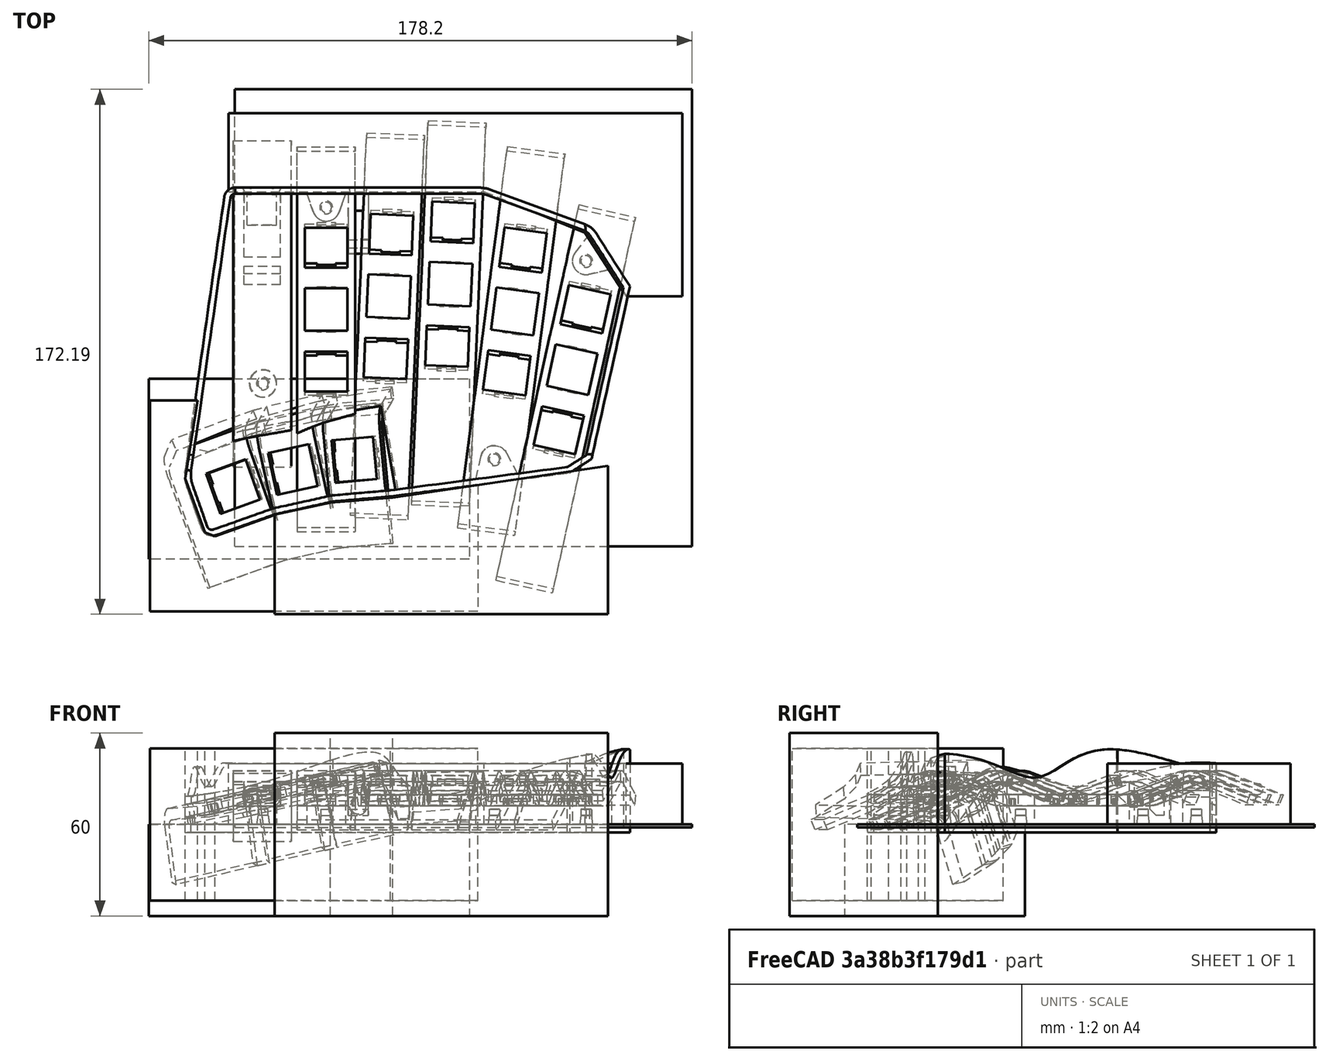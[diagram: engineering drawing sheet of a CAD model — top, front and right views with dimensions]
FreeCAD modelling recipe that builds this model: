
FCSTD DOCUMENT  (FreeCAD 0.21R33668 +26 (Git))
Label: KeyColumnArray2
License: All rights reserved
LicenseURL: http://en.wikipedia.org/wiki/All_rights_reserved
objects: PartDesign::Body×21, PartDesign::SubShapeBinder×20, Sketcher::SketchObject×20, App::Link×19, PartDesign::Pad×17, Part::MultiFuse×10, Part::Cut×9, Part::Compound×8, PartDesign::Plane×5, App::DocumentObjectGroup×4, PartDesign::Pocket×4, PartDesign::CoordinateSystem×3, Part::MultiCommon×2, Mesh::Feature×1, Part::Box×1, PartDesign::AdditivePipe×1, PartDesign::Thickness×1, PartDesign::FeatureBase×1
note: 146 computed .brp shape members not serialized (recipe doc carries the construction recipe); baked Part::Feature solids carry a one-line shape summary decoded from their .brp
EXTERNAL_REF file=KeyColumn2.FCStd obj=Cut001
EXTERNAL_REF file=KeyRowThumb2.FCStd obj=Fusion002
EXTERNAL_REF file=../components/MX_Switches.FCStd obj=Body008
EXTERNAL_REF file=KeyColumn2.FCStd obj=Extrude003
EXTERNAL_REF file=../components/PJ-313B__JACK35F-4P-PCB.FCStd obj=MultiTransform001
EXTERNAL_REF file=../components/RP2040_Zero.FCStd obj=Mesh002
EXTERNAL_REF file=../components/USBC-Breakout.FCStd obj=Body005
EXTERNAL_REF file=../components/PJ-313B__JACK35F-4P-PCB.FCStd obj=Body002
EXTERNAL_REF file=HeatsetInserts.FCStd obj=Cut001
EXTERNAL_REF file=HeatsetInserts.FCStd obj=Cut003
EXTERNAL_REF file=PlateBottom.FCStd obj=Cut001

FEATURE [App::Link] Link  label="KeyColumnCutNC0"
  LinkedObject = -> <external KeyColumn2.FCStd>#Cut001
FEATURE [App::Link] Link001  label="KeyColumnCutNC1"
  LinkPlacement = pos=(20.4361,4.27867,0) rot=(0,0,-1;0.043633rad)
  LinkedObject = -> Link
  Placement = pos=(20.4361,4.27867,0) rot=(0,0,-1;0.043633rad)
FEATURE [App::Link] Link002  label="KeyColumnCutNC2"
  LinkPlacement = pos=(40.6115,8.31848,0) rot=(0,0,-1;0.043633rad)
  LinkedObject = -> Link001
  Placement = pos=(40.6115,8.31848,0) rot=(0,0,-1;0.043633rad)
FEATURE [App::Link] Link003  label="KeyColumnCutNC3"
  LinkPlacement = pos=(61.9106,-0.613054,0) rot=(0,0,-1;0.1309rad)
  LinkedObject = -> Link002
  Placement = pos=(61.9106,-0.613054,0) rot=(0,0,-1;0.1309rad)
FEATURE [App::Link] Link004  label="KeyColumnCutNC4"
  LinkPlacement = pos=(80.6476,-19.7424,0) rot=(0,0,-1;0.218166rad)
  LinkedObject = -> Link003
  Placement = pos=(80.6476,-19.7424,0) rot=(0,0,-1;0.218166rad)
FEATURE [Mesh::Feature] _0240804_Case_RHS_rev0  label="20240804-Case-RHS-rev0"
  Placement = pos=(-0.812616,10.045,0) rot=(0,0,-1;0.043633rad)
FEATURE [App::Link] Link005  label="ThumbCluster"
  LinkPlacement = pos=(-28.6469,-56.4106,8.19493) rot=(0.134414,-0.107879,-0.985035;1.36737rad)
  LinkedObject = -> <external KeyRowThumb2.FCStd>#Fusion002
  Placement = pos=(-28.6469,-56.4106,8.19493) rot=(0.134414,-0.107879,-0.985035;1.36737rad)
FEATURE [PartDesign::SubShapeBinder] Binder  label="BinderThumb"
  BindCopyOnChange = 0
  BindMode = 0
  ClaimChildren = false
  Context = -> Body [Binder.]
  Fuse = false
  MakeFace = true
  OffsetFill = false
  OffsetIntersection = false
  OffsetJoinType = 0
  OffsetOpenResult = false
  PartialLoad = false
  Relative = true
  Support = -> [Link005[Face32]]
  _Version = 2
FEATURE [PartDesign::CoordinateSystem] Local_CS  label="Local_CS_Thumb"
  AttacherType = Attacher::AttachEngine3D
  AttachmentOffset = pos=(7,7,0) rot=(0,0,1;0rad)
  MapMode = 52
  Placement = pos=(-30.571,-58.1118,9.74542) rot=(0.024649,-0.537647,0.84281;0.407362rad)
  Support = -> [Binder]
FEATURE [App::Link] Link006  label="KeycapThumb"
  AttacherType = Attacher::AttachEngine3D
  LinkPlacement = pos=(-30.571,-58.1118,9.74542) rot=(0.024649,-0.537647,0.84281;0.407362rad)
  LinkedObject = -> <external ../components/MX_Switches.FCStd>#Body008
  MapMode = 2
  Placement = pos=(-30.571,-58.1118,9.74542) rot=(0.024649,-0.537647,0.84281;0.407362rad)
  Support = -> [Local_CS]
FEATURE [Part::Box] Box  label="Floor"
  AttacherType = Attacher::AttachEngine3D
  Height = 1
  Length = 150
  Placement = pos=(-30,-77.75,-4e-15) rot=(0.707107,0.707107,0;3.14159rad)
  Width = 150
FEATURE [PartDesign::SubShapeBinder] Binder001  label="BinderFinger"
  BindCopyOnChange = 0
  BindMode = 0
  ClaimChildren = false
  Context = -> Body [Binder001.]
  Fuse = false
  MakeFace = true
  OffsetFill = false
  OffsetIntersection = false
  OffsetJoinType = 0
  OffsetOpenResult = false
  PartialLoad = false
  Relative = true
  Support = -> [Compound[Face79]]
  _Version = 2
FEATURE [PartDesign::CoordinateSystem] Local_CS001  label="Local_CS_Finger"
  AttacherType = Attacher::AttachEngine3D
  AttachmentOffset = pos=(7,7,0) rot=(0,0,1;0rad)
  MapMode = 52
  Placement = pos=(0,-1.8e-15,9.8) rot=(0,0,1;0rad)
  Support = -> [Binder001]
FEATURE [App::Link] Link007  label="KeycapFinger"
  AttacherType = Attacher::AttachEngine3D
  LinkPlacement = pos=(0,-1.8e-15,9.8) rot=(0,0,1;0rad)
  LinkedObject = -> <external ../components/MX_Switches.FCStd>#Body008
  MapMode = 2
  Placement = pos=(0,-1.8e-15,9.8) rot=(0,0,1;0rad)
  Support = -> [Local_CS001]
FEATURE [App::Link] Link008  label="KeyColumnBlankN"
  LinkPlacement = pos=(-21,2.5034e-06,0) rot=(0,0,1;3.14159rad)
  LinkedObject = -> <external KeyColumn2.FCStd>#Extrude003
  Placement = pos=(-21,2.5034e-06,0) rot=(0,0,1;3.14159rad)
FEATURE [Part::Compound] Compound  label="KeyColumnsC"
  Links = -> [Link004,Link,Link001,Link002,Link003,Link008]
  Placement = pos=(0,0,8) rot=(0,0,1;0rad)
FEATURE [App::Link] Link010  label="TRRS-PJ-313B"
  LinkPlacement = pos=(10.5,37.75,3.5) rot=(0,0,1;0rad)
  LinkedObject = -> <external ../components/PJ-313B__JACK35F-4P-PCB.FCStd>#MultiTransform001
  Placement = pos=(10.5,37.75,3.5) rot=(0,0,1;0rad)
FEATURE [App::Link] Link011  label="RP2040-N"
  LinkPlacement = pos=(-30,14.25,8) rot=(0,0,1;0rad)
  LinkedObject = -> <external ../components/RP2040_Zero.FCStd>#Mesh002
  Placement = pos=(-30,14.25,8) rot=(0,0,1;0rad)
FEATURE [Sketcher::SketchObject] Sketch
  FullyConstrained = false
  MapMode = 5
  Support = -> [XY_Plane001]
  sketch-geometry (20):
    g0: LineSegment StartX=-33.4431 StartY=36.9112 StartZ=0 EndX=-46.2795 EndY=-52.5754 EndZ=0
    g1: LineSegment StartX=-45.7128 StartY=-58.285 StartZ=0 EndX=-40.9023 EndY=-71.8694 EndZ=0
    g2: LineSegment StartX=-36.307 StartY=-74.0612 StartZ=0 EndX=-16.9221 EndY=-67.1967 EndZ=0
    g3: LineSegment StartX=-16.9221 StartY=-67.1967 StartZ=0 EndX=2.15083 EndY=-62.9753 EndZ=0
    g4: LineSegment StartX=2.15083 StartY=-62.9753 StartZ=0 EndX=21.2304 EndY=-61.306 EndZ=0
    g5: LineSegment StartX=21.2304 StartY=-61.306 StartZ=0 EndX=79.8355 EndY=-53.6064 EndZ=0
    g6: LineSegment StartX=79.8355 StartY=-53.6064 StartZ=0 EndX=87.0661 EndY=-49 EndZ=0
    g7: LineSegment StartX=87.0661 StartY=-49 StartZ=0 EndX=99.6141 EndY=7.6 EndZ=0
    g8: LineSegment StartX=99.6141 StartY=7.6 StartZ=0 EndX=88.4546 EndY=25.1169 EndZ=0
    g9: LineSegment StartX=84.9582 StartY=27.9288 StartZ=0 EndX=53.9986 EndY=39.268 EndZ=0
    g10: LineSegment StartX=49.8716 StartY=40 StartZ=0 EndX=-29.8796 EndY=40 EndZ=0
    g11: ArcOfCircle CenterX=-37.5088 CenterY=-70.6677 CenterZ=0 NormalX=0 NormalY=0 NormalZ=1 AngleXU=0 Radius=3.6 StartAngle=3.48193 EndAngle=5.05273
    g12: ArcOfCircle CenterX=-29.8796 CenterY=36.4 CenterZ=0 NormalX=0 NormalY=0 NormalZ=1 AngleXU=0 Radius=3.6 StartAngle=1.5708 EndAngle=2.99912
    g13: GeomPoint X=-33 Y=40 Z=0
    g14: ArcOfCircle CenterX=-34.4011 CenterY=-54.2793 CenterZ=0 NormalX=0 NormalY=0 NormalZ=1 AngleXU=0 Radius=12 StartAngle=2.99912 EndAngle=3.48193
    g15: GeomPoint X=-46.699 Y=-55.5 Z=0
    g16: ArcOfCircle CenterX=49.8716 CenterY=28 CenterZ=0 NormalX=0 NormalY=0 NormalZ=1 AngleXU=0 Radius=12 StartAngle=1.21971 EndAngle=1.5708
    g17: GeomPoint X=52 Y=40 Z=0
    g18: ArcOfCircle CenterX=82.5508 CenterY=21.3558 CenterZ=0 NormalX=0 NormalY=0 NormalZ=1 AngleXU=0 Radius=7 StartAngle=0.567232 EndAngle=1.21971
    g19: GeomPoint X=87.1821 Y=27.1143 Z=0
  constraints (43):
    c: Coincident(g2,g3)
    c: Coincident(g3,g4)
    c: Coincident(g4,g5)
    c: Coincident(g5,g6)
    c: Coincident(g6,g7)
    c: Coincident(g7,g8)
    c: Horizontal(g10)
    c: DistanceY(g-1,g17) = 40
    c: DistanceX(g-1,g17) = 52
    c: DistanceX(g13,g-1) = 33
    c: Angle(g-1,g7) = 1.35263
    c: Angle(g7,g6) = 2.35619
    c: Perpendicular(g2,g1)
    c: Angle(g-2,g1) = 0.340339
    c: DistanceY(g15,g-1) = 55.5
    c: Tangent(g1,g11) = -1.5708
    c: Tangent(g2,g11) = -1.5708
    c: Radius(g11) = 3.6
    c: Angle(g-2,g3) = 1.78861
    c: Angle(g4,g-2) = 1.48353
    c: PointOnObject(g13,g0)
    c: PointOnObject(g13,g10)
    c: Tangent(g0,g12) = -1.5708
    c: Tangent(g10,g12) = -1.5708
    c: Radius(g12) = 3.6
    c: PointOnObject(g15,g1)
    c: PointOnObject(g15,g0)
    c: Tangent(g1,g14) = -1.5708
    c: Tangent(g0,g14) = -1.5708
    c: Radius(g14) = 12
    c: PointOnObject(g17,g10)
    c: PointOnObject(g17,g9)
    c: Tangent(g10,g16) = -1.5708
    c: Tangent(g9,g16) = -1.5708
    c: Radius(g16) = 12
    c: PointOnObject(g19,g9)
    c: PointOnObject(g19,g8)
    c: Tangent(g9,g18) = -1.5708
    c: Tangent(g8,g18) = -1.5708
    c: Radius(g18) = 7
    c: Angle(g8,g7) = 2.35619
    c: DistanceY(g-1,g7) = 7.6
    c: DistanceY(g6,g-1) = 49
FEATURE [PartDesign::Pad] Pad
  Direction = (0,0,1)
  Length = 30
  Length2 = 10
  Profile = -> Sketch
  ReferenceAxis = -> Sketch [N_Axis]
  Type = 0
FEATURE [Sketcher::SketchObject] Sketch001
  FullyConstrained = false
  MapMode = 5
  Support = -> [XY_Plane002]
  sketch-geometry (7):
    g0: LineSegment StartX=-31.9823 StartY=64.42 StartZ=0 EndX=-31.9823 EndY=38.6825 EndZ=0
    g1: LineSegment StartX=-31.9823 StartY=38.6825 StartZ=0 EndX=51.7413 EndY=38.6825 EndZ=0
    g2: LineSegment StartX=51.7413 StartY=38.6825 StartZ=0 EndX=84.9247 EndY=25.1531 EndZ=0
    g3: LineSegment StartX=84.9247 StartY=25.1531 StartZ=0 EndX=98.4266 EndY=4.34688 EndZ=0
    g4: LineSegment StartX=98.4266 StartY=4.34688 StartZ=0 EndX=116.798 EndY=4.34688 EndZ=0
    g5: LineSegment StartX=116.798 StartY=4.34688 StartZ=0 EndX=116.798 EndY=64.42 EndZ=0
    g6: LineSegment StartX=116.798 StartY=64.42 StartZ=0 EndX=-31.9823 EndY=64.42 EndZ=0
  constraints (12):
    c: Vertical(g0)
    c: Coincident(g0,g1)
    c: Horizontal(g1)
    c: Coincident(g1,g2)
    c: Coincident(g2,g3)
    c: Coincident(g3,g4)
    c: Horizontal(g4)
    c: Coincident(g4,g5)
    c: Vertical(g5)
    c: Coincident(g5,g6)
    c: Coincident(g6,g0)
    c: Horizontal(g6)
FEATURE [PartDesign::Pad] Pad001
  Direction = (0,0,1)
  Length = 20
  Length2 = 10
  Profile = -> Sketch001
  ReferenceAxis = -> Sketch001 [N_Axis]
  Type = 0
FEATURE [PartDesign::Body] Body002  label="ColumnCutterTop"
  Group = -> [Sketch001,Pad001]
  Origin = -> Origin002
  Tip = -> Pad001
FEATURE [Sketcher::SketchObject] Sketch002
  FullyConstrained = false
  MapMode = 5
  Support = -> [XY_Plane003]
  sketch-geometry (11):
    g0: LineSegment StartX=-57.8461 StartY=-29.8467 StartZ=0 EndX=-42.1659 EndY=-29.8467 EndZ=0
    g1: LineSegment StartX=-42.1659 StartY=-29.8467 StartZ=0 EndX=-46.2211 EndY=-55.5298 EndZ=0
    g2: LineSegment StartX=-46.2211 StartY=-55.5298 StartZ=0 EndX=-39.7328 EndY=-73.1024 EndZ=0
    g3: LineSegment StartX=-39.7328 StartY=-73.1024 StartZ=0 EndX=-36.4886 EndY=-74.4541 EndZ=0
    g4: LineSegment StartX=-36.4886 StartY=-74.4541 StartZ=0 EndX=-17.0235 EndY=-67.4251 EndZ=0
    g5: LineSegment StartX=-17.0235 StartY=-67.4251 StartZ=0 EndX=1.36017 EndY=-63.3699 EndZ=0
    g6: LineSegment StartX=1.36017 StartY=-63.3699 StartZ=0 EndX=21.0956 EndY=-61.4774 EndZ=0
    g7: LineSegment StartX=21.0956 StartY=-61.4774 StartZ=0 EndX=49.7525 EndY=-57.6925 EndZ=0
    g8: LineSegment StartX=49.7525 StartY=-57.6925 StartZ=0 EndX=49.7525 EndY=-99.0559 EndZ=0
    g9: LineSegment StartX=49.7525 StartY=-99.0559 StartZ=0 EndX=-57.8461 EndY=-99.0559 EndZ=0
    g10: LineSegment StartX=-57.8461 StartY=-99.0559 StartZ=0 EndX=-57.8461 EndY=-29.8467 EndZ=0
  constraints (15):
    c: Horizontal(g0)
    c: Coincident(g0,g1)
    c: Coincident(g1,g2)
    c: Coincident(g2,g3)
    c: Coincident(g3,g4)
    c: Coincident(g4,g5)
    c: Coincident(g5,g6)
    c: Coincident(g6,g7)
    c: Coincident(g7,g8)
    c: Vertical(g8)
    c: Coincident(g8,g9)
    c: Horizontal(g9)
    c: Coincident(g9,g10)
    c: Coincident(g10,g0)
    c: Vertical(g10)
FEATURE [PartDesign::Pad] Pad002
  Direction = (0,0,1)
  Length = 50
  Length2 = 10
  Midplane = true
  Profile = -> Sketch002
  ReferenceAxis = -> Sketch002 [N_Axis]
  Type = 0
FEATURE [PartDesign::Body] Body003  label="ThumbCutterBotLeft"
  Group = -> [Sketch002,Pad002]
  Origin = -> Origin003
  Tip = -> Pad002
FEATURE [Sketcher::SketchObject] Sketch003
  FullyConstrained = false
  MapMode = 5
  Support = -> [XY_Plane004]
  sketch-geometry (4):
    g0: LineSegment StartX=-58.202 StartY=-22.7672 StartZ=0 EndX=46.9496 EndY=-22.7672 EndZ=0
    g1: LineSegment StartX=46.9496 StartY=-22.7672 StartZ=0 EndX=46.9496 EndY=-81.8868 EndZ=0
    g2: LineSegment StartX=46.9496 StartY=-81.8868 StartZ=0 EndX=-58.202 EndY=-81.8868 EndZ=0
    g3: LineSegment StartX=-58.202 StartY=-81.8868 StartZ=0 EndX=-58.202 EndY=-22.7672 EndZ=0
  constraints (8):
    c: Coincident(g0,g1)
    c: Coincident(g1,g2)
    c: Coincident(g2,g3)
    c: Coincident(g3,g0)
    c: Horizontal(g0)
    c: Horizontal(g2)
    c: Vertical(g1)
    c: Vertical(g3)
FEATURE [PartDesign::Pad] Pad003
  Direction = (0,0,1)
  Length = 30
  Length2 = 10
  Profile = -> Sketch003
  ReferenceAxis = -> Sketch003 [N_Axis]
  Reversed = true
  Type = 0
FEATURE [PartDesign::Body] Body004  label="ThumbCutterBottom"
  Group = -> [Sketch003,Pad003]
  Origin = -> Origin004
  Tip = -> Pad003
FEATURE [Sketcher::SketchObject] Sketch004
  FullyConstrained = false
  MapMode = 5
  Support = -> [XY_Plane005]
  sketch-geometry (6):
    g0: LineSegment StartX=-16.8908 StartY=-67.2591 StartZ=0 EndX=1.39342 EndY=-63.2974 EndZ=0
    g1: LineSegment StartX=1.39342 StartY=-63.2974 StartZ=0 EndX=21.8742 EndY=-61.6751 EndZ=0
    g2: LineSegment StartX=21.8742 StartY=-61.6751 StartZ=0 EndX=92.4415 EndY=-51.3334 EndZ=0
    g3: LineSegment StartX=92.4415 StartY=-51.3334 StartZ=0 EndX=92.4415 EndY=-99.9441 EndZ=0
    g4: LineSegment StartX=92.4415 StartY=-99.9441 StartZ=0 EndX=-16.8908 EndY=-99.9441 EndZ=0
    g5: LineSegment StartX=-16.8908 StartY=-99.9441 StartZ=0 EndX=-16.8908 EndY=-67.2591 EndZ=0
  constraints (9):
    c: Coincident(g0,g1)
    c: Coincident(g1,g2)
    c: Coincident(g2,g3)
    c: Vertical(g3)
    c: Coincident(g3,g4)
    c: Horizontal(g4)
    c: Coincident(g4,g5)
    c: Coincident(g5,g0)
    c: Vertical(g5)
FEATURE [PartDesign::Pad] Pad004
  Direction = (0,0,1)
  Length = 60
  Length2 = 10
  Midplane = true
  Profile = -> Sketch004
  ReferenceAxis = -> Sketch004 [N_Axis]
  Type = 0
FEATURE [PartDesign::Body] Body005  label="ColumnCutterBottom"
  Group = -> [Sketch004,Pad004]
  Origin = -> Origin005
  Tip = -> Pad004
FEATURE [Part::Compound] Compound001  label="ColumnCutters"
  Links = -> [Body005,Body002]
FEATURE [Part::MultiFuse] Fusion
  Shapes = -> [Compound]
FEATURE [Part::Compound] Compound002  label="ThumbCutters"
  Links = -> [Body003,Body004]
FEATURE [Part::Cut] Cut001
  Base = -> Link005
  Tool = -> Body003
FEATURE [Part::Cut] Cut002  label="ThumbClusterCut"
  Base = -> Cut001
  Tool = -> Body004
FEATURE [Part::Compound] Compound003  label="ThumbClusterC"
  Links = -> [Link005]
FEATURE [PartDesign::SubShapeBinder] Binder003  label="Big"
  BindCopyOnChange = 0
  BindMode = 0
  ClaimChildren = false
  Context = -> Body006 [Binder003.]
  Fuse = false
  MakeFace = true
  OffsetFill = false
  OffsetIntersection = false
  OffsetJoinType = 0
  OffsetOpenResult = false
  PartialLoad = false
  Relative = true
  Support = -> [Cut002[Edge44,Edge45,Edge46,Edge47]]
  _Version = 2
FEATURE [PartDesign::SubShapeBinder] Binder004  label="Small"
  BindCopyOnChange = 0
  BindMode = 0
  ClaimChildren = false
  Context = -> Body006 [Binder004.]
  Fuse = false
  MakeFace = true
  OffsetFill = false
  OffsetIntersection = false
  OffsetJoinType = 0
  OffsetOpenResult = false
  PartialLoad = false
  Relative = true
  Support = -> [Cut002[Edge127,Edge129,Edge130,Edge131]]
  _Version = 2
FEATURE [PartDesign::SubShapeBinder] Binder005  label="Path"
  BindCopyOnChange = 0
  BindMode = 0
  ClaimChildren = false
  Context = -> Body006 [Binder005.]
  Fuse = false
  MakeFace = true
  OffsetFill = false
  OffsetIntersection = false
  OffsetJoinType = 0
  OffsetOpenResult = false
  PartialLoad = false
  Relative = true
  Support = -> [Cut002[Edge127,Edge126,Edge123,Edge122,Edge109]]
  _Version = 2
FEATURE [Sketcher::SketchObject] Sketch005
  FullyConstrained = false
  Placement = pos=(-2.47193,-0.548013,11.4209) rot=(0.216439,-0.976296,0;0.218166rad)
  sketch-geometry (5):
    g0: LineSegment StartX=21.4334 StartY=-34.223 StartZ=0 EndX=2.51313 EndY=-35.9615 EndZ=0
    g1: BSplineCurve PolesCount=2 KnotsCount=2 Degree=1 IsPeriodic=0
    g2: LineSegment StartX=-1.05539 StartY=-36.5965 StartZ=0 EndX=-19.605 EndY=-40.7088 EndZ=0
    g3: BSplineCurve PolesCount=2 KnotsCount=2 Degree=1 IsPeriodic=0
    g4: LineSegment StartX=-23.1076 StartY=-41.6414 StartZ=0 EndX=-40.9899 EndY=-48.0619 EndZ=0
  constraints (4):
    c: Coincident(g0,g1)
    c: Coincident(g1,g2)
    c: Coincident(g2,g3)
    c: Coincident(g3,g4)
FEATURE [Sketcher::SketchObject] Sketch006
  FullyConstrained = false
  Placement = pos=(-50.3364,-18.2454,-11.7703) rot=(0.340774,-0.940145,0;1.78719rad)
  sketch-geometry (4):
    g0: LineSegment StartX=34.9538 StartY=-48.5618 StartZ=0 EndX=33.5799 EndY=-45.0789 EndZ=0
    g1: LineSegment StartX=33.5799 StartY=-45.0789 StartZ=0 EndX=26.6082 EndY=-27.4042 EndZ=0
    g2: ArcOfCircle CenterX=22.8872 CenterY=-28.8719 CenterZ=0 NormalX=0 NormalY=1e-16 NormalZ=1 AngleXU=-2.76588 Radius=4 StartAngle=1.5708 EndAngle=2.88852
    g3: LineSegment StartX=21.8685 StartY=-24.9672 StartZ=0 EndX=22.3979 EndY=-24.902 EndZ=0
  constraints (3):
    c: Coincident(g0,g1)
    c: Coincident(g1,g2)
    c: Coincident(g2,g3)
FEATURE [Sketcher::SketchObject] Sketch007
  FullyConstrained = false
  Placement = pos=(17.7176,1.57374,3.9103) rot=(-0.088475,0.996078,0;1.3544rad)
  sketch-geometry (6):
    g0: LineSegment StartX=-9.09004 StartY=-79.2968 StartZ=0 EndX=-11.138 EndY=-61.1386 EndZ=0
    g1: LineSegment StartX=-11.138 StartY=-61.1386 StartZ=0 EndX=-13.3253 EndY=-42.1061 EndZ=0
    g2: ArcOfCircle CenterX=-5.98227 CenterY=-40.8863 CenterZ=0 NormalX=1e-16 NormalY=0 NormalZ=1 AngleXU=-1.45423 Radius=7.44361 StartAngle=3.36428 EndAngle=4.76043
    g3: LineSegment StartX=9.38655 StartY=-26.7286 StartZ=0 EndX=-8.45934 EndY=-33.867 EndZ=0
    g4: LineSegment StartX=-9.09004 StartY=-79.2968 StartZ=0 EndX=18.9825 EndY=-76.3619 EndZ=0
    g5: LineSegment StartX=18.9825 StartY=-76.3619 StartZ=0 EndX=9.38655 EndY=-26.7286 EndZ=0
  constraints (6):
    c: Coincident(g0,g1)
    c: Coincident(g1,g2)
    c: Coincident(g2,g3)
    c: Coincident(g0,g4)
    c: Coincident(g4,g5)
    c: Coincident(g5,g3)
FEATURE [PartDesign::AdditivePipe] AdditivePipe
  AuxilleryCurvelinear = true
  AuxillerySpineTangent = false
  Binormal = (0,0,0)
  Mode = 0
  Placement = pos=(17.7176,1.57374,3.9103) rot=(-0.088475,0.996078,0;1.3544rad)
  Profile = -> Sketch007
  Spine = -> Binder005
  SpineTangent = false
  Transformation = 0
  Transition = 0
FEATURE [PartDesign::Body] Body006  label="UnderThumbCutter"
  Group = -> [Binder003,Binder004,Binder005,Sketch005,Sketch006,Sketch007,AdditivePipe]
  Origin = -> Origin006
  Tip = -> AdditivePipe
FEATURE [Sketcher::SketchObject] Sketch008
  FullyConstrained = true
  MapMode = 5
  Placement = pos=(0,0,0) rot=(0.57735,0.57735,0.57735;2.0944rad)
  Support = -> [YZ_Plane007]
  sketch-geometry (8):
    g0: LineSegment StartX=-24 StartY=5.5 StartZ=0 EndX=-24 EndY=0 EndZ=0
    g1: LineSegment StartX=-24 StartY=0 StartZ=0 EndX=1.25 EndY=0 EndZ=0
    g2: LineSegment StartX=1.25 StartY=0 StartZ=0 EndX=1.25 EndY=-3.6 EndZ=0
    g3: LineSegment StartX=1.25 StartY=-3.6 StartZ=0 EndX=-4.9788 EndY=-4.78813 EndZ=0
    g4: LineSegment StartX=-4.9788 StartY=-4.78813 StartZ=0 EndX=-30.1 EndY=0 EndZ=0
    g5: LineSegment StartX=-30.1 StartY=0 StartZ=0 EndX=-30.1 EndY=2 EndZ=0
    g6: LineSegment StartX=-30.1 StartY=2 StartZ=0 EndX=-26.6 EndY=5.5 EndZ=0
    g7: LineSegment StartX=-26.6 StartY=5.5 StartZ=0 EndX=-24 EndY=5.5 EndZ=0
  constraints (24):
    c: PointOnObject(g0,g-1)
    c: Vertical(g0)
    c: Coincident(g0,g1)
    c: Horizontal(g1)
    c: Coincident(g1,g2)
    c: Vertical(g2)
    c: Coincident(g2,g3)
    c: Coincident(g3,g4)
    c: PointOnObject(g4,g-1)
    c: Coincident(g4,g5)
    c: Vertical(g5)
    c: Coincident(g5,g6)
    c: Coincident(g6,g7)
    c: Coincident(g7,g0)
    c: Horizontal(g7)
    c: DistanceX(g7,g7) = 2.6
    c: DistanceY(g0,g0) = 5.5
    c: DistanceX(g5,g6) = 3.5
    c: Angle(g6,g7) = 2.35619
    c: DistanceX(g0,g-1) = 24
    c: DistanceX(g-1,g1) = 1.25
    c: DistanceY(g2,g2) = 3.6
    c: DistanceX(g3) = -4.9788
    c: DistanceY(g3) = -4.78813
FEATURE [PartDesign::Pad] Pad005
  Direction = (1,-2e-16,3e-16)
  Length = 12
  Length2 = 10
  Midplane = true
  Placement = pos=(0,0,0) rot=(0.57735,0.57735,0.57735;2.0944rad)
  Profile = -> Sketch008
  ReferenceAxis = -> Sketch008 [N_Axis]
  Type = 0
FEATURE [PartDesign::Body] Body007  label="MCU-Holder"
  Group = -> [Sketch008,Pad005]
  Origin = -> Origin007
  Placement = pos=(-21,38.25,11.25) rot=(0,1,0;3.14159rad)
  Tip = -> Pad005
FEATURE [Sketcher::SketchObject] Sketch009
  FullyConstrained = false
  MapMode = 5
  Placement = pos=(0,0,0) rot=(0.57735,0.57735,0.57735;2.0944rad)
  Support = -> [YZ_Plane008]
  sketch-geometry (9):
    g0: LineSegment StartX=39.5 StartY=9 StartZ=0 EndX=22.8616 EndY=9 EndZ=0
    g1: LineSegment StartX=22.8616 StartY=9 StartZ=0 EndX=22.8616 EndY=3 EndZ=0
    g2: LineSegment StartX=22.8616 StartY=3 StartZ=0 EndX=20.2616 EndY=3 EndZ=0
    g3: LineSegment StartX=20.2616 StartY=3 StartZ=0 EndX=18.2616 EndY=5 EndZ=0
    g4: LineSegment StartX=18.2616 StartY=5 StartZ=0 EndX=18.2616 EndY=10.5 EndZ=0
    g5: LineSegment StartX=39.5 StartY=11.5 StartZ=0 EndX=39.5 EndY=9 EndZ=0
    g6: LineSegment StartX=18.2616 StartY=10.5 StartZ=0 EndX=32.4662 EndY=16.0518 EndZ=0
    g7: LineSegment StartX=32.4662 StartY=16.0518 StartZ=0 EndX=39.5 EndY=13.7315 EndZ=0
    g8: LineSegment StartX=39.5 StartY=11.5 StartZ=0 EndX=39.5 EndY=13.7315 EndZ=0
  constraints (22):
    c: Horizontal(g0)
    c: Coincident(g0,g1)
    c: Vertical(g1)
    c: Coincident(g1,g2)
    c: Coincident(g2,g3)
    c: Coincident(g3,g4)
    c: Vertical(g4)
    c: Coincident(g5,g0)
    c: Vertical(g5)
    c: DistanceX(g0) = 39.5
    c: DistanceY(g0) = 9
    c: DistanceY(g5,g5) = 2.5
    c: Horizontal(g2)
    c: DistanceX(g2,g2) = 2.6
    c: Angle(g2,g3) = 2.35619
    c: DistanceY(g1,g1) = 6
    c: DistanceY(g2,g3) = 2
    c: Coincident(g6,g7)
    c: Coincident(g8,g5)
    c: Coincident(g8,g7)
    c: Vertical(g8)
    c: Coincident(g6,g4)
FEATURE [PartDesign::Pad] Pad006
  Direction = (1,-2e-16,3e-16)
  Length = 6.5
  Length2 = 10
  Midplane = true
  Placement = pos=(0,0,0) rot=(1,1,1;2.0944rad)
  Profile = -> Sketch009
  ReferenceAxis = -> Sketch009 [N_Axis]
  Type = 0
FEATURE [PartDesign::Body] Body008  label="TRRS-Holder"
  Group = -> [Sketch009,Pad006]
  Origin = -> Origin008
  Placement = pos=(10.5,0,0) rot=(0,0,1;0rad)
  Tip = -> Pad006
FEATURE [App::Link] Link012  label="MCU-Cutter"
  LinkPlacement = pos=(-21.17,19.2029,7) rot=(0,0,1;3.14159rad)
  LinkedObject = -> <external ../components/USBC-Breakout.FCStd>#Body005
  Placement = pos=(-21.17,19.2029,7) rot=(0,0,1;3.14159rad)
FEATURE [App::Link] Link013  label="TRRS-Cutter"
  LinkPlacement = pos=(10.5,31.25,3.5) rot=(0,0,1;0rad)
  LinkedObject = -> <external ../components/PJ-313B__JACK35F-4P-PCB.FCStd>#Body002
  Placement = pos=(10.5,31.25,3.5) rot=(0,0,1;0rad)
FEATURE [App::DocumentObjectGroup] Group001  label="Parts"
  Group = -> [Link010,Link011,Link012,Link013]
FEATURE [App::Link] Link014  label="HeatsetTopRightA"
  LinkPlacement = pos=(85.2349,15.9434,3) rot=(0,0,1;2.13803rad)
  LinkedObject = -> <external HeatsetInserts.FCStd>#Cut001
  Placement = pos=(85.2349,15.9434,3) rot=(0,0,1;2.13803rad)
FEATURE [App::Link] Link015  label="HeatsetTopLeftA"
  LinkPlacement = pos=(5.38627e-06,33.5,3) rot=(0,0,1;3.14159rad)
  LinkedObject = -> Link014
  Placement = pos=(5.38627e-06,33.5,3) rot=(0,0,1;3.14159rad)
FEATURE [App::Link] Link017  label="HeatsetBotRightA"
  LinkPlacement = pos=(55.1436,-49.1268,3) rot=(0,0,1;0.1309rad)
  LinkedObject = -> Link014
  Placement = pos=(55.1436,-49.1268,3) rot=(0,0,1;0.1309rad)
FEATURE [PartDesign::Thickness] Thickness
  Base = -> Pad [Face18,Face17]
  BaseFeature = -> Pad
  Intersection = false
  Join = 0
  Mode = 0
  Reversed = true
  SupportTransform = false
  Value = 2
FEATURE [PartDesign::Body] Body001  label="ShellRough"
  Group = -> [Sketch,Pad,Thickness]
  Origin = -> Origin001
  Tip = -> Thickness
FEATURE [PartDesign::SubShapeBinder] Binder006  label="BinderFingerR2C4"
  BindCopyOnChange = 0
  BindMode = 0
  ClaimChildren = false
  Context = -> Body [Binder006.]
  Fuse = false
  MakeFace = true
  OffsetFill = false
  OffsetIntersection = false
  OffsetJoinType = 0
  OffsetOpenResult = false
  PartialLoad = false
  Relative = true
  Support = -> [Compound[Face19]]
  _Version = 2
FEATURE [PartDesign::CoordinateSystem] Local_CS002  label="Local_CS_FR2C4"
  AttacherType = Attacher::AttachEngine3D
  AttachmentOffset = pos=(7,7,0) rot=(0,0,1;0rad)
  MapMode = 52
  Placement = pos=(76.2491,-39.5828,13.5665) rot=(-0.857127,0.093871,-0.50648;0.425909rad)
  Support = -> [Binder006]
FEATURE [PartDesign::Body] Body  label="BodyForLCS"
  Group = -> [Binder,Local_CS,Binder001,Local_CS001,Binder006,Local_CS002]
  Origin = -> Origin
FEATURE [App::Link] Link018  label="KeycapFinger001"
  AttacherType = Attacher::AttachEngine3D
  LinkPlacement = pos=(76.2491,-39.5828,13.5665) rot=(-0.857127,0.093871,-0.50648;0.425909rad)
  LinkedObject = -> Link007
  MapMode = 2
  Placement = pos=(76.2491,-39.5828,13.5665) rot=(-0.857127,0.093871,-0.50648;0.425909rad)
  Support = -> [Local_CS002]
FEATURE [App::DocumentObjectGroup] Group  label="Keycaps"
  Group = -> [Link006,Link007,Link018,Body]
FEATURE [PartDesign::FeatureBase] BaseFeature
  BaseFeature = -> Pad
FEATURE [PartDesign::Body] Body009  label="ShellCutterPart"
  BaseFeature = -> Pad
  Group = -> [BaseFeature]
  Origin = -> Origin009
  Tip = -> BaseFeature
FEATURE [Part::Compound] Compound004  label="ThumbClusterC001"
  Links = -> [Link005]
FEATURE [Part::MultiCommon] Common  label="ThumbClusterCom"
  Refine = true
  Shapes = -> [Body009,Compound004]
FEATURE [Part::MultiFuse] Fusion001  label="KeyColumnsF"
  Shapes = -> [Compound]
FEATURE [Part::MultiCommon] Common001  label="KeyColumnsCom"
  Refine = true
  Shapes = -> [Body009,Fusion001]
FEATURE [Part::Cut] Cut  label="KeyColumnsCut"
  Base = -> Common001
  Tool = -> Body006
FEATURE [PartDesign::SubShapeBinder] Binder008
  BindCopyOnChange = 0
  BindMode = 0
  ClaimChildren = false
  Context = -> Body010 [Binder008.]
  Fuse = false
  MakeFace = true
  OffsetFill = false
  OffsetIntersection = false
  OffsetJoinType = 0
  OffsetOpenResult = false
  PartialLoad = false
  Relative = true
  Support = -> [Common[Face16,Face15,Face14,Face13,Face12]]
  _Version = 2
FEATURE [PartDesign::SubShapeBinder] Binder009
  BindCopyOnChange = 0
  BindMode = 0
  ClaimChildren = false
  Context = -> Body010 [Binder009.]
  Fuse = false
  MakeFace = true
  OffsetFill = false
  OffsetIntersection = false
  OffsetJoinType = 0
  OffsetOpenResult = false
  PartialLoad = false
  Relative = true
  Support = -> [Common[Face6,Face7,Face8,Face9,Face10]]
  _Version = 2
FEATURE [PartDesign::Plane] DatumPlane
  Length = 90.3213
  MapMode = 45
  Placement = pos=(10.8462,-31.5971,6.48979) rot=(-0.487707,-0.562269,-0.667829;1.80626rad)
  ResizeMode = 0
  Support = -> [Binder008,Binder009]
  Width = 97.1376
FEATURE [Sketcher::SketchObject] Sketch010
  FullyConstrained = false
  MapMode = 5
  Placement = pos=(10.8462,-31.5971,6.48979) rot=(-0.487707,-0.562269,-0.667829;1.80626rad)
  Support = -> [DatumPlane]
  sketch-geometry (7):
    g0: LineSegment StartX=-5.99127 StartY=-62.4069 StartZ=0 EndX=-2.7146 EndY=-38.9241 EndZ=0
    g1: LineSegment StartX=-2.7146 StartY=-38.9241 StartZ=0 EndX=-1.48585 EndY=-31.6881 EndZ=0
    g2: LineSegment StartX=-1.48585 StartY=-31.6881 StartZ=0 EndX=1.51776 EndY=-16.1239 EndZ=0
    g3: LineSegment StartX=1.51776 StartY=-16.1239 StartZ=0 EndX=2.88304 EndY=-9.5706 EndZ=0
    g4: LineSegment StartX=2.88304 StartY=-9.5706 StartZ=0 EndX=7.38846 EndY=8.9972 EndZ=0
    g5: LineSegment StartX=7.38846 StartY=8.9972 StartZ=0 EndX=-10.3602 EndY=14.0487 EndZ=0
    g6: LineSegment StartX=-10.3602 StartY=14.0487 StartZ=0 EndX=-5.99127 EndY=-62.4069 EndZ=0
  constraints (7):
    c: Coincident(g0,g1)
    c: Coincident(g1,g2)
    c: Coincident(g2,g3)
    c: Coincident(g3,g4)
    c: Coincident(g4,g5)
    c: Coincident(g5,g6)
    c: Coincident(g6,g0)
FEATURE [PartDesign::Pad] Pad007
  Direction = (-0.145065,0.93735,0.31675)
  Length = 20
  Length2 = 10
  Midplane = true
  Placement = pos=(10.8462,-31.5971,6.48979) rot=(-0.487707,-0.562269,-0.667829;1.80626rad)
  Profile = -> Sketch010
  ReferenceAxis = -> Sketch010 [N_Axis]
  Type = 0
FEATURE [PartDesign::Body] Body010  label="ThumbTriangleCutter"
  Group = -> [Binder008,Binder009,DatumPlane,Sketch010,Pad007]
  Origin = -> Origin010
  Tip = -> Pad007
FEATURE [Part::Cut] Cut003  label="ThumbClusterCut2"
  Base = -> Common
  Tool = -> Body010
FEATURE [Part::Compound] Compound005
  Links = -> [Body001]
FEATURE [App::DocumentObjectGroup] Group003  label="Shell"
FEATURE [Sketcher::SketchObject] Sketch011
  FullyConstrained = false
  MapMode = 5
  Placement = pos=(0,0,0) rot=(1,0,0;1.5708rad)
  Support = -> [XZ_Plane011]
  sketch-geometry (23):
    g0: LineSegment StartX=-51.25 StartY=39.47 StartZ=0 EndX=-51.25 EndY=8.74275 EndZ=0
    g1: LineSegment StartX=-51.25 StartY=8.74275 StartZ=0 EndX=18.1024 EndY=24.754 EndZ=0
    g2: LineSegment StartX=22.4199 StartY=22.0561 StartZ=0 EndX=24.2026 EndY=14.3346 EndZ=0
    g3: LineSegment StartX=28.2541 StartY=11.5857 StartZ=0 EndX=107.47 EndY=23.6899 EndZ=0
    g4: LineSegment StartX=107.47 StartY=23.6899 StartZ=0 EndX=107.47 EndY=39.47 EndZ=0
    g5: LineSegment StartX=107.47 StartY=39.47 StartZ=0 EndX=-51.25 EndY=39.47 EndZ=0
    g6: ArcOfCircle CenterX=18.9122 CenterY=21.2463 CenterZ=0 NormalX=0 NormalY=0 NormalZ=1 AngleXU=0 Radius=3.6 StartAngle=0.226893 EndAngle=1.79769
    g7: ArcOfCircle CenterX=27.7103 CenterY=15.1444 CenterZ=0 NormalX=0 NormalY=0 NormalZ=1 AngleXU=0 Radius=3.6 StartAngle=3.36849 EndAngle=4.86402
    g8-g15: Circle x8 (B-spline internal-alignment scaffolding for g16; pole/knot coordinates omitted)
    g16: BSplineCurve PolesCount=8 KnotsCount=6 Degree=3 IsPeriodic=0
    g17-g22: GeomPoint x6 (B-spline internal-alignment scaffolding for g16; pole/knot coordinates omitted)
  constraints (24):
    c: Vertical(g0)
    c: Coincident(g0,g1)
    c: Coincident(g3,g4)
    c: Vertical(g4)
    c: Coincident(g4,g5)
    c: Coincident(g5,g0)
    c: Horizontal(g5)
    c: Tangent(g1,g6) = 1.5708
    c: Tangent(g2,g6) = 1.5708
    c: Tangent(g2,g7) = -1.5708
    c: Tangent(g3,g7) = -1.5708
    c: Radius(g6) = 3.6
    c: Radius(g7) = 3.6
    c: DistanceX(g0,g-1) = 51.25
    c: DistanceX(g-1,g3) = 107.47
    c: DistanceY(g-1,g0) = 39.47
    c: Angle(g-1,g1) = 0.226893
    c: Perpendicular(g2,g1)
    c: Weight(g8) = 1
    c: Coincident(g16,g0)
    c: Equal(g8, g9-g15) x7
    c: Coincident(g16,g4)
    c: InternalAlignment(g8-g15 -> g16) x8
    c: InternalAlignment(g17-g22 -> g16) x6
FEATURE [PartDesign::Pad] Pad008
  Direction = (0,-1,2e-16)
  Length = 40
  Length2 = 10
  Placement = pos=(0,0,0) rot=(1,0,0;1.5708rad)
  Profile = -> Sketch011
  ReferenceAxis = -> Sketch011 [N_Axis]
  Type = 0
FEATURE [PartDesign::Body] Body011  label="WaveFront"
  Group = -> [Sketch011,Pad008]
  Origin = -> Origin011
  Placement = pos=(0,-47.5,0) rot=(0,0,1;0rad)
  Tip = -> Pad008
FEATURE [Part::Cut] Cut004
  Base = -> Compound005
  Tool = -> Body011
FEATURE [PartDesign::SubShapeBinder] Binder010
  BindCopyOnChange = 0
  BindMode = 0
  ClaimChildren = false
  Context = -> Body012 [Binder010.]
  Fuse = false
  MakeFace = true
  OffsetFill = false
  OffsetIntersection = false
  OffsetJoinType = 0
  OffsetOpenResult = false
  PartialLoad = false
  Relative = true
  Support = -> [Cut004[Face1]]
  _Version = 2
FEATURE [Sketcher::SketchObject] Sketch012
  ExternalGeometry = -> [Binder010]
  FullyConstrained = false
  MapMode = 5
  Placement = pos=(0,0,0) rot=(0.57735,0.57735,0.57735;2.0944rad)
  Support = -> [YZ_Plane012]
  sketch-geometry (23):
    g0: LineSegment StartX=-52.5227 StartY=18.3739 StartZ=0 EndX=-52.5227 EndY=37.6741 EndZ=0
    g1: LineSegment StartX=-52.5227 StartY=37.6741 StartZ=0 EndX=56.4163 EndY=37.6741 EndZ=0
    g2: LineSegment StartX=56.4163 StartY=9.13411 StartZ=0 EndX=51.2893 EndY=9.20452 EndZ=0
    g3-g12: Circle x10 (B-spline internal-alignment scaffolding for g13; pole/knot coordinates omitted)
    g13: BSplineCurve PolesCount=10 KnotsCount=8 Degree=3 IsPeriodic=0
    g14-g21: GeomPoint x8 (B-spline internal-alignment scaffolding for g13; pole/knot coordinates omitted)
    g22: LineSegment StartX=56.4163 StartY=9.13411 StartZ=0 EndX=56.4163 EndY=37.6741 EndZ=0
  constraints (16):
    c: Vertical(g0)
    c: Coincident(g0,g1)
    c: Horizontal(g1)
    c: DistanceX(g0) = -52.5227
    c: DistanceY(g0) = 18.3739
    c: Coincident(g-3,g2)
    c: Weight(g3) = 1
    c: Coincident(g13,g0)
    c: Equal(g3, g4-g12) x9
    c: Coincident(g13,g2)
    c: InternalAlignment(g3-g12 -> g13) x10
    c: InternalAlignment(g14-g21 -> g13) x8
    c: Coincident(g22,g2)
    c: Vertical(g22)
    c: Coincident(g22,g1)
    c: DistanceY(g22,g22) = 28.54
FEATURE [PartDesign::Pad] Pad009
  Direction = (1,-2e-16,3e-16)
  Length = 10
  Length2 = 10
  Placement = pos=(0,0,0) rot=(1,1,1;2.0944rad)
  Profile = -> Sketch012
  ReferenceAxis = -> Sketch012 [N_Axis]
  Type = 0
FEATURE [PartDesign::Body] Body012  label="WaveLeft"
  Group = -> [Sketch012,Pad009,Binder010]
  Origin = -> Origin012
  Placement = pos=(-33.6897,2.67023,0) rot=(0,0,1;3.01069rad)
  Tip = -> Pad009
FEATURE [Part::Cut] Cut005
  Base = -> Cut004
  Tool = -> Body012
FEATURE [PartDesign::SubShapeBinder] Binder011
  BindCopyOnChange = 0
  BindMode = 0
  ClaimChildren = false
  Context = -> Body013 [Binder011.]
  Fuse = false
  MakeFace = true
  OffsetFill = false
  OffsetIntersection = false
  OffsetJoinType = 0
  OffsetOpenResult = false
  PartialLoad = false
  Relative = true
  Support = -> [Cut005[Face14],Cut006[Face14,Face17]]
  _Version = 2
FEATURE [Sketcher::SketchObject] Sketch013
  ExternalGeometry = -> [Binder011]
  FullyConstrained = false
  MapMode = 5
  Placement = pos=(0,0,0) rot=(0.57735,0.57735,0.57735;2.0944rad)
  Support = -> [YZ_Plane013]
  sketch-geometry (21):
    g0: LineSegment StartX=27.9295 StartY=20.0186 StartZ=0 EndX=32.9295 EndY=20.0186 EndZ=0
    g1: LineSegment StartX=32.9295 StartY=20.0186 StartZ=0 EndX=32.9295 EndY=40.0186 EndZ=0
    g2: LineSegment StartX=32.9295 StartY=40.0186 StartZ=0 EndX=-53.0705 EndY=40.0186 EndZ=0
    g3: LineSegment StartX=-53.0705 StartY=40.0186 StartZ=0 EndX=-53.0705 EndY=23.1665 EndZ=0
    g4: LineSegment StartX=-53.0705 StartY=23.1665 StartZ=0 EndX=-49 EndY=23.1665 EndZ=0
    g5: LineSegment StartX=-49 StartY=23.1665 StartZ=0 EndX=-47.5 EndY=23.2158 EndZ=0
    g6-g13: Circle x8 (B-spline internal-alignment scaffolding for g14; pole/knot coordinates omitted)
    g14: BSplineCurve PolesCount=8 KnotsCount=6 Degree=3 IsPeriodic=0
    g15-g20: GeomPoint x6 (B-spline internal-alignment scaffolding for g14; pole/knot coordinates omitted)
  constraints (22):
    c: Coincident(g0,g-5)
    c: Horizontal(g0)
    c: Coincident(g0,g1)
    c: Vertical(g1)
    c: Coincident(g1,g2)
    c: Horizontal(g2)
    c: Coincident(g2,g3)
    c: Vertical(g3)
    c: Coincident(g3,g4)
    c: Coincident(g4,g-3)
    c: Horizontal(g4)
    c: DistanceX(g0,g0) = 5
    c: DistanceY(g1,g1) = 20
    c: DistanceX(g2,g2) = 86
    c: Coincident(g5,g4)
    c: Coincident(g5,g-4)
    c: Weight(g6) = 1
    c: Coincident(g14,g5)
    c: Equal(g6, g7-g13) x7
    c: InternalAlignment(g6-g13 -> g14) x8
    c: InternalAlignment(g15-g20 -> g14) x6
    c: Coincident(g14,g0)
FEATURE [PartDesign::Pad] Pad010
  Direction = (1,-2e-16,3e-16)
  Length = 20
  Length2 = 10
  Placement = pos=(0,0,0) rot=(1,1,1;2.0944rad)
  Profile = -> Sketch013
  ReferenceAxis = -> Sketch013 [N_Axis]
  Type = 0
FEATURE [PartDesign::Body] Body013  label="WaveRight"
  Group = -> [Sketch013,Binder011,Pad010]
  Origin = -> Origin013
  Placement = pos=(84.75,0,0) rot=(0,0,1;0rad)
  Tip = -> Pad010
FEATURE [PartDesign::SubShapeBinder] Binder012
  BindCopyOnChange = 0
  BindMode = 0
  ClaimChildren = false
  Context = -> Body014 [Binder012.]
  Fuse = false
  MakeFace = true
  OffsetFill = false
  OffsetIntersection = false
  OffsetJoinType = 0
  OffsetOpenResult = false
  PartialLoad = false
  Relative = true
  Support = -> [Cut005[Face19]]
  _Version = 2
FEATURE [Sketcher::SketchObject] Sketch014
  ExternalGeometry = -> [Binder012]
  FullyConstrained = true
  MapMode = 5
  Placement = pos=(0,0,0) rot=(1,0,0;1.5708rad)
  Support = -> [XZ_Plane014]
  sketch-geometry (5):
    g0: LineSegment StartX=28.1063 StartY=20.0186 StartZ=0 EndX=28.1063 EndY=32.3895 EndZ=0
    g1: LineSegment StartX=28.1063 StartY=32.3895 StartZ=0 EndX=-86.0937 EndY=32.3895 EndZ=0
    g2: LineSegment StartX=-86.0937 StartY=20.0186 StartZ=0 EndX=-86.0937 EndY=32.3895 EndZ=0
    g3: LineSegment StartX=27.003 StartY=20.0186 StartZ=0 EndX=28.1063 EndY=20.0186 EndZ=0
    g4: LineSegment StartX=27.003 StartY=20.0186 StartZ=0 EndX=-86.0937 EndY=20.0186 EndZ=0
  constraints (14):
    c: Vertical(g0)
    c: Horizontal(g1)
    c: Coincident(g2,g1)
    c: Vertical(g2)
    c: DistanceX(g0) = 28.1063
    c: DistanceY(g0) = 32.3895
    c: DistanceX(g1) = -86.0937
    c: Coincident(g3,g-3)
    c: Coincident(g3,g0)
    c: Horizontal(g3)
    c: Coincident(g4,g3)
    c: Coincident(g4,g2)
    c: Horizontal(g4)
    c: Coincident(g0,g1)
FEATURE [PartDesign::Pad] Pad011
  Direction = (0,-1,2e-16)
  Length = 25
  Length2 = 10
  Placement = pos=(0,0,0) rot=(1,0,0;1.5708rad)
  Profile = -> Sketch014
  ReferenceAxis = -> Sketch014 [N_Axis]
  Type = 0
FEATURE [PartDesign::Body] Body014  label="WaveBack"
  Group = -> [Sketch014,Binder012,Pad011]
  Origin = -> Origin014
  Placement = pos=(-0.959627,21.9791,0) rot=(0,0,1;3.18523rad)
  Tip = -> Pad011
FEATURE [Part::Cut] Cut006
  Base = -> Cut005
  Tool = -> Body014
FEATURE [Part::Cut] Cut007  label="ShellWavy"
  Base = -> Cut006
  Tool = -> Body013
FEATURE [PartDesign::SubShapeBinder] Binder013
  BindCopyOnChange = 0
  BindMode = 0
  ClaimChildren = false
  Context = -> Body015 [Binder013.]
  Fuse = false
  MakeFace = true
  OffsetFill = false
  OffsetIntersection = false
  OffsetJoinType = 0
  OffsetOpenResult = false
  PartialLoad = false
  Relative = true
  Support = -> [Link014[Face5]]
  _Version = 2
FEATURE [PartDesign::SubShapeBinder] Binder014
  BindCopyOnChange = 0
  BindMode = 0
  ClaimChildren = false
  Context = -> Body015 [Binder014.]
  Fuse = false
  MakeFace = true
  OffsetFill = false
  OffsetIntersection = false
  OffsetJoinType = 0
  OffsetOpenResult = false
  PartialLoad = false
  Relative = true
  Support = -> [Cut[Face121,Face122]]
  _Version = 2
FEATURE [PartDesign::Plane] DatumPlane001
  AttachmentOffset = pos=(0,0,-1) rot=(0,0,1;0rad)
  Length = 142.003
  MapMode = 5
  Placement = pos=(2.15678,9.72862,24.0572) rot=(0.999108,-0.008064,-0.041448;2.75764rad)
  ResizeMode = 0
  Support = -> [Binder014]
  Width = 83.1198
FEATURE [PartDesign::Pad] Pad012
  Direction = (-7.1e-15,1e-16,1)
  Length = 10
  Length2 = 10
  Profile = -> Binder013
  Type = 0
FEATURE [Sketcher::SketchObject] Sketch015
  FullyConstrained = false
  MapMode = 5
  Placement = pos=(2.15678,9.72862,24.0572) rot=(0.999108,-0.008064,-0.041448;2.75764rad)
  Support = -> [DatumPlane001]
  sketch-geometry (4):
    g0: LineSegment StartX=71.9341 StartY=3.84978 StartZ=0 EndX=100.189 EndY=3.84978 EndZ=0
    g1: LineSegment StartX=100.189 StartY=3.84978 StartZ=0 EndX=100.189 EndY=-25.5581 EndZ=0
    g2: LineSegment StartX=100.189 StartY=-25.5581 StartZ=0 EndX=71.9341 EndY=-25.5581 EndZ=0
    g3: LineSegment StartX=71.9341 StartY=-25.5581 StartZ=0 EndX=71.9341 EndY=3.84978 EndZ=0
  constraints (8):
    c: Coincident(g0,g1)
    c: Coincident(g1,g2)
    c: Coincident(g2,g3)
    c: Coincident(g3,g0)
    c: Horizontal(g0)
    c: Horizontal(g2)
    c: Vertical(g1)
    c: Vertical(g3)
FEATURE [PartDesign::Pocket] Pocket
  BaseFeature = -> Pad012
  Direction = (0.0828278,0.373612,0.92388)
  Length = 5
  Length2 = 5
  Profile = -> Sketch015
  ReferenceAxis = -> Sketch015 [N_Axis]
  Type = 1
FEATURE [PartDesign::Body] Body015  label="HeatsetTopRightB"
  Group = -> [Binder013,Binder014,DatumPlane001,Pad012,Sketch015,Pocket]
  Origin = -> Origin015
  Tip = -> Pocket
FEATURE [PartDesign::SubShapeBinder] Binder015
  BindCopyOnChange = 0
  BindMode = 0
  ClaimChildren = false
  Context = -> Body016 [Binder015.]
  Fuse = false
  MakeFace = true
  OffsetFill = false
  OffsetIntersection = false
  OffsetJoinType = 0
  OffsetOpenResult = false
  PartialLoad = false
  Relative = true
  Support = -> [Link017[Face5]]
  _Version = 2
FEATURE [PartDesign::SubShapeBinder] Binder016
  BindCopyOnChange = 0
  BindMode = 0
  ClaimChildren = false
  Context = -> Body016 [Binder016.]
  Fuse = false
  MakeFace = true
  OffsetFill = false
  OffsetIntersection = false
  OffsetJoinType = 0
  OffsetOpenResult = false
  PartialLoad = false
  Relative = true
  Support = -> [Cut[Face43]]
  _Version = 2
FEATURE [PartDesign::Plane] DatumPlane002
  AttachmentOffset = pos=(0,0,-1) rot=(0,0,1;0rad)
  Length = 109.912
  MapMode = 5
  Placement = pos=(-1.19259,-9.05864,22.0582) rot=(0.999676,-0.00493,0.024983;3.53114rad)
  ResizeMode = 0
  Support = -> [Binder016]
  Width = 110.591
FEATURE [PartDesign::Pad] Pad013
  Direction = (0,-7.1e-15,1)
  Length = 10
  Length2 = 10
  Profile = -> Binder015
  Type = 0
FEATURE [Sketcher::SketchObject] Sketch016
  FullyConstrained = false
  MapMode = 5
  Placement = pos=(-1.19259,-9.05864,22.0582) rot=(0.999676,-0.00493,0.024983;3.53114rad)
  Support = -> [DatumPlane002]
  sketch-geometry (4):
    g0: LineSegment StartX=46.0275 StartY=55.406 StartZ=0 EndX=70.6938 EndY=55.406 EndZ=0
    g1: LineSegment StartX=70.6938 StartY=55.406 StartZ=0 EndX=70.6938 EndY=33.1378 EndZ=0
    g2: LineSegment StartX=70.6938 StartY=33.1378 StartZ=0 EndX=46.0275 EndY=33.1378 EndZ=0
    g3: LineSegment StartX=46.0275 StartY=33.1378 StartZ=0 EndX=46.0275 EndY=55.406 EndZ=0
  constraints (8):
    c: Coincident(g0,g1)
    c: Coincident(g1,g2)
    c: Coincident(g2,g3)
    c: Coincident(g3,g0)
    c: Horizontal(g0)
    c: Horizontal(g2)
    c: Vertical(g1)
    c: Vertical(g3)
FEATURE [PartDesign::Pocket] Pocket001
  BaseFeature = -> Pad013
  Direction = (-0.0499502,-0.37941,0.92388)
  Length = 5
  Length2 = 5
  Profile = -> Sketch016
  ReferenceAxis = -> Sketch016 [N_Axis]
  Type = 1
FEATURE [PartDesign::Body] Body016  label="HeatsetBotRightB"
  Group = -> [Binder015,Binder016,DatumPlane002,Pad013,Sketch016,Pocket001]
  Origin = -> Origin016
  Tip = -> Pocket001
FEATURE [PartDesign::SubShapeBinder] Binder017
  BindCopyOnChange = 0
  BindMode = 0
  ClaimChildren = false
  Context = -> Body017 [Binder017.]
  Fuse = false
  MakeFace = true
  OffsetFill = false
  OffsetIntersection = false
  OffsetJoinType = 0
  OffsetOpenResult = false
  PartialLoad = false
  Relative = true
  Support = -> [Link015[Face5]]
  _Version = 2
FEATURE [PartDesign::SubShapeBinder] Binder018
  BindCopyOnChange = 0
  BindMode = 0
  ClaimChildren = false
  Context = -> Body017 [Binder018.]
  Fuse = false
  MakeFace = true
  OffsetFill = false
  OffsetIntersection = false
  OffsetJoinType = 0
  OffsetOpenResult = false
  PartialLoad = false
  Relative = true
  Support = -> [Cut[Face256]]
  _Version = 2
FEATURE [PartDesign::Plane] DatumPlane003
  AttachmentOffset = pos=(0,0,-0.5) rot=(0,0,1;0rad)
  Length = 62.5507
  MapMode = 5
  Placement = pos=(0,10.3934,25.092) rot=(1,0,0;2.74889rad)
  ResizeMode = 0
  Support = -> [Binder018]
  Width = 91.3103
FEATURE [PartDesign::Pad] Pad014
  Direction = (0,3.6e-15,1)
  Length = 10
  Length2 = 10
  Profile = -> Binder017
  Type = 0
FEATURE [Sketcher::SketchObject] Sketch017
  FullyConstrained = false
  MapMode = 5
  Placement = pos=(0,10.3934,25.092) rot=(1,0,0;2.74889rad)
  Support = -> [DatumPlane003]
  sketch-geometry (4):
    g0: LineSegment StartX=-10.4446 StartY=-17.1438 StartZ=0 EndX=9.93344 EndY=-17.1438 EndZ=0
    g1: LineSegment StartX=9.93344 StartY=-17.1438 StartZ=0 EndX=9.93344 EndY=-38.4316 EndZ=0
    g2: LineSegment StartX=9.93344 StartY=-38.4316 StartZ=0 EndX=-10.4446 EndY=-38.4316 EndZ=0
    g3: LineSegment StartX=-10.4446 StartY=-38.4316 StartZ=0 EndX=-10.4446 EndY=-17.1438 EndZ=0
  constraints (8):
    c: Coincident(g0,g1)
    c: Coincident(g1,g2)
    c: Coincident(g2,g3)
    c: Coincident(g3,g0)
    c: Horizontal(g0)
    c: Horizontal(g2)
    c: Vertical(g1)
    c: Vertical(g3)
FEATURE [PartDesign::Pocket] Pocket002
  BaseFeature = -> Pad014
  Direction = (0,0.382683,0.92388)
  Length = 5
  Length2 = 5
  Profile = -> Sketch017
  ReferenceAxis = -> Sketch017 [N_Axis]
  Type = 1
FEATURE [PartDesign::Body] Body017  label="HeatsetTopLeftB"
  Group = -> [Binder017,Binder018,DatumPlane003,Pad014,Sketch017,Pocket002]
  Origin = -> Origin017
  Placement = pos=(0,0,-1) rot=(0,0,1;0rad)
  Tip = -> Pocket002
FEATURE [App::Link] Link019  label="HeatsetBotLeftA"
  LinkPlacement = pos=(-20.75,-24.25,3) rot=(0,0,1;0rad)
  LinkedObject = -> <external HeatsetInserts.FCStd>#Cut003
  Placement = pos=(-20.75,-24.25,3) rot=(0,0,1;0rad)
FEATURE [PartDesign::SubShapeBinder] Binder019
  BindCopyOnChange = 0
  BindMode = 0
  ClaimChildren = false
  Context = -> Body018 [Binder019.]
  Fuse = false
  MakeFace = true
  OffsetFill = false
  OffsetIntersection = false
  OffsetJoinType = 0
  OffsetOpenResult = false
  PartialLoad = false
  Relative = true
  Support = -> [Link019[Face3]]
  _Version = 2
FEATURE [PartDesign::SubShapeBinder] Binder020
  BindCopyOnChange = 0
  BindMode = 0
  ClaimChildren = false
  Context = -> Body018 [Binder020.]
  Fuse = false
  MakeFace = true
  OffsetFill = false
  OffsetIntersection = false
  OffsetJoinType = 0
  OffsetOpenResult = false
  PartialLoad = false
  Relative = true
  Support = -> [Cut[Face10]]
  _Version = 2
FEATURE [PartDesign::Pad] Pad015
  Direction = (0,-3.6e-15,1)
  Length = 10
  Length2 = 10
  Profile = -> Binder019
  Type = 0
FEATURE [PartDesign::Plane] DatumPlane004
  Length = 67.9405
  MapMode = 5
  Placement = pos=(9.64605e-08,0.638829,1.66421) rot=(1,0,0;2.77507rad)
  ResizeMode = 0
  Support = -> [Binder020]
  Width = 82.1551
FEATURE [Sketcher::SketchObject] Sketch018
  FullyConstrained = false
  MapMode = 5
  Placement = pos=(9.64605e-08,0.638829,1.66421) rot=(1,0,0;2.77507rad)
  Support = -> [DatumPlane004]
  sketch-geometry (4):
    g0: LineSegment StartX=-31.4694 StartY=34.0482 StartZ=0 EndX=-9.71055 EndY=34.0482 EndZ=0
    g1: LineSegment StartX=-9.71055 StartY=34.0482 StartZ=0 EndX=-9.71055 EndY=12.4986 EndZ=0
    g2: LineSegment StartX=-9.71055 StartY=12.4986 StartZ=0 EndX=-31.4694 EndY=12.4986 EndZ=0
    g3: LineSegment StartX=-31.4694 StartY=12.4986 StartZ=0 EndX=-31.4694 EndY=34.0482 EndZ=0
  constraints (8):
    c: Coincident(g0,g1)
    c: Coincident(g1,g2)
    c: Coincident(g2,g3)
    c: Coincident(g3,g0)
    c: Horizontal(g0)
    c: Horizontal(g2)
    c: Vertical(g1)
    c: Vertical(g3)
FEATURE [PartDesign::Pocket] Pocket003
  BaseFeature = -> Pad015
  Direction = (5.41121e-08,0.358368,0.93358)
  Length = 5
  Length2 = 5
  Profile = -> Sketch018
  ReferenceAxis = -> Sketch018 [N_Axis]
  Type = 1
FEATURE [PartDesign::Body] Body018  label="HeatsetBotLeftB"
  Group = -> [Binder019,Binder020,Pad015,DatumPlane004,Sketch018,Pocket003]
  Origin = -> Origin018
  Tip = -> Pocket003
FEATURE [Part::MultiFuse] Fusion002  label="HeatsetBotLeftF"
  Refine = true
  Shapes = -> [Link019,Body018]
FEATURE [Part::MultiFuse] Fusion003  label="HeatsetTopLeftF"
  Refine = true
  Shapes = -> [Body017,Link015]
FEATURE [Part::MultiFuse] Fusion004  label="HeatsetBotRightF"
  Refine = true
  Shapes = -> [Body016,Link017]
FEATURE [Part::MultiFuse] Fusion005  label="HeatsetTopRightF"
  Refine = true
  Shapes = -> [Body015,Link014]
FEATURE [App::DocumentObjectGroup] Group002  label="Heatsets"
  Group = -> [Fusion002,Fusion003,Fusion004,Fusion005]
FEATURE [Sketcher::SketchObject] Sketch019
  FullyConstrained = false
  MapMode = 5
  Support = -> [XY_Plane019]
  sketch-geometry (4):
    g0: GeomPoint X=-20.7484 Y=-24.2516 Z=0
    g1: GeomPoint X=55.1532 Y=-49.1265 Z=0
    g2: GeomPoint X=85.2491 Y=15.947 Z=0
    g3: GeomPoint X=-0.005864 Y=33.4906 Z=0
FEATURE [PartDesign::Body] Body019  label="BodyForScrews"
  Group = -> [Sketch019]
  Origin = -> Origin019
FEATURE [App::Link] Link020  label="PlateWithHolesN"
  LinkPlacement = pos=(0,0,-2.6) rot=(0,0,1;0rad)
  LinkedObject = -> <external PlateBottom.FCStd>#Cut001
  Placement = pos=(0,0,-2.6) rot=(0,0,1;0rad)
FEATURE [PartDesign::SubShapeBinder] Binder021
  BindCopyOnChange = 0
  BindMode = 0
  ClaimChildren = false
  Context = -> Body020 [Binder021.]
  Fuse = false
  MakeFace = true
  OffsetFill = false
  OffsetIntersection = false
  OffsetJoinType = 0
  OffsetOpenResult = false
  PartialLoad = false
  Relative = true
  Support = -> [Cut007[Face2]]
  _Version = 2
FEATURE [PartDesign::Pad] Pad016
  Direction = (0,0,-1)
  Length = 2.6
  Length2 = 10
  Profile = -> Binder021
  Type = 0
FEATURE [PartDesign::Body] Body020  label="ShellSkirt"
  Group = -> [Binder021,Pad016]
  Origin = -> Origin020
  Tip = -> Pad016
FEATURE [Part::MultiFuse] Fusion006  label="ShellWithSkirt"
  Shapes = -> [Cut007,Body020]
FEATURE [Part::MultiFuse] Fusion007  label="ShellWithHolders"
  Shapes = -> [Fusion006,Body007,Body008]
FEATURE [Part::Compound] Compound006  label="PartCutterC"
  Links = -> [Link012,Link013]
FEATURE [Part::Cut] Cut008  label="ShellWithParts"
  Base = -> Fusion007
  Tool = -> Compound006
FEATURE [Part::MultiFuse] Fusion008  label="CaseWithColumns"
  Refine = true
  Shapes = -> [Cut008,Cut,Cut003]
FEATURE [Part::Compound] Compound007  label="HeatsetC"
  Links = -> [Fusion002,Fusion003,Fusion004,Fusion005]
FEATURE [Part::MultiFuse] Fusion009  label="CaseWithHeatsets"
  Refine = true
  Shapes = -> [Fusion008,Compound007]

RESOLVED EXTERNAL PARTS (link-assembly join: the EXTERNAL_REF files above that resolve inside this repo's crawl, each included once):
---- part ../components/MX_Switches.FCStd = doc fcstd_fbf47cda5fe2 ----
FCSTD DOCUMENT  (FreeCAD 0.21R33668 +26 (Git))
Label: MX_Switches
License: All rights reserved
LicenseURL: http://en.wikipedia.org/wiki/All_rights_reserved
objects: Sketcher::SketchObject×45, PartDesign::Pad×15, PartDesign::AdditiveLoft×15, PartDesign::Plane×10, PartDesign::Body×5, Part::Refine×2
note: 122 computed .brp shape members not serialized (recipe doc carries the construction recipe); baked Part::Feature solids carry a one-line shape summary decoded from their .brp

FEATURE [Sketcher::SketchObject] Sketch014
  FullyConstrained = true
  MapMode = 5
  Support = -> [XY_Plane003]
  sketch-geometry (4):
    g0: LineSegment StartX=-7.8 StartY=7.8 StartZ=0 EndX=7.8 EndY=7.8 EndZ=0
    g1: LineSegment StartX=7.8 StartY=7.8 StartZ=0 EndX=7.8 EndY=-7.8 EndZ=0
    g2: LineSegment StartX=7.8 StartY=-7.8 StartZ=0 EndX=-7.8 EndY=-7.8 EndZ=0
    g3: LineSegment StartX=-7.8 StartY=-7.8 StartZ=0 EndX=-7.8 EndY=7.8 EndZ=0
  constraints (11):
    c: Coincident(g0,g1)
    c: Coincident(g1,g2)
    c: Coincident(g2,g3)
    c: Coincident(g3,g0)
    c: Horizontal(g0)
    c: Horizontal(g2)
    c: Vertical(g1)
    c: Vertical(g3)
    c: DistanceX(g0,g0) = 15.6
    c: Equal(g0,g3)
    c: Symmetric(g0,g1,g-1)
FEATURE [PartDesign::Pad] Pad003
  Direction = (0,0,1)
  Length = 1
  Length2 = 100
  Profile = -> Sketch014
  Refine = true
  Type = 0
FEATURE [Sketcher::SketchObject] Sketch015
  FullyConstrained = true
  MapMode = 5
  Support = -> [XY_Plane003]
  sketch-geometry (4):
    g0: LineSegment StartX=-7 StartY=7 StartZ=0 EndX=7 EndY=7 EndZ=0
    g1: LineSegment StartX=7 StartY=7 StartZ=0 EndX=7 EndY=-7 EndZ=0
    g2: LineSegment StartX=7 StartY=-7 StartZ=0 EndX=-7 EndY=-7 EndZ=0
    g3: LineSegment StartX=-7 StartY=-7 StartZ=0 EndX=-7 EndY=7 EndZ=0
  constraints (11):
    c: Coincident(g0,g1)
    c: Coincident(g1,g2)
    c: Coincident(g2,g3)
    c: Coincident(g3,g0)
    c: Horizontal(g0)
    c: Horizontal(g2)
    c: Vertical(g1)
    c: Vertical(g3)
    c: Symmetric(g0,g1,g-1)
    c: Equal(g0,g3)
    c: DistanceX(g0,g0) = 14
FEATURE [PartDesign::Pad] Pad004
  BaseFeature = -> Pad003
  Direction = (0,0,1)
  Length = 2.5
  Length2 = 100
  Profile = -> Sketch015
  Refine = true
  Reversed = true
  Type = 0
FEATURE [PartDesign::Plane] DatumPlane001
  Length = 60
  MapMode = 5
  Placement = pos=(0,0,-2.5) rot=(1,0,0;3.14159rad)
  ResizeMode = 0
  Support = -> [Pad004]
  Width = 60
FEATURE [Sketcher::SketchObject] Sketch016
  AttachmentOffset = pos=(0,0,2.5) rot=(0,0,1;0rad)
  FullyConstrained = true
  MapMode = 5
  Placement = pos=(0,0,-5) rot=(1,0,0;3.14159rad)
  Support = -> [DatumPlane001]
  sketch-geometry (4):
    g0: LineSegment StartX=-5 StartY=5 StartZ=0 EndX=5 EndY=5 EndZ=0
    g1: LineSegment StartX=5 StartY=5 StartZ=0 EndX=5 EndY=-5 EndZ=0
    g2: LineSegment StartX=5 StartY=-5 StartZ=0 EndX=-5 EndY=-5 EndZ=0
    g3: LineSegment StartX=-5 StartY=-5 StartZ=0 EndX=-5 EndY=5 EndZ=0
  constraints (11):
    c: Coincident(g0,g1)
    c: Coincident(g1,g2)
    c: Coincident(g2,g3)
    c: Coincident(g3,g0)
    c: Horizontal(g0)
    c: Horizontal(g2)
    c: Vertical(g1)
    c: Vertical(g3)
    c: DistanceX(g0,g0) = 10
    c: Equal(g0,g3)
    c: Symmetric(g0,g1,g-1)
FEATURE [Sketcher::SketchObject] Sketch006
  FullyConstrained = true
  MapMode = 5
  Placement = pos=(0,0,-2.5) rot=(1,0,0;3.14159rad)
  Support = -> [DatumPlane001]
  sketch-geometry (4):
    g0: LineSegment StartX=-7 StartY=7 StartZ=0 EndX=7 EndY=7 EndZ=0
    g1: LineSegment StartX=7 StartY=7 StartZ=0 EndX=7 EndY=-7 EndZ=0
    g2: LineSegment StartX=7 StartY=-7 StartZ=0 EndX=-7 EndY=-7 EndZ=0
    g3: LineSegment StartX=-7 StartY=-7 StartZ=0 EndX=-7 EndY=7 EndZ=0
  constraints (11):
    c: Coincident(g0,g1)
    c: Coincident(g1,g2)
    c: Coincident(g2,g3)
    c: Coincident(g3,g0)
    c: Horizontal(g0)
    c: Horizontal(g2)
    c: Vertical(g1)
    c: Vertical(g3)
    c: Equal(g0,g3)
    c: DistanceX(g0,g0) = 14
    c: Symmetric(g0,g1,g-1)
FEATURE [PartDesign::AdditiveLoft] AdditiveLoft
  BaseFeature = -> Pad004
  Closed = false
  Profile = -> Sketch016
  Refine = true
  Ruled = false
  Sections = -> [Sketch006]
FEATURE [PartDesign::Plane] DatumPlane002
  Length = 60
  MapMode = 5
  Placement = pos=(0,0,-5) rot=(1,0,0;3.14159rad)
  ResizeMode = 0
  Support = -> [AdditiveLoft]
  Width = 60
FEATURE [Sketcher::SketchObject] Sketch007
  FullyConstrained = true
  MapMode = 5
  Placement = pos=(0,0,-5) rot=(1,0,0;3.14159rad)
  Support = -> [DatumPlane002]
  sketch-geometry (1):
    g0: Circle CenterX=0 CenterY=0 CenterZ=0 NormalX=0 NormalY=0 NormalZ=1 AngleXU=0 Radius=4
  constraints (2):
    c: Coincident(g0,g-1)
    c: Radius(g0) = 4
FEATURE [PartDesign::Pad] Pad005
  BaseFeature = -> AdditiveLoft
  Direction = (0,0,-1)
  Length = 3.3
  Length2 = 100
  Profile = -> Sketch007
  Refine = true
  Type = 0
FEATURE [Sketcher::SketchObject] Sketch017
  FullyConstrained = true
  MapMode = 5
  Placement = pos=(0,0,1) rot=(0,0,1;0rad)
  sketch-geometry (4):
    g0: LineSegment StartX=-7 StartY=7 StartZ=0 EndX=7 EndY=7 EndZ=0
    g1: LineSegment StartX=7 StartY=7 StartZ=0 EndX=7 EndY=-7 EndZ=0
    g2: LineSegment StartX=7 StartY=-7 StartZ=0 EndX=-7 EndY=-7 EndZ=0
    g3: LineSegment StartX=-7 StartY=-7 StartZ=0 EndX=-7 EndY=7 EndZ=0
  constraints (11):
    c: Coincident(g0,g1)
    c: Coincident(g1,g2)
    c: Coincident(g2,g3)
    c: Coincident(g3,g0)
    c: Horizontal(g0)
    c: Horizontal(g2)
    c: Vertical(g1)
    c: Vertical(g3)
    c: Symmetric(g0,g1,g-1)
    c: Equal(g0,g3)
    c: DistanceX(g0,g0) = 14
FEATURE [Sketcher::SketchObject] Sketch018
  AttachmentOffset = pos=(0,0,5.6) rot=(0,0,1;0rad)
  FullyConstrained = true
  MapMode = 5
  Placement = pos=(0,0,6.6) rot=(0,0,1;0rad)
  expr: .AttachmentOffset.Base.z = 11.6 - 5 - 1
  sketch-geometry (4):
    g0: LineSegment StartX=-4 StartY=4 StartZ=0 EndX=4 EndY=4 EndZ=0
    g1: LineSegment StartX=4 StartY=4 StartZ=0 EndX=4 EndY=-4 EndZ=0
    g2: LineSegment StartX=4 StartY=-4 StartZ=0 EndX=-4 EndY=-4 EndZ=0
    g3: LineSegment StartX=-4 StartY=-4 StartZ=0 EndX=-4 EndY=4 EndZ=0
  constraints (11):
    c: Coincident(g0,g1)
    c: Coincident(g1,g2)
    c: Coincident(g2,g3)
    c: Coincident(g3,g0)
    c: Horizontal(g0)
    c: Horizontal(g2)
    c: Vertical(g1)
    c: Vertical(g3)
    c: Equal(g0,g3)
    c: Symmetric(g0,g1,g-1)
    c: DistanceX(g0,g0) = 8
FEATURE [PartDesign::AdditiveLoft] AdditiveLoft001
  BaseFeature = -> Pad005
  Closed = false
  Profile = -> Sketch017
  Refine = true
  Ruled = false
  Sections = -> [Sketch018]
FEATURE [Sketcher::SketchObject] Sketch019
  AttachmentOffset = pos=(0,0,16) rot=(0,0,1;0rad)
  FullyConstrained = true
  MapMode = 5
  Placement = pos=(0,0,17) rot=(0,0,1;0rad)
  sketch-geometry (4):
    g0: LineSegment StartX=-6.185 StartY=6.185 StartZ=0 EndX=6.185 EndY=6.185 EndZ=0
    g1: LineSegment StartX=6.185 StartY=6.185 StartZ=0 EndX=6.185 EndY=-6.185 EndZ=0
    g2: LineSegment StartX=6.185 StartY=-6.185 StartZ=0 EndX=-6.185 EndY=-6.185 EndZ=0
    g3: LineSegment StartX=-6.185 StartY=-6.185 StartZ=0 EndX=-6.185 EndY=6.185 EndZ=0
  constraints (11):
    c: Coincident(g0,g1)
    c: Coincident(g1,g2)
    c: Coincident(g2,g3)
    c: Coincident(g3,g0)
    c: Horizontal(g0)
    c: Horizontal(g2)
    c: Vertical(g1)
    c: Vertical(g3)
    c: DistanceX(g0,g0) = 12.37
    c: Equal(g0,g3)
    c: Symmetric(g0,g1,g-1)
FEATURE [Sketcher::SketchObject] Sketch020
  AttachmentOffset = pos=(0,0,4.61) rot=(0,0,1;0rad)
  FullyConstrained = true
  MapMode = 5
  Placement = pos=(0,0,5.61) rot=(0,0,1;0rad)
  expr: .AttachmentOffset.Base.z = 16 - 9.39 - 2
  sketch-geometry (4):
    g0: LineSegment StartX=-9.05 StartY=9.05 StartZ=0 EndX=9.05 EndY=9.05 EndZ=0
    g1: LineSegment StartX=9.05 StartY=9.05 StartZ=0 EndX=9.05 EndY=-9.05 EndZ=0
    g2: LineSegment StartX=9.05 StartY=-9.05 StartZ=0 EndX=-9.05 EndY=-9.05 EndZ=0
    g3: LineSegment StartX=-9.05 StartY=-9.05 StartZ=0 EndX=-9.05 EndY=9.05 EndZ=0
  constraints (11):
    c: Coincident(g0,g1)
    c: Coincident(g1,g2)
    c: Coincident(g2,g3)
    c: Coincident(g3,g0)
    c: Horizontal(g0)
    c: Horizontal(g2)
    c: Vertical(g1)
    c: Vertical(g3)
    c: DistanceX(g0,g0) = 18.1
    c: Equal(g0,g3)
    c: Symmetric(g0,g1,g-1)
FEATURE [PartDesign::AdditiveLoft] AdditiveLoft002
  BaseFeature = -> AdditiveLoft001
  Closed = false
  Profile = -> Sketch019
  Refine = true
  Ruled = false
  Sections = -> [Sketch020]
FEATURE [PartDesign::Body] Body003  label="MXSwitch100"
  Group = -> [Sketch014,Pad003,Sketch015,Pad004,DatumPlane001,Sketch016,Sketch006,AdditiveLoft,DatumPlane002,Sketch007,Pad005,Sketch017,Sketch018,AdditiveLoft001,Sketch019,Sketch020,AdditiveLoft002]
  Origin = -> Origin003
  Tip = -> AdditiveLoft002
FEATURE [Sketcher::SketchObject] Sketch023
  FullyConstrained = true
  MapMode = 5
  Support = -> [XY_Plane004]
  sketch-geometry (4):
    g0: LineSegment StartX=-7.8 StartY=7.8 StartZ=0 EndX=7.8 EndY=7.8 EndZ=0
    g1: LineSegment StartX=7.8 StartY=7.8 StartZ=0 EndX=7.8 EndY=-7.8 EndZ=0
    g2: LineSegment StartX=7.8 StartY=-7.8 StartZ=0 EndX=-7.8 EndY=-7.8 EndZ=0
    g3: LineSegment StartX=-7.8 StartY=-7.8 StartZ=0 EndX=-7.8 EndY=7.8 EndZ=0
  constraints (11):
    c: Coincident(g0,g1)
    c: Coincident(g1,g2)
    c: Coincident(g2,g3)
    c: Coincident(g3,g0)
    c: Horizontal(g0)
    c: Horizontal(g2)
    c: Vertical(g1)
    c: Vertical(g3)
    c: DistanceX(g0,g0) = 15.6
    c: Equal(g0,g3)
    c: Symmetric(g0,g1,g-1)
FEATURE [PartDesign::Pad] Pad006
  Direction = (0,0,1)
  Length = 1
  Length2 = 100
  Profile = -> Sketch023
  Refine = true
  Type = 0
FEATURE [Sketcher::SketchObject] Sketch024
  FullyConstrained = true
  MapMode = 5
  Support = -> [XY_Plane004]
  sketch-geometry (4):
    g0: LineSegment StartX=-7 StartY=7 StartZ=0 EndX=7 EndY=7 EndZ=0
    g1: LineSegment StartX=7 StartY=7 StartZ=0 EndX=7 EndY=-7 EndZ=0
    g2: LineSegment StartX=7 StartY=-7 StartZ=0 EndX=-7 EndY=-7 EndZ=0
    g3: LineSegment StartX=-7 StartY=-7 StartZ=0 EndX=-7 EndY=7 EndZ=0
  constraints (11):
    c: Coincident(g0,g1)
    c: Coincident(g1,g2)
    c: Coincident(g2,g3)
    c: Coincident(g3,g0)
    c: Horizontal(g0)
    c: Horizontal(g2)
    c: Vertical(g1)
    c: Vertical(g3)
    c: Symmetric(g0,g1,g-1)
    c: Equal(g0,g3)
    c: DistanceX(g0,g0) = 14
FEATURE [PartDesign::Pad] Pad007
  BaseFeature = -> Pad006
  Direction = (0,0,1)
  Length = 2.5
  Length2 = 100
  Profile = -> Sketch024
  Refine = true
  Reversed = true
  Type = 0
FEATURE [PartDesign::Plane] DatumPlane004
  Length = 60
  MapMode = 5
  Placement = pos=(0,0,-2.5) rot=(1,0,0;3.14159rad)
  ResizeMode = 0
  Support = -> [Pad007]
  Width = 60
FEATURE [Sketcher::SketchObject] Sketch021
  FullyConstrained = true
  MapMode = 5
  Placement = pos=(0,0,-2.5) rot=(1,0,0;3.14159rad)
  Support = -> [DatumPlane004]
  sketch-geometry (4):
    g0: LineSegment StartX=-7 StartY=7 StartZ=0 EndX=7 EndY=7 EndZ=0
    g1: LineSegment StartX=7 StartY=7 StartZ=0 EndX=7 EndY=-7 EndZ=0
    g2: LineSegment StartX=7 StartY=-7 StartZ=0 EndX=-7 EndY=-7 EndZ=0
    g3: LineSegment StartX=-7 StartY=-7 StartZ=0 EndX=-7 EndY=7 EndZ=0
  constraints (11):
    c: Coincident(g0,g1)
    c: Coincident(g1,g2)
    c: Coincident(g2,g3)
    c: Coincident(g3,g0)
    c: Horizontal(g0)
    c: Horizontal(g2)
    c: Vertical(g1)
    c: Vertical(g3)
    c: Equal(g0,g3)
    c: DistanceX(g0,g0) = 14
    c: Symmetric(g0,g1,g-1)
FEATURE [Sketcher::SketchObject] Sketch025
  AttachmentOffset = pos=(0,0,2.5) rot=(0,0,1;0rad)
  FullyConstrained = true
  MapMode = 5
  Placement = pos=(0,0,-5) rot=(1,0,0;3.14159rad)
  Support = -> [DatumPlane004]
  sketch-geometry (4):
    g0: LineSegment StartX=-5 StartY=5 StartZ=0 EndX=5 EndY=5 EndZ=0
    g1: LineSegment StartX=5 StartY=5 StartZ=0 EndX=5 EndY=-5 EndZ=0
    g2: LineSegment StartX=5 StartY=-5 StartZ=0 EndX=-5 EndY=-5 EndZ=0
    g3: LineSegment StartX=-5 StartY=-5 StartZ=0 EndX=-5 EndY=5 EndZ=0
  constraints (11):
    c: Coincident(g0,g1)
    c: Coincident(g1,g2)
    c: Coincident(g2,g3)
    c: Coincident(g3,g0)
    c: Horizontal(g0)
    c: Horizontal(g2)
    c: Vertical(g1)
    c: Vertical(g3)
    c: DistanceX(g0,g0) = 10
    c: Equal(g0,g3)
    c: Symmetric(g0,g1,g-1)
FEATURE [PartDesign::AdditiveLoft] AdditiveLoft003
  BaseFeature = -> Pad007
  Closed = false
  Profile = -> Sketch025
  Refine = true
  Ruled = false
  Sections = -> [Sketch021]
FEATURE [PartDesign::Plane] DatumPlane005
  Length = 60
  MapMode = 5
  Placement = pos=(0,0,-5) rot=(1,0,0;3.14159rad)
  ResizeMode = 0
  Support = -> [AdditiveLoft003]
  Width = 60
FEATURE [Sketcher::SketchObject] Sketch022
  FullyConstrained = true
  MapMode = 5
  Placement = pos=(0,0,-5) rot=(1,0,0;3.14159rad)
  Support = -> [DatumPlane005]
  sketch-geometry (1):
    g0: Circle CenterX=0 CenterY=0 CenterZ=0 NormalX=0 NormalY=0 NormalZ=1 AngleXU=0 Radius=4
  constraints (2):
    c: Coincident(g0,g-1)
    c: Radius(g0) = 4
FEATURE [PartDesign::Pad] Pad008
  BaseFeature = -> AdditiveLoft003
  Direction = (0,0,-1)
  Length = 3.3
  Length2 = 100
  Profile = -> Sketch022
  Refine = true
  Type = 0
FEATURE [Sketcher::SketchObject] Sketch026
  FullyConstrained = true
  MapMode = 5
  Placement = pos=(0,0,1) rot=(0,0,1;0rad)
  sketch-geometry (4):
    g0: LineSegment StartX=-7 StartY=7 StartZ=0 EndX=7 EndY=7 EndZ=0
    g1: LineSegment StartX=7 StartY=7 StartZ=0 EndX=7 EndY=-7 EndZ=0
    g2: LineSegment StartX=7 StartY=-7 StartZ=0 EndX=-7 EndY=-7 EndZ=0
    g3: LineSegment StartX=-7 StartY=-7 StartZ=0 EndX=-7 EndY=7 EndZ=0
  constraints (11):
    c: Coincident(g0,g1)
    c: Coincident(g1,g2)
    c: Coincident(g2,g3)
    c: Coincident(g3,g0)
    c: Horizontal(g0)
    c: Horizontal(g2)
    c: Vertical(g1)
    c: Vertical(g3)
    c: Symmetric(g0,g1,g-1)
    c: Equal(g0,g3)
    c: DistanceX(g0,g0) = 14
FEATURE [Sketcher::SketchObject] Sketch027
  AttachmentOffset = pos=(0,0,5.6) rot=(0,0,1;0rad)
  FullyConstrained = true
  MapMode = 5
  Placement = pos=(0,0,6.6) rot=(0,0,1;0rad)
  expr: .AttachmentOffset.Base.z = 11.6 - 5 - 1
  sketch-geometry (4):
    g0: LineSegment StartX=-4 StartY=4 StartZ=0 EndX=4 EndY=4 EndZ=0
    g1: LineSegment StartX=4 StartY=4 StartZ=0 EndX=4 EndY=-4 EndZ=0
    g2: LineSegment StartX=4 StartY=-4 StartZ=0 EndX=-4 EndY=-4 EndZ=0
    g3: LineSegment StartX=-4 StartY=-4 StartZ=0 EndX=-4 EndY=4 EndZ=0
  constraints (11):
    c: Coincident(g0,g1)
    c: Coincident(g1,g2)
    c: Coincident(g2,g3)
    c: Coincident(g3,g0)
    c: Horizontal(g0)
    c: Horizontal(g2)
    c: Vertical(g1)
    c: Vertical(g3)
    c: Equal(g0,g3)
    c: Symmetric(g0,g1,g-1)
    c: DistanceX(g0,g0) = 8
FEATURE [PartDesign::AdditiveLoft] AdditiveLoft004
  BaseFeature = -> Pad008
  Closed = false
  Profile = -> Sketch026
  Refine = true
  Ruled = false
  Sections = -> [Sketch027]
FEATURE [Sketcher::SketchObject] Sketch028
  AttachmentOffset = pos=(0,0,16) rot=(0,0,1;0rad)
  FullyConstrained = true
  MapMode = 5
  Placement = pos=(0,0,17) rot=(0,0,1;0rad)
  expr: Constraints[8] = 12.37 mm * 1.25
  sketch-geometry (4):
    g0: LineSegment StartX=-7.73125 StartY=6.185 StartZ=0 EndX=7.73125 EndY=6.185 EndZ=0
    g1: LineSegment StartX=7.73125 StartY=6.185 StartZ=0 EndX=7.73125 EndY=-6.185 EndZ=0
    g2: LineSegment StartX=7.73125 StartY=-6.185 StartZ=0 EndX=-7.73125 EndY=-6.185 EndZ=0
    g3: LineSegment StartX=-7.73125 StartY=-6.185 StartZ=0 EndX=-7.73125 EndY=6.185 EndZ=0
  constraints (11):
    c: Coincident(g0,g1)
    c: Coincident(g1,g2)
    c: Coincident(g2,g3)
    c: Coincident(g3,g0)
    c: Horizontal(g0)
    c: Horizontal(g2)
    c: Vertical(g1)
    c: Vertical(g3)
    c: DistanceX(g0,g0) = 15.4625
    c: Symmetric(g0,g1,g-1)
    c: DistanceY(g1,g1) = 12.37
FEATURE [Sketcher::SketchObject] Sketch029
  AttachmentOffset = pos=(0,0,4.61) rot=(0,0,1;0rad)
  FullyConstrained = true
  MapMode = 5
  Placement = pos=(0,0,5.61) rot=(0,0,1;0rad)
  expr: .AttachmentOffset.Base.z = 16 - 9.39 - 2
  expr: Constraints[8] = 18.1 mm * 1.25
  sketch-geometry (4):
    g0: LineSegment StartX=-11.3125 StartY=9.05 StartZ=0 EndX=11.3125 EndY=9.05 EndZ=0
    g1: LineSegment StartX=11.3125 StartY=9.05 StartZ=0 EndX=11.3125 EndY=-9.05 EndZ=0
    g2: LineSegment StartX=11.3125 StartY=-9.05 StartZ=0 EndX=-11.3125 EndY=-9.05 EndZ=0
    g3: LineSegment StartX=-11.3125 StartY=-9.05 StartZ=0 EndX=-11.3125 EndY=9.05 EndZ=0
  constraints (11):
    c: Coincident(g0,g1)
    c: Coincident(g1,g2)
    c: Coincident(g2,g3)
    c: Coincident(g3,g0)
    c: Horizontal(g0)
    c: Horizontal(g2)
    c: Vertical(g1)
    c: Vertical(g3)
    c: DistanceX(g0,g0) = 22.625
    c: Symmetric(g0,g1,g-1)
    c: DistanceY(g1,g1) = 18.1
FEATURE [PartDesign::AdditiveLoft] AdditiveLoft005
  BaseFeature = -> AdditiveLoft004
  Closed = false
  Profile = -> Sketch028
  Refine = true
  Ruled = false
  Sections = -> [Sketch029]
FEATURE [PartDesign::Body] Body004  label="MXSwitch125"
  Group = -> [Sketch023,Pad006,Sketch024,Pad007,DatumPlane004,Sketch025,Sketch021,AdditiveLoft003,DatumPlane005,Sketch022,Pad008,Sketch026,Sketch027,AdditiveLoft004,Sketch028,Sketch029,AdditiveLoft005]
  Origin = -> Origin004
  Tip = -> AdditiveLoft005
FEATURE [Sketcher::SketchObject] Sketch032
  FullyConstrained = true
  MapMode = 5
  Support = -> [XY_Plane005]
  sketch-geometry (4):
    g0: LineSegment StartX=-7.8 StartY=7.8 StartZ=0 EndX=7.8 EndY=7.8 EndZ=0
    g1: LineSegment StartX=7.8 StartY=7.8 StartZ=0 EndX=7.8 EndY=-7.8 EndZ=0
    g2: LineSegment StartX=7.8 StartY=-7.8 StartZ=0 EndX=-7.8 EndY=-7.8 EndZ=0
    g3: LineSegment StartX=-7.8 StartY=-7.8 StartZ=0 EndX=-7.8 EndY=7.8 EndZ=0
  constraints (11):
    c: Coincident(g0,g1)
    c: Coincident(g1,g2)
    c: Coincident(g2,g3)
    c: Coincident(g3,g0)
    c: Horizontal(g0)
    c: Horizontal(g2)
    c: Vertical(g1)
    c: Vertical(g3)
    c: DistanceX(g0,g0) = 15.6
    c: Equal(g0,g3)
    c: Symmetric(g0,g1,g-1)
FEATURE [PartDesign::Pad] Pad009
  Direction = (0,0,1)
  Length = 1
  Length2 = 100
  Profile = -> Sketch032
  Refine = true
  Type = 0
FEATURE [Sketcher::SketchObject] Sketch033
  FullyConstrained = true
  MapMode = 5
  Support = -> [XY_Plane005]
  sketch-geometry (4):
    g0: LineSegment StartX=-7 StartY=7 StartZ=0 EndX=7 EndY=7 EndZ=0
    g1: LineSegment StartX=7 StartY=7 StartZ=0 EndX=7 EndY=-7 EndZ=0
    g2: LineSegment StartX=7 StartY=-7 StartZ=0 EndX=-7 EndY=-7 EndZ=0
    g3: LineSegment StartX=-7 StartY=-7 StartZ=0 EndX=-7 EndY=7 EndZ=0
  constraints (11):
    c: Coincident(g0,g1)
    c: Coincident(g1,g2)
    c: Coincident(g2,g3)
    c: Coincident(g3,g0)
    c: Horizontal(g0)
    c: Horizontal(g2)
    c: Vertical(g1)
    c: Vertical(g3)
    c: Symmetric(g0,g1,g-1)
    c: Equal(g0,g3)
    c: DistanceX(g0,g0) = 14
FEATURE [PartDesign::Pad] Pad010
  BaseFeature = -> Pad009
  Direction = (0,0,1)
  Length = 2.5
  Length2 = 100
  Profile = -> Sketch033
  Refine = true
  Reversed = true
  Type = 0
FEATURE [PartDesign::Plane] DatumPlane007
  Length = 60
  MapMode = 5
  Placement = pos=(0,0,-2.5) rot=(1,0,0;3.14159rad)
  ResizeMode = 0
  Support = -> [Pad010]
  Width = 60
FEATURE [Sketcher::SketchObject] Sketch030
  FullyConstrained = true
  MapMode = 5
  Placement = pos=(0,0,-2.5) rot=(1,0,0;3.14159rad)
  Support = -> [DatumPlane007]
  sketch-geometry (4):
    g0: LineSegment StartX=-7 StartY=7 StartZ=0 EndX=7 EndY=7 EndZ=0
    g1: LineSegment StartX=7 StartY=7 StartZ=0 EndX=7 EndY=-7 EndZ=0
    g2: LineSegment StartX=7 StartY=-7 StartZ=0 EndX=-7 EndY=-7 EndZ=0
    g3: LineSegment StartX=-7 StartY=-7 StartZ=0 EndX=-7 EndY=7 EndZ=0
  constraints (11):
    c: Coincident(g0,g1)
    c: Coincident(g1,g2)
    c: Coincident(g2,g3)
    c: Coincident(g3,g0)
    c: Horizontal(g0)
    c: Horizontal(g2)
    c: Vertical(g1)
    c: Vertical(g3)
    c: Equal(g0,g3)
    c: DistanceX(g0,g0) = 14
    c: Symmetric(g0,g1,g-1)
FEATURE [Sketcher::SketchObject] Sketch034
  AttachmentOffset = pos=(0,0,2.5) rot=(0,0,1;0rad)
  FullyConstrained = true
  MapMode = 5
  Placement = pos=(0,0,-5) rot=(1,0,0;3.14159rad)
  Support = -> [DatumPlane007]
  sketch-geometry (4):
    g0: LineSegment StartX=-5 StartY=5 StartZ=0 EndX=5 EndY=5 EndZ=0
    g1: LineSegment StartX=5 StartY=5 StartZ=0 EndX=5 EndY=-5 EndZ=0
    g2: LineSegment StartX=5 StartY=-5 StartZ=0 EndX=-5 EndY=-5 EndZ=0
    g3: LineSegment StartX=-5 StartY=-5 StartZ=0 EndX=-5 EndY=5 EndZ=0
  constraints (11):
    c: Coincident(g0,g1)
    c: Coincident(g1,g2)
    c: Coincident(g2,g3)
    c: Coincident(g3,g0)
    c: Horizontal(g0)
    c: Horizontal(g2)
    c: Vertical(g1)
    c: Vertical(g3)
    c: DistanceX(g0,g0) = 10
    c: Equal(g0,g3)
    c: Symmetric(g0,g1,g-1)
FEATURE [PartDesign::AdditiveLoft] AdditiveLoft006
  BaseFeature = -> Pad010
  Closed = false
  Profile = -> Sketch034
  Refine = true
  Ruled = false
  Sections = -> [Sketch030]
FEATURE [PartDesign::Plane] DatumPlane008
  Length = 60
  MapMode = 5
  Placement = pos=(0,0,-5) rot=(1,0,0;3.14159rad)
  ResizeMode = 0
  Support = -> [AdditiveLoft006]
  Width = 60
FEATURE [Sketcher::SketchObject] Sketch031
  FullyConstrained = true
  MapMode = 5
  Placement = pos=(0,0,-5) rot=(1,0,0;3.14159rad)
  Support = -> [DatumPlane008]
  sketch-geometry (1):
    g0: Circle CenterX=0 CenterY=0 CenterZ=0 NormalX=0 NormalY=0 NormalZ=1 AngleXU=0 Radius=4
  constraints (2):
    c: Coincident(g0,g-1)
    c: Radius(g0) = 4
FEATURE [PartDesign::Pad] Pad011
  BaseFeature = -> AdditiveLoft006
  Direction = (0,0,-1)
  Length = 3.3
  Length2 = 100
  Profile = -> Sketch031
  Refine = true
  Type = 0
FEATURE [Sketcher::SketchObject] Sketch035
  FullyConstrained = true
  MapMode = 5
  Placement = pos=(0,0,1) rot=(0,0,1;0rad)
  sketch-geometry (4):
    g0: LineSegment StartX=-7 StartY=7 StartZ=0 EndX=7 EndY=7 EndZ=0
    g1: LineSegment StartX=7 StartY=7 StartZ=0 EndX=7 EndY=-7 EndZ=0
    g2: LineSegment StartX=7 StartY=-7 StartZ=0 EndX=-7 EndY=-7 EndZ=0
    g3: LineSegment StartX=-7 StartY=-7 StartZ=0 EndX=-7 EndY=7 EndZ=0
  constraints (11):
    c: Coincident(g0,g1)
    c: Coincident(g1,g2)
    c: Coincident(g2,g3)
    c: Coincident(g3,g0)
    c: Horizontal(g0)
    c: Horizontal(g2)
    c: Vertical(g1)
    c: Vertical(g3)
    c: Symmetric(g0,g1,g-1)
    c: Equal(g0,g3)
    c: DistanceX(g0,g0) = 14
FEATURE [Sketcher::SketchObject] Sketch036
  AttachmentOffset = pos=(0,0,5.6) rot=(0,0,1;0rad)
  FullyConstrained = true
  MapMode = 5
  Placement = pos=(0,0,6.6) rot=(0,0,1;0rad)
  expr: .AttachmentOffset.Base.z = 11.6 - 5 - 1
  sketch-geometry (4):
    g0: LineSegment StartX=-4 StartY=4 StartZ=0 EndX=4 EndY=4 EndZ=0
    g1: LineSegment StartX=4 StartY=4 StartZ=0 EndX=4 EndY=-4 EndZ=0
    g2: LineSegment StartX=4 StartY=-4 StartZ=0 EndX=-4 EndY=-4 EndZ=0
    g3: LineSegment StartX=-4 StartY=-4 StartZ=0 EndX=-4 EndY=4 EndZ=0
  constraints (11):
    c: Coincident(g0,g1)
    c: Coincident(g1,g2)
    c: Coincident(g2,g3)
    c: Coincident(g3,g0)
    c: Horizontal(g0)
    c: Horizontal(g2)
    c: Vertical(g1)
    c: Vertical(g3)
    c: Equal(g0,g3)
    c: Symmetric(g0,g1,g-1)
    c: DistanceX(g0,g0) = 8
FEATURE [PartDesign::AdditiveLoft] AdditiveLoft007
  BaseFeature = -> Pad011
  Closed = false
  Profile = -> Sketch035
  Refine = true
  Ruled = false
  Sections = -> [Sketch036]
FEATURE [Sketcher::SketchObject] Sketch037
  AttachmentOffset = pos=(0,0,16) rot=(0,0,1;0rad)
  FullyConstrained = true
  MapMode = 5
  Placement = pos=(0,0,17) rot=(0,0,1;0rad)
  expr: Constraints[8] = 36.2 mm - 5.73 mm
  sketch-geometry (4):
    g0: LineSegment StartX=-15.235 StartY=6.185 StartZ=0 EndX=15.235 EndY=6.185 EndZ=0
    g1: LineSegment StartX=15.235 StartY=6.185 StartZ=0 EndX=15.235 EndY=-6.185 EndZ=0
    g2: LineSegment StartX=15.235 StartY=-6.185 StartZ=0 EndX=-15.235 EndY=-6.185 EndZ=0
    g3: LineSegment StartX=-15.235 StartY=-6.185 StartZ=0 EndX=-15.235 EndY=6.185 EndZ=0
  constraints (11):
    c: Coincident(g0,g1)
    c: Coincident(g1,g2)
    c: Coincident(g2,g3)
    c: Coincident(g3,g0)
    c: Horizontal(g0)
    c: Horizontal(g2)
    c: Vertical(g1)
    c: Vertical(g3)
    c: DistanceX(g0,g0) = 30.47
    c: Symmetric(g0,g1,g-1)
    c: DistanceY(g1,g1) = 12.37
FEATURE [Sketcher::SketchObject] Sketch038
  AttachmentOffset = pos=(0,0,4.61) rot=(0,0,1;0rad)
  FullyConstrained = true
  MapMode = 5
  Placement = pos=(0,0,5.61) rot=(0,0,1;0rad)
  expr: .AttachmentOffset.Base.z = 16 - 9.39 - 2
  expr: Constraints[8] = 18.2 mm * 2
  sketch-geometry (4):
    g0: LineSegment StartX=-18.2 StartY=9.05 StartZ=0 EndX=18.2 EndY=9.05 EndZ=0
    g1: LineSegment StartX=18.2 StartY=9.05 StartZ=0 EndX=18.2 EndY=-9.05 EndZ=0
    g2: LineSegment StartX=18.2 StartY=-9.05 StartZ=0 EndX=-18.2 EndY=-9.05 EndZ=0
    g3: LineSegment StartX=-18.2 StartY=-9.05 StartZ=0 EndX=-18.2 EndY=9.05 EndZ=0
  constraints (11):
    c: Coincident(g0,g1)
    c: Coincident(g1,g2)
    c: Coincident(g2,g3)
    c: Coincident(g3,g0)
    c: Horizontal(g0)
    c: Horizontal(g2)
    c: Vertical(g1)
    c: Vertical(g3)
    c: DistanceX(g0,g0) = 36.4
    c: Symmetric(g0,g1,g-1)
    c: DistanceY(g1,g1) = 18.1
FEATURE [PartDesign::AdditiveLoft] AdditiveLoft008
  BaseFeature = -> AdditiveLoft007
  Closed = false
  Profile = -> Sketch037
  Refine = true
  Ruled = false
  Sections = -> [Sketch038]
FEATURE [PartDesign::Body] Body005  label="MXSwitch200"
  Group = -> [Sketch032,Pad009,Sketch033,Pad010,DatumPlane007,Sketch034,Sketch030,AdditiveLoft006,DatumPlane008,Sketch031,Pad011,Sketch035,Sketch036,AdditiveLoft007,Sketch037,Sketch038,AdditiveLoft008]
  Origin = -> Origin005
  Tip = -> AdditiveLoft008
FEATURE [Sketcher::SketchObject] Sketch041
  FullyConstrained = true
  MapMode = 5
  Support = -> [XY_Plane006]
  sketch-geometry (4):
    g0: LineSegment StartX=-7.8 StartY=7.8 StartZ=0 EndX=7.8 EndY=7.8 EndZ=0
    g1: LineSegment StartX=7.8 StartY=7.8 StartZ=0 EndX=7.8 EndY=-7.8 EndZ=0
    g2: LineSegment StartX=7.8 StartY=-7.8 StartZ=0 EndX=-7.8 EndY=-7.8 EndZ=0
    g3: LineSegment StartX=-7.8 StartY=-7.8 StartZ=0 EndX=-7.8 EndY=7.8 EndZ=0
  constraints (11):
    c: Coincident(g0,g1)
    c: Coincident(g1,g2)
    c: Coincident(g2,g3)
    c: Coincident(g3,g0)
    c: Horizontal(g0)
    c: Horizontal(g2)
    c: Vertical(g1)
    c: Vertical(g3)
    c: DistanceX(g0,g0) = 15.6
    c: Equal(g0,g3)
    c: Symmetric(g0,g1,g-1)
FEATURE [PartDesign::Pad] Pad012
  Direction = (0,0,1)
  Length = 1
  Length2 = 100
  Profile = -> Sketch041
  Refine = true
  Type = 0
FEATURE [Sketcher::SketchObject] Sketch042
  FullyConstrained = true
  MapMode = 5
  Support = -> [XY_Plane006]
  sketch-geometry (4):
    g0: LineSegment StartX=-7 StartY=7 StartZ=0 EndX=7 EndY=7 EndZ=0
    g1: LineSegment StartX=7 StartY=7 StartZ=0 EndX=7 EndY=-7 EndZ=0
    g2: LineSegment StartX=7 StartY=-7 StartZ=0 EndX=-7 EndY=-7 EndZ=0
    g3: LineSegment StartX=-7 StartY=-7 StartZ=0 EndX=-7 EndY=7 EndZ=0
  constraints (11):
    c: Coincident(g0,g1)
    c: Coincident(g1,g2)
    c: Coincident(g2,g3)
    c: Coincident(g3,g0)
    c: Horizontal(g0)
    c: Horizontal(g2)
    c: Vertical(g1)
    c: Vertical(g3)
    c: Symmetric(g0,g1,g-1)
    c: Equal(g0,g3)
    c: DistanceX(g0,g0) = 14
FEATURE [PartDesign::Pad] Pad013
  BaseFeature = -> Pad012
  Direction = (0,0,1)
  Length = 2.5
  Length2 = 100
  Profile = -> Sketch042
  Refine = true
  Reversed = true
  Type = 0
FEATURE [PartDesign::Plane] DatumPlane010
  Length = 60.1661
  MapMode = 5
  Placement = pos=(0,0,-2.5) rot=(1,0,0;3.14159rad)
  ResizeMode = 0
  Support = -> [Pad013]
  Width = 61.8411
FEATURE [Sketcher::SketchObject] Sketch039
  FullyConstrained = true
  MapMode = 5
  Placement = pos=(0,0,-2.5) rot=(1,0,0;3.14159rad)
  Support = -> [DatumPlane010]
  sketch-geometry (4):
    g0: LineSegment StartX=-7 StartY=7 StartZ=0 EndX=7 EndY=7 EndZ=0
    g1: LineSegment StartX=7 StartY=7 StartZ=0 EndX=7 EndY=-7 EndZ=0
    g2: LineSegment StartX=7 StartY=-7 StartZ=0 EndX=-7 EndY=-7 EndZ=0
    g3: LineSegment StartX=-7 StartY=-7 StartZ=0 EndX=-7 EndY=7 EndZ=0
  constraints (11):
    c: Coincident(g0,g1)
    c: Coincident(g1,g2)
    c: Coincident(g2,g3)
    c: Coincident(g3,g0)
    c: Horizontal(g0)
    c: Horizontal(g2)
    c: Vertical(g1)
    c: Vertical(g3)
    c: Equal(g0,g3)
    c: DistanceX(g0,g0) = 14
    c: Symmetric(g0,g1,g-1)
FEATURE [Sketcher::SketchObject] Sketch043
  AttachmentOffset = pos=(0,0,2.5) rot=(0,0,1;0rad)
  FullyConstrained = true
  MapMode = 5
  Placement = pos=(0,0,-5) rot=(1,0,0;3.14159rad)
  Support = -> [DatumPlane010]
  sketch-geometry (4):
    g0: LineSegment StartX=-5 StartY=5 StartZ=0 EndX=5 EndY=5 EndZ=0
    g1: LineSegment StartX=5 StartY=5 StartZ=0 EndX=5 EndY=-5 EndZ=0
    g2: LineSegment StartX=5 StartY=-5 StartZ=0 EndX=-5 EndY=-5 EndZ=0
    g3: LineSegment StartX=-5 StartY=-5 StartZ=0 EndX=-5 EndY=5 EndZ=0
  constraints (11):
    c: Coincident(g0,g1)
    c: Coincident(g1,g2)
    c: Coincident(g2,g3)
    c: Coincident(g3,g0)
    c: Horizontal(g0)
    c: Horizontal(g2)
    c: Vertical(g1)
    c: Vertical(g3)
    c: DistanceX(g0,g0) = 10
    c: Equal(g0,g3)
    c: Symmetric(g0,g1,g-1)
FEATURE [PartDesign::AdditiveLoft] AdditiveLoft009
  BaseFeature = -> Pad013
  Closed = false
  Profile = -> Sketch043
  Refine = true
  Ruled = false
  Sections = -> [Sketch039]
FEATURE [PartDesign::Plane] DatumPlane011
  Length = 60.1661
  MapMode = 5
  Placement = pos=(0,0,-5) rot=(1,0,0;3.14159rad)
  ResizeMode = 0
  Support = -> [AdditiveLoft009]
  Width = 61.8411
FEATURE [Sketcher::SketchObject] Sketch040
  FullyConstrained = true
  MapMode = 5
  Placement = pos=(0,0,-5) rot=(1,0,0;3.14159rad)
  Support = -> [DatumPlane011]
  sketch-geometry (1):
    g0: Circle CenterX=0 CenterY=0 CenterZ=0 NormalX=0 NormalY=0 NormalZ=1 AngleXU=0 Radius=4
  constraints (2):
    c: Coincident(g0,g-1)
    c: Radius(g0) = 4
FEATURE [PartDesign::Pad] Pad014
  BaseFeature = -> AdditiveLoft009
  Direction = (0,0,-1)
  Length = 3.3
  Length2 = 100
  Profile = -> Sketch040
  Refine = true
  Type = 0
FEATURE [Sketcher::SketchObject] Sketch044
  FullyConstrained = true
  MapMode = 5
  Placement = pos=(0,0,1) rot=(0,0,1;0rad)
  sketch-geometry (4):
    g0: LineSegment StartX=-7 StartY=7 StartZ=0 EndX=7 EndY=7 EndZ=0
    g1: LineSegment StartX=7 StartY=7 StartZ=0 EndX=7 EndY=-7 EndZ=0
    g2: LineSegment StartX=7 StartY=-7 StartZ=0 EndX=-7 EndY=-7 EndZ=0
    g3: LineSegment StartX=-7 StartY=-7 StartZ=0 EndX=-7 EndY=7 EndZ=0
  constraints (11):
    c: Coincident(g0,g1)
    c: Coincident(g1,g2)
    c: Coincident(g2,g3)
    c: Coincident(g3,g0)
    c: Horizontal(g0)
    c: Horizontal(g2)
    c: Vertical(g1)
    c: Vertical(g3)
    c: Symmetric(g0,g1,g-1)
    c: Equal(g0,g3)
    c: DistanceX(g0,g0) = 14
FEATURE [Sketcher::SketchObject] Sketch045
  AttachmentOffset = pos=(0,0,5.6) rot=(0,0,1;0rad)
  FullyConstrained = true
  MapMode = 5
  Placement = pos=(0,0,6.6) rot=(0,0,1;0rad)
  expr: .AttachmentOffset.Base.z = 11.6 - 5 - 1
  sketch-geometry (4):
    g0: LineSegment StartX=-4 StartY=4 StartZ=0 EndX=4 EndY=4 EndZ=0
    g1: LineSegment StartX=4 StartY=4 StartZ=0 EndX=4 EndY=-4 EndZ=0
    g2: LineSegment StartX=4 StartY=-4 StartZ=0 EndX=-4 EndY=-4 EndZ=0
    g3: LineSegment StartX=-4 StartY=-4 StartZ=0 EndX=-4 EndY=4 EndZ=0
  constraints (11):
    c: Coincident(g0,g1)
    c: Coincident(g1,g2)
    c: Coincident(g2,g3)
    c: Coincident(g3,g0)
    c: Horizontal(g0)
    c: Horizontal(g2)
    c: Vertical(g1)
    c: Vertical(g3)
    c: Equal(g0,g3)
    c: Symmetric(g0,g1,g-1)
    c: DistanceX(g0,g0) = 8
FEATURE [PartDesign::AdditiveLoft] AdditiveLoft010
  BaseFeature = -> Pad014
  Closed = false
  Profile = -> Sketch044
  Refine = true
  Ruled = false
  Sections = -> [Sketch045]
FEATURE [Sketcher::SketchObject] Sketch046
  AttachmentOffset = pos=(0,0,16) rot=(0,0,1;0rad)
  FullyConstrained = true
  MapMode = 5
  Placement = pos=(0,0,17) rot=(0,0,1;0rad)
  expr: Constraints[14] = 13.05 mm
  expr: Constraints[15] = 18.05 mm
  expr: Constraints[16] = 5.68 mm * 1.25
  expr: Constraints[17] = 5.68 mm * 1.25
  sketch-geometry (7):
    g0: LineSegment StartX=-14.95 StartY=7.1 StartZ=0 EndX=7.1 EndY=7.1 EndZ=0
    g1: LineSegment StartX=7.1 StartY=7.1 StartZ=0 EndX=7.1 EndY=-24 EndZ=0
    g2: LineSegment StartX=7.1 StartY=-24 StartZ=0 EndX=-9.95 EndY=-24 EndZ=0
    g3: LineSegment StartX=-14.95 StartY=7.1 StartZ=0 EndX=-14.95 EndY=-5.95 EndZ=0
    g4: LineSegment StartX=-14.95 StartY=-5.95 StartZ=0 EndX=-9.95 EndY=-5.95 EndZ=0
    g5: LineSegment StartX=-9.95 StartY=-24 StartZ=0 EndX=-9.95 EndY=-5.95 EndZ=0
    g6: GeomPoint X=0 Y=-1e-16 Z=0
  constraints (19):
    c: Coincident(g0,g1)
    c: Coincident(g1,g2)
    c: Horizontal(g0)
    c: Horizontal(g2)
    c: Vertical(g1)
    c: Coincident(g3,g0)
    c: Coincident(g4,g3)
    c: Coincident(g5,g2)
    c: Coincident(g5,g4)
    c: Horizontal(g4)
    c: Vertical(g3)
    c: Vertical(g5)
    c: DistanceX(g0,g0) = 22.05
    c: DistanceX(g2,g2) = 17.05
    c: DistanceY(g3,g3) = 13.05
    c: DistanceY(g5,g5) = 18.05
    c: DistanceY(g6,g0) = 7.1
    c: DistanceX(g6,g0) = 7.1
    c: Coincident(g-1,g6)
FEATURE [Sketcher::SketchObject] Sketch047
  AttachmentOffset = pos=(0,0,4.61) rot=(0,0,1;0rad)
  FullyConstrained = true
  MapMode = 5
  Placement = pos=(0,0,5.61) rot=(0,0,1;0rad)
  expr: .AttachmentOffset.Base.z = 16 - 9.39 - 2
  expr: Constraints[12] = 18.1 mm * 1.25
  expr: Constraints[13] = 18.1 mm * 1.5
  expr: Constraints[14] = 18.1 mm
  expr: Constraints[15] = 18.1
  expr: Constraints[16] = 19.05 mm * 0.5
  expr: Constraints[17] = 19.05 mm * 0.5
  sketch-geometry (7):
    g0: LineSegment StartX=9.525 StartY=9.525 StartZ=0 EndX=-17.625 EndY=9.525 EndZ=0
    g1: LineSegment StartX=-13.1 StartY=-26.675 StartZ=0 EndX=9.525 EndY=-26.675 EndZ=0
    g2: LineSegment StartX=9.525 StartY=-26.675 StartZ=0 EndX=9.525 EndY=9.525 EndZ=0
    g3: LineSegment StartX=-17.625 StartY=9.525 StartZ=0 EndX=-17.625 EndY=-8.575 EndZ=0
    g4: LineSegment StartX=-17.625 StartY=-8.575 StartZ=0 EndX=-13.1 EndY=-8.575 EndZ=0
    g5: LineSegment StartX=-13.1 StartY=-26.675 StartZ=0 EndX=-13.1 EndY=-8.575 EndZ=0
    g6: GeomPoint X=0 Y=0 Z=0
  constraints (19):
    c: Coincident(g1,g2)
    c: Coincident(g2,g0)
    c: Horizontal(g0)
    c: Horizontal(g1)
    c: Vertical(g2)
    c: Coincident(g3,g0)
    c: Coincident(g4,g3)
    c: Coincident(g5,g1)
    c: Coincident(g5,g4)
    c: Horizontal(g4)
    c: Vertical(g3)
    c: Vertical(g5)
    c: DistanceX(g1,g1) = 22.625
    c: DistanceX(g0,g0) = 27.15
    c: DistanceY(g3,g3) = 18.1
    c: DistanceY(g5,g5) = 18.1
    c: DistanceX(g6,g0) = 9.525
    c: DistanceY(g6,g0) = 9.525
    c: Coincident(g-1,g6)
FEATURE [PartDesign::AdditiveLoft] AdditiveLoft011
  BaseFeature = -> AdditiveLoft010
  Closed = false
  Profile = -> Sketch046
  Refine = true
  Ruled = false
  Sections = -> [Sketch047]
FEATURE [PartDesign::Body] Body006  label="MXSwitchIsoEnter"
  Group = -> [Sketch041,Pad012,Sketch042,Pad013,DatumPlane010,Sketch043,Sketch039,AdditiveLoft009,DatumPlane011,Sketch040,Pad014,Sketch044,Sketch045,AdditiveLoft010,Sketch046,Sketch047,AdditiveLoft011]
  Origin = -> Origin006
  Tip = -> AdditiveLoft011
FEATURE [Sketcher::SketchObject] Sketch050
  FullyConstrained = true
  MapMode = 5
  Support = -> [XY_Plane007]
  sketch-geometry (4):
    g0: LineSegment StartX=-7.8 StartY=7.8 StartZ=0 EndX=7.8 EndY=7.8 EndZ=0
    g1: LineSegment StartX=7.8 StartY=7.8 StartZ=0 EndX=7.8 EndY=-7.8 EndZ=0
    g2: LineSegment StartX=7.8 StartY=-7.8 StartZ=0 EndX=-7.8 EndY=-7.8 EndZ=0
    g3: LineSegment StartX=-7.8 StartY=-7.8 StartZ=0 EndX=-7.8 EndY=7.8 EndZ=0
  constraints (11):
    c: Coincident(g0,g1)
    c: Coincident(g1,g2)
    c: Coincident(g2,g3)
    c: Coincident(g3,g0)
    c: Horizontal(g0)
    c: Horizontal(g2)
    c: Vertical(g1)
    c: Vertical(g3)
    c: DistanceX(g0,g0) = 15.6
    c: Equal(g0,g3)
    c: Symmetric(g0,g1,g-1)
FEATURE [PartDesign::Pad] Pad015
  Direction = (0,0,1)
  Length = 1
  Length2 = 100
  Profile = -> Sketch050
  Refine = true
  Type = 0
FEATURE [Sketcher::SketchObject] Sketch051
  FullyConstrained = true
  MapMode = 5
  Support = -> [XY_Plane007]
  sketch-geometry (4):
    g0: LineSegment StartX=-7 StartY=7 StartZ=0 EndX=7 EndY=7 EndZ=0
    g1: LineSegment StartX=7 StartY=7 StartZ=0 EndX=7 EndY=-7 EndZ=0
    g2: LineSegment StartX=7 StartY=-7 StartZ=0 EndX=-7 EndY=-7 EndZ=0
    g3: LineSegment StartX=-7 StartY=-7 StartZ=0 EndX=-7 EndY=7 EndZ=0
  constraints (11):
    c: Coincident(g0,g1)
    c: Coincident(g1,g2)
    c: Coincident(g2,g3)
    c: Coincident(g3,g0)
    c: Horizontal(g0)
    c: Horizontal(g2)
    c: Vertical(g1)
    c: Vertical(g3)
    c: Symmetric(g0,g1,g-1)
    c: Equal(g0,g3)
    c: DistanceX(g0,g0) = 14
FEATURE [PartDesign::Pad] Pad016
  BaseFeature = -> Pad015
  Direction = (0,0,1)
  Length = 2.5
  Length2 = 100
  Profile = -> Sketch051
  Refine = true
  Reversed = true
  Type = 0
FEATURE [PartDesign::Plane] DatumPlane012
  Length = 60
  MapMode = 5
  Placement = pos=(0,0,-2.5) rot=(1,0,0;3.14159rad)
  ResizeMode = 0
  Support = -> [Pad016]
  Width = 60
FEATURE [Sketcher::SketchObject] Sketch048
  FullyConstrained = true
  MapMode = 5
  Placement = pos=(0,0,-2.5) rot=(1,0,0;3.14159rad)
  Support = -> [DatumPlane012]
  sketch-geometry (4):
    g0: LineSegment StartX=-7 StartY=7 StartZ=0 EndX=7 EndY=7 EndZ=0
    g1: LineSegment StartX=7 StartY=7 StartZ=0 EndX=7 EndY=-7 EndZ=0
    g2: LineSegment StartX=7 StartY=-7 StartZ=0 EndX=-7 EndY=-7 EndZ=0
    g3: LineSegment StartX=-7 StartY=-7 StartZ=0 EndX=-7 EndY=7 EndZ=0
  constraints (11):
    c: Coincident(g0,g1)
    c: Coincident(g1,g2)
    c: Coincident(g2,g3)
    c: Coincident(g3,g0)
    c: Horizontal(g0)
    c: Horizontal(g2)
    c: Vertical(g1)
    c: Vertical(g3)
    c: Equal(g0,g3)
    c: DistanceX(g0,g0) = 14
    c: Symmetric(g0,g1,g-1)
FEATURE [Sketcher::SketchObject] Sketch052
  AttachmentOffset = pos=(0,0,2.5) rot=(0,0,1;0rad)
  FullyConstrained = true
  MapMode = 5
  Placement = pos=(0,0,-5) rot=(1,0,0;3.14159rad)
  Support = -> [DatumPlane012]
  sketch-geometry (4):
    g0: LineSegment StartX=-5 StartY=5 StartZ=0 EndX=5 EndY=5 EndZ=0
    g1: LineSegment StartX=5 StartY=5 StartZ=0 EndX=5 EndY=-5 EndZ=0
    g2: LineSegment StartX=5 StartY=-5 StartZ=0 EndX=-5 EndY=-5 EndZ=0
    g3: LineSegment StartX=-5 StartY=-5 StartZ=0 EndX=-5 EndY=5 EndZ=0
  constraints (11):
    c: Coincident(g0,g1)
    c: Coincident(g1,g2)
    c: Coincident(g2,g3)
    c: Coincident(g3,g0)
    c: Horizontal(g0)
    c: Horizontal(g2)
    c: Vertical(g1)
    c: Vertical(g3)
    c: DistanceX(g0,g0) = 10
    c: Equal(g0,g3)
    c: Symmetric(g0,g1,g-1)
FEATURE [PartDesign::AdditiveLoft] AdditiveLoft012
  BaseFeature = -> Pad016
  Closed = false
  Profile = -> Sketch052
  Refine = true
  Ruled = false
  Sections = -> [Sketch048]
FEATURE [PartDesign::Plane] DatumPlane013
  Length = 60
  MapMode = 5
  Placement = pos=(0,0,-5) rot=(1,0,0;3.14159rad)
  ResizeMode = 0
  Support = -> [AdditiveLoft012]
  Width = 60
FEATURE [Sketcher::SketchObject] Sketch049
  FullyConstrained = true
  MapMode = 5
  Placement = pos=(0,0,-5) rot=(1,0,0;3.14159rad)
  Support = -> [DatumPlane013]
  sketch-geometry (1):
    g0: Circle CenterX=0 CenterY=0 CenterZ=0 NormalX=0 NormalY=0 NormalZ=1 AngleXU=0 Radius=4
  constraints (2):
    c: Coincident(g0,g-1)
    c: Radius(g0) = 4
FEATURE [PartDesign::Pad] Pad017
  BaseFeature = -> AdditiveLoft012
  Direction = (0,0,-1)
  Length = 3.3
  Length2 = 100
  Profile = -> Sketch049
  Refine = true
  Type = 0
FEATURE [Sketcher::SketchObject] Sketch053
  FullyConstrained = true
  MapMode = 5
  Placement = pos=(0,0,1) rot=(0,0,1;0rad)
  sketch-geometry (4):
    g0: LineSegment StartX=-7 StartY=7 StartZ=0 EndX=7 EndY=7 EndZ=0
    g1: LineSegment StartX=7 StartY=7 StartZ=0 EndX=7 EndY=-7 EndZ=0
    g2: LineSegment StartX=7 StartY=-7 StartZ=0 EndX=-7 EndY=-7 EndZ=0
    g3: LineSegment StartX=-7 StartY=-7 StartZ=0 EndX=-7 EndY=7 EndZ=0
  constraints (11):
    c: Coincident(g0,g1)
    c: Coincident(g1,g2)
    c: Coincident(g2,g3)
    c: Coincident(g3,g0)
    c: Horizontal(g0)
    c: Horizontal(g2)
    c: Vertical(g1)
    c: Vertical(g3)
    c: Symmetric(g0,g1,g-1)
    c: Equal(g0,g3)
    c: DistanceX(g0,g0) = 14
FEATURE [Sketcher::SketchObject] Sketch054
  AttachmentOffset = pos=(0,0,5.6) rot=(0,0,1;0rad)
  FullyConstrained = true
  MapMode = 5
  Placement = pos=(0,0,6.6) rot=(0,0,1;0rad)
  expr: .AttachmentOffset.Base.z = 11.6 - 5 - 1
  sketch-geometry (4):
    g0: LineSegment StartX=-4 StartY=4 StartZ=0 EndX=4 EndY=4 EndZ=0
    g1: LineSegment StartX=4 StartY=4 StartZ=0 EndX=4 EndY=-4 EndZ=0
    g2: LineSegment StartX=4 StartY=-4 StartZ=0 EndX=-4 EndY=-4 EndZ=0
    g3: LineSegment StartX=-4 StartY=-4 StartZ=0 EndX=-4 EndY=4 EndZ=0
  constraints (11):
    c: Coincident(g0,g1)
    c: Coincident(g1,g2)
    c: Coincident(g2,g3)
    c: Coincident(g3,g0)
    c: Horizontal(g0)
    c: Horizontal(g2)
    c: Vertical(g1)
    c: Vertical(g3)
    c: Equal(g0,g3)
    c: Symmetric(g0,g1,g-1)
    c: DistanceX(g0,g0) = 8
FEATURE [PartDesign::AdditiveLoft] AdditiveLoft013
  BaseFeature = -> Pad017
  Closed = false
  Profile = -> Sketch053
  Refine = true
  Ruled = false
  Sections = -> [Sketch054]
FEATURE [Sketcher::SketchObject] Sketch055
  AttachmentOffset = pos=(0,0,16) rot=(0,0,1;0rad)
  FullyConstrained = true
  MapMode = 5
  Placement = pos=(0,0,17) rot=(0,0,1;0rad)
  expr: Constraints[8] = 12.37 mm * 1.5
  sketch-geometry (4):
    g0: LineSegment StartX=-9.2775 StartY=6.185 StartZ=0 EndX=9.2775 EndY=6.185 EndZ=0
    g1: LineSegment StartX=9.2775 StartY=6.185 StartZ=0 EndX=9.2775 EndY=-6.185 EndZ=0
    g2: LineSegment StartX=9.2775 StartY=-6.185 StartZ=0 EndX=-9.2775 EndY=-6.185 EndZ=0
    g3: LineSegment StartX=-9.2775 StartY=-6.185 StartZ=0 EndX=-9.2775 EndY=6.185 EndZ=0
  constraints (11):
    c: Coincident(g0,g1)
    c: Coincident(g1,g2)
    c: Coincident(g2,g3)
    c: Coincident(g3,g0)
    c: Horizontal(g0)
    c: Horizontal(g2)
    c: Vertical(g1)
    c: Vertical(g3)
    c: DistanceX(g0,g0) = 18.555
    c: Symmetric(g0,g1,g-1)
    c: DistanceY(g1,g1) = 12.37
FEATURE [Sketcher::SketchObject] Sketch056
  AttachmentOffset = pos=(0,0,4.61) rot=(0,0,1;0rad)
  FullyConstrained = true
  MapMode = 5
  Placement = pos=(0,0,5.61) rot=(0,0,1;0rad)
  expr: .AttachmentOffset.Base.z = 16 - 9.39 - 2
  expr: Constraints[8] = 18.1 mm * 1.5
  sketch-geometry (4):
    g0: LineSegment StartX=-13.575 StartY=9.05 StartZ=0 EndX=13.575 EndY=9.05 EndZ=0
    g1: LineSegment StartX=13.575 StartY=9.05 StartZ=0 EndX=13.575 EndY=-9.05 EndZ=0
    g2: LineSegment StartX=13.575 StartY=-9.05 StartZ=0 EndX=-13.575 EndY=-9.05 EndZ=0
    g3: LineSegment StartX=-13.575 StartY=-9.05 StartZ=0 EndX=-13.575 EndY=9.05 EndZ=0
  constraints (11):
    c: Coincident(g0,g1)
    c: Coincident(g1,g2)
    c: Coincident(g2,g3)
    c: Coincident(g3,g0)
    c: Horizontal(g0)
    c: Horizontal(g2)
    c: Vertical(g1)
    c: Vertical(g3)
    c: DistanceX(g0,g0) = 27.15
    c: Symmetric(g0,g1,g-1)
    c: DistanceY(g1,g1) = 18.1
FEATURE [PartDesign::AdditiveLoft] AdditiveLoft014
  BaseFeature = -> AdditiveLoft013
  Closed = false
  Profile = -> Sketch055
  Refine = true
  Ruled = false
  Sections = -> [Sketch056]
FEATURE [PartDesign::Body] Body007  label="MXSwitch150"
  Group = -> [Sketch050,Pad015,Sketch051,Pad016,DatumPlane012,Sketch052,Sketch048,AdditiveLoft012,DatumPlane013,Sketch049,Pad017,Sketch053,Sketch054,AdditiveLoft013,Sketch055,Sketch056,AdditiveLoft014]
  Origin = -> Origin007
  Tip = -> AdditiveLoft014
FEATURE [Part::Refine] Body008  label="MXSwitch100Nice"
  Source = -> Body003
FEATURE [Part::Refine] Body009  label="MXSwitch200Nice"
  Source = -> Body005
---- part ../components/PJ-313B__JACK35F-4P-PCB.FCStd = doc fcstd_f70287cfb8dc ----
FCSTD DOCUMENT  (FreeCAD 0.21R33668 +26 (Git))
Label: PJ-313B__JACK35F-4P-PCB
License: All rights reserved
LicenseURL: http://en.wikipedia.org/wiki/All_rights_reserved
objects: Sketcher::SketchObject×5, PartDesign::Pad×3, PartDesign::Body×2, Part::Refine×2, App::DocumentObjectGroup×2, PartDesign::Mirrored×1, PartDesign::LinearPattern×1, PartDesign::MultiTransform×1, PartDesign::AdditiveLoft×1
note: 20 computed .brp shape members not serialized (recipe doc carries the construction recipe); baked Part::Feature solids carry a one-line shape summary decoded from their .brp

FEATURE [Sketcher::SketchObject] Sketch
  FullyConstrained = true
  MapMode = 5
  Placement = pos=(0,0,0) rot=(0.57735,0.57735,0.57735;2.0944rad)
  Support = -> [YZ_Plane]
  sketch-geometry (4):
    g0: LineSegment StartX=-14.6 StartY=5 StartZ=0 EndX=0 EndY=5 EndZ=0
    g1: LineSegment StartX=0 StartY=5 StartZ=0 EndX=0 EndY=0 EndZ=0
    g2: LineSegment StartX=0 StartY=0 StartZ=0 EndX=-14.6 EndY=0 EndZ=0
    g3: LineSegment StartX=-14.6 StartY=0 StartZ=0 EndX=-14.6 EndY=5 EndZ=0
  constraints (11):
    c: Coincident(g0,g1)
    c: Coincident(g1,g2)
    c: Coincident(g2,g3)
    c: Coincident(g3,g0)
    c: Horizontal(g0)
    c: Horizontal(g2)
    c: Vertical(g1)
    c: Vertical(g3)
    c: Coincident(g1,g-1)
    c: DistanceX(g0,g0) = 14.6
    c: DistanceY(g3,g3) = 5
FEATURE [PartDesign::Pad] Pad
  Direction = (1,-2e-16,3e-16)
  Length = 5
  Length2 = 10
  Midplane = true
  Placement = pos=(0,0,0) rot=(0.57735,0.57735,0.57735;2.0944rad)
  Profile = -> Sketch
  ReferenceAxis = -> Sketch [N_Axis]
  Type = 0
FEATURE [Sketcher::SketchObject] Sketch001
  ExternalGeometry = -> [Pad]
  FullyConstrained = true
  MapMode = 5
  Placement = pos=(0,0,0) rot=(0.57735,0.57735,0.57735;4.18879rad)
  Support = -> [Pad]
  sketch-geometry (2):
    g0: Circle CenterX=2.5 CenterY=-1e-15 CenterZ=0 NormalX=0 NormalY=0 NormalZ=1 AngleXU=0 Radius=1.8
    g1: Circle CenterX=2.5 CenterY=-1e-15 CenterZ=0 NormalX=0 NormalY=0 NormalZ=1 AngleXU=0 Radius=2.5
  constraints (4):
    c: Radius(g0) = 1.8
    c: Symmetric(g-4,g-3,g0)
    c: Coincident(g1,g0)
    c: Radius(g1) = 2.5
FEATURE [PartDesign::Pad] Pad001
  BaseFeature = -> Pad
  Direction = (4e-16,1,-2e-16)
  Length = 2.5
  Length2 = 10
  Placement = pos=(0,0,0) rot=(0.57735,0.57735,0.57735;2.0944rad)
  Profile = -> Sketch001
  ReferenceAxis = -> Sketch001 [N_Axis]
  Type = 0
FEATURE [Sketcher::SketchObject] Sketch002
  AttachmentOffset = pos=(0,0,2.5) rot=(0,0,1;0rad)
  FullyConstrained = true
  MapMode = 5
  Placement = pos=(0,0,2.5) rot=(0,0,1;0rad)
  Support = -> [XY_Plane]
  expr: Constraints[12] = 1.8 mm + 3.2 mm * 3
  sketch-geometry (5):
    g0: LineSegment StartX=-3.25 StartY=-10.75 StartZ=0 EndX=-2.45 EndY=-10.75 EndZ=0
    g1: LineSegment StartX=-2.45 StartY=-10.75 StartZ=0 EndX=-2.45 EndY=-12.05 EndZ=0
    g2: LineSegment StartX=-2.45 StartY=-12.05 StartZ=0 EndX=-3.25 EndY=-12.05 EndZ=0
    g3: LineSegment StartX=-3.25 StartY=-12.05 StartZ=0 EndX=-3.25 EndY=-10.75 EndZ=0
    g4: GeomPoint X=-2.85 Y=-11.4 Z=0
  constraints (13):
    c: Coincident(g0,g1)
    c: Coincident(g1,g2)
    c: Coincident(g2,g3)
    c: Coincident(g3,g0)
    c: Horizontal(g0)
    c: Horizontal(g2)
    c: Vertical(g1)
    c: Vertical(g3)
    c: DistanceY(g3,g3) = 1.3
    c: DistanceX(g0,g0) = 0.8
    c: Symmetric(g0,g1,g4)
    c: DistanceX(g4,g-1) = 2.85
    c: DistanceY(g4,g-1) = 11.4
FEATURE [PartDesign::Pad] Pad002
  BaseFeature = -> Pad001
  Direction = (0,0,1)
  Length = 5.5
  Length2 = 10
  Placement = pos=(0,0,0) rot=(0.57735,0.57735,0.57735;2.0944rad)
  Profile = -> Sketch002
  ReferenceAxis = -> Sketch002 [N_Axis]
  Reversed = true
  Type = 0
FEATURE [PartDesign::Mirrored] Mirrored
  MirrorPlane = -> Sketch002 [V_Axis]
  Placement = pos=(0,0,0) rot=(1,1,1;2.0944rad)
FEATURE [PartDesign::LinearPattern] LinearPattern
  Direction = -> Y_Axis
  Length = 9.6
  Occurrences = 4
  Placement = pos=(0,0,0) rot=(1,1,1;2.0944rad)
FEATURE [PartDesign::MultiTransform] MultiTransform
  BaseFeature = -> Pad002
  Originals = -> [Pad002]
  Placement = pos=(0,0,0) rot=(0.57735,0.57735,0.57735;2.0944rad)
  Transformations = -> [Mirrored,LinearPattern]
FEATURE [PartDesign::Body] Body  label="TRRS-PJ-313B"
  Group = -> [Sketch,Pad,Sketch001,Pad001,Sketch002,Pad002,MultiTransform,Mirrored,LinearPattern]
  Origin = -> Origin
  Tip = -> MultiTransform
FEATURE [Part::Refine] MultiTransform001  label="TRRS-PJ-313BN"
  Source = -> MultiTransform
FEATURE [Sketcher::SketchObject] Sketch003
  FullyConstrained = true
  MapMode = 5
  Placement = pos=(0,0,0) rot=(1,0,0;1.5708rad)
  Support = -> [XZ_Plane001]
  sketch-geometry (1):
    g0: Circle CenterX=0 CenterY=2.5 CenterZ=0 NormalX=0 NormalY=0 NormalZ=1 AngleXU=0 Radius=2.5
  constraints (3):
    c: Diameter(g0) = 5
    c: DistanceY(g-1,g0) = 2.5
    c: Vertical(g0,g-1)
FEATURE [Sketcher::SketchObject] Sketch004
  AttachmentOffset = pos=(0,0,-3) rot=(0,0,1;0rad)
  FullyConstrained = true
  MapMode = 5
  Placement = pos=(0,3,7e-16) rot=(1,0,0;1.5708rad)
  Support = -> [XZ_Plane001]
  sketch-geometry (1):
    g0: Circle CenterX=0 CenterY=2.5 CenterZ=0 NormalX=0 NormalY=0 NormalZ=1 AngleXU=0 Radius=3
  constraints (3):
    c: Diameter(g0) = 6
    c: DistanceY(g-1,g0) = 2.5
    c: Vertical(g0,g-1)
FEATURE [PartDesign::AdditiveLoft] AdditiveLoft
  Closed = false
  Placement = pos=(0,0,0) rot=(1,0,0;1.5708rad)
  Profile = -> Sketch003
  Ruled = false
  Sections = -> [Sketch004]
FEATURE [PartDesign::Body] Body001  label="TRRS-Cutter"
  Group = -> [Sketch003,Sketch004,AdditiveLoft]
  Origin = -> Origin001
  Placement = pos=(0,6.5,0) rot=(0,0,1;0rad)
  Tip = -> AdditiveLoft
FEATURE [Part::Refine] Body002  label="TRRS-CutterN"
  Source = -> Body001
FEATURE [App::DocumentObjectGroup] Group  label="Parts"
  Group = -> [Body,Body001]
FEATURE [App::DocumentObjectGroup] Group001  label="Refined Copies"
  Group = -> [Body002,MultiTransform001]
---- part ../components/RP2040_Zero.FCStd = doc fcstd_b2b133973415 ----
FCSTD DOCUMENT  (FreeCAD 0.21R33668 +26 (Git))
Label: RP2040_Zero
License: All rights reserved
LicenseURL: http://en.wikipedia.org/wiki/All_rights_reserved
objects: App::DocumentObjectGroup×2, Mesh::Feature×1, Part::Feature×1, Part::Refine×1
note: 2 computed .brp shape members not serialized (recipe doc carries the construction recipe); baked Part::Feature solids carry a one-line shape summary decoded from their .brp

FEATURE [Mesh::Feature] Mesh  label="RP2040_ZERO_ASM (Meshed)"
FEATURE [Part::Feature] Mesh001  label="RP2040_ZERO_ASM (Solid)"
  shape: bbox 18.03 x 24.72 x 5.341 mm, 18906 faces, 0 solids (baked)
FEATURE [Part::Refine] Mesh002  label="RP2040-ZERO-N"
  Source = -> Mesh001
FEATURE [App::DocumentObjectGroup] Group  label="Original"
  Group = -> [Mesh001,Mesh]
FEATURE [App::DocumentObjectGroup] Group001  label="Refined Copy"
  Group = -> [Mesh002]
---- part ../components/USBC-Breakout.FCStd = doc fcstd_dd3c5fc311b9 ----
FCSTD DOCUMENT  (FreeCAD 0.21R33668 +26 (Git))
Label: USBC-Breakout
License: All rights reserved
LicenseURL: http://en.wikipedia.org/wiki/All_rights_reserved
objects: Sketcher::SketchObject×8, PartDesign::Pad×5, PartDesign::Body×3, Part::Refine×3, PartDesign::AdditiveLoft×2, PartDesign::Pocket×1, PartDesign::LinearPattern×1, Spreadsheet::Sheet×1
note: 31 computed .brp shape members not serialized (recipe doc carries the construction recipe); baked Part::Feature solids carry a one-line shape summary decoded from their .brp

FEATURE [Sketcher::SketchObject] Sketch
  FullyConstrained = true
  MapMode = 5
  Support = -> [XY_Plane]
  sketch-geometry (4):
    g0: LineSegment StartX=-6 StartY=6.83 StartZ=0 EndX=6 EndY=6.83 EndZ=0
    g1: LineSegment StartX=6 StartY=6.83 StartZ=0 EndX=6 EndY=-6.83 EndZ=0
    g2: LineSegment StartX=6 StartY=-6.83 StartZ=0 EndX=-6 EndY=-6.83 EndZ=0
    g3: LineSegment StartX=-6 StartY=-6.83 StartZ=0 EndX=-6 EndY=6.83 EndZ=0
  constraints (11):
    c: Coincident(g0,g1)
    c: Coincident(g1,g2)
    c: Coincident(g2,g3)
    c: Coincident(g3,g0)
    c: Horizontal(g0)
    c: Horizontal(g2)
    c: Vertical(g1)
    c: Vertical(g3)
    c: Symmetric(g0,g1,g-1)
    c: DistanceX(g0,g0) = 12
    c: DistanceY(g3,g3) = 13.66
FEATURE [PartDesign::Pad] Pad  label="Board"
  Direction = (0,0,1)
  Length = 1
  Length2 = 10
  Profile = -> Sketch
  ReferenceAxis = -> Sketch [N_Axis]
  Type = 0
FEATURE [Sketcher::SketchObject] Sketch001
  AttachmentOffset = pos=(0,0,0.7) rot=(0,0,1;0rad)
  FullyConstrained = true
  MapMode = 5
  Placement = pos=(0,-7.53,2e-16) rot=(1,0,0;1.5708rad)
  Support = -> [Pad]
  sketch-geometry (11):
    g0: LineSegment StartX=-3.25 StartY=4 StartZ=0 EndX=3.25 EndY=4 EndZ=0
    g1: LineSegment StartX=4.5 StartY=2.75 StartZ=0 EndX=4.5 EndY=2.25 EndZ=0
    g2: LineSegment StartX=3.25 StartY=1 StartZ=0 EndX=-3.25 EndY=1 EndZ=0
    g3: LineSegment StartX=-4.5 StartY=2.25 StartZ=0 EndX=-4.5 EndY=2.75 EndZ=0
    g4: ArcOfCircle CenterX=-3.25 CenterY=2.75 CenterZ=0 NormalX=0 NormalY=0 NormalZ=1 AngleXU=0 Radius=1.25 StartAngle=1.5708 EndAngle=3.14159
    g5: GeomPoint X=-4.5 Y=4 Z=0
    g6: ArcOfCircle CenterX=3.25 CenterY=2.25 CenterZ=0 NormalX=0 NormalY=0 NormalZ=1 AngleXU=0 Radius=1.25 StartAngle=4.71239 EndAngle=6.28319
    g7: GeomPoint X=4.5 Y=1 Z=0
    g8: ArcOfCircle CenterX=3.25 CenterY=2.75 CenterZ=0 NormalX=0 NormalY=0 NormalZ=1 AngleXU=0 Radius=1.25 StartAngle=0 EndAngle=1.5708
    g9: ArcOfCircle CenterX=-3.25 CenterY=2.25 CenterZ=0 NormalX=0 NormalY=0 NormalZ=1 AngleXU=0 Radius=1.25 StartAngle=3.14159 EndAngle=4.71239
    g10: GeomPoint X=0 Y=2.5 Z=0
  constraints (25):
    c: Horizontal(g0)
    c: Horizontal(g2)
    c: Vertical(g1)
    c: Vertical(g3)
    c: PointOnObject(g5,g3)
    c: PointOnObject(g5,g0)
    c: Tangent(g3,g4) = 1.5708
    c: Tangent(g0,g4) = 1.5708
    c: PointOnObject(g7,g2)
    c: PointOnObject(g7,g1)
    c: Tangent(g2,g6) = 1.5708
    c: Tangent(g1,g6) = 1.5708
    c: Tangent(g0,g8) = 1.5708
    c: Tangent(g1,g8) = 1.5708
    c: Tangent(g3,g9) = 1.5708
    c: Tangent(g2,g9) = 1.5708
    c: Equal(g8,g4)
    c: Equal(g8,g6)
    c: Equal(g6,g9)
    c: Radius(g8) = 1.25
    c: DistanceX(g5,g7) = 9
    c: DistanceY(g7,g5) = 3
    c: Symmetric(g5,g7,g10)
    c: Vertical(g10,g-1)
    c: DistanceY(g-1,g10) = 2.5
FEATURE [PartDesign::Pad] Pad001  label="USBC"
  BaseFeature = -> Pad
  Direction = (0,-1,2e-16)
  Length = 7
  Length2 = 10
  Profile = -> Sketch001
  ReferenceAxis = -> Sketch001 [N_Axis]
  Reversed = true
  Type = 0
FEATURE [Sketcher::SketchObject] Sketch002
  ExternalGeometry = -> [Pad001]
  FullyConstrained = true
  MapMode = 5
  Placement = pos=(0,0,1) rot=(0,0,1;0rad)
  Support = -> [Pad001]
  sketch-geometry (1):
    g0: Circle CenterX=-4 CenterY=4.83 CenterZ=0 NormalX=0 NormalY=0 NormalZ=1 AngleXU=0 Radius=0.5
  constraints (3):
    c: Radius(g0) = 0.5
    c: DistanceX(g-3,g0) = 2
    c: DistanceY(g0,g-3) = 2
FEATURE [PartDesign::Pocket] Pocket  label="Hole"
  BaseFeature = -> Pad001
  Direction = (0,0,-1)
  Length = 5
  Length2 = 5
  Profile = -> Sketch002
  ReferenceAxis = -> Sketch002 [N_Axis]
  Type = 1
FEATURE [PartDesign::LinearPattern] LinearPattern  label="Holes"
  BaseFeature = -> Pocket
  Direction = -> Sketch002 [H_Axis]
  Length = 8
  Occurrences = 4
  Originals = -> [Pocket]
FEATURE [PartDesign::Body] Body  label="USBCBreakout"
  Group = -> [Sketch,Pad,Sketch001,Pad001,Sketch002,Pocket,LinearPattern]
  Origin = -> Origin
  Tip = -> LinearPattern
FEATURE [Part::Refine] Body001  label="USBCBreakoutNice"
  Source = -> Body
FEATURE [Spreadsheet::Sheet] Spreadsheet  label="S"
  cells = A1='Label; B1='Value; C1='Type; D1='Description; A2='StopperThk; B2(StopperThk)==3 mm; C2='Input; D2='Thickness of the stopper wall; A3='StopperHei; B3(StopperHei)==4 mm; C3='Input; D3='Height of the stopper off the floor; A4='StopperLen; B4(StopperLen)==3 mm; C4='Input; D4='Length that the stopper extends from the end; A5='LifterLen; B5(LifterLen)==12 mm; C5='Input; D5='Lifting pad to prop up the breakout board; A6='LifterHei; B6(LifterHei)==2 mm; C6='Input; D6='Lifting pad to prop up the breakout board; A8='USBWid; B8(USBWid)==10.7 mm; C8='Input; D8='USB-C Connector cutout; A9='USBHei; B9(USBHei)==4.8 mm; C9='Input; D9='USB-C Connector cutout; A10='USBRad; B10(USBRad)==2 mm; C10='Input; D10='USB-C Connector cutout; A11='USBChamDim1; B11(USBChamDim1)==1 mm; C11='Input; D11='USBC Connector Chamfer; A12='USBChamDim2; B12(USBChamDim2)==3 mm; C12='Input; A13='USBLen; B13(USBLen)==10 mm; C13='Input; D13='Length of the USB Connector cutout to penetrate wall
FEATURE [Sketcher::SketchObject] Sketch003
  AttachmentOffset = pos=(0,0,4) rot=(0,0,1;0rad)
  FullyConstrained = true
  MapMode = 5
  Placement = pos=(0,0,4) rot=(0,0,1;0rad)
  Support = -> [XY_Plane001]
  expr: .AttachmentOffset.Base.z = <<S>>.StopperHei
  expr: Constraints[17] = <<S>>.StopperThk
  expr: Constraints[18] = <<S>>.StopperLen
  expr: Constraints[23] = <<S>>.StopperThk
  sketch-geometry (9):
    g0: LineSegment StartX=-9.325 StartY=10.25 StartZ=0 EndX=9.325 EndY=10.25 EndZ=0
    g1: LineSegment StartX=9.325 StartY=10.25 StartZ=0 EndX=9.325 EndY=4.25 EndZ=0
    g2: LineSegment StartX=9.325 StartY=4.25 StartZ=0 EndX=6.325 EndY=4.25 EndZ=0
    g3: LineSegment StartX=6.325 StartY=4.25 StartZ=0 EndX=6.325 EndY=7.25 EndZ=0
    g4: LineSegment StartX=6.325 StartY=7.25 StartZ=0 EndX=-6.325 EndY=7.25 EndZ=0
    g5: LineSegment StartX=-6.325 StartY=7.25 StartZ=0 EndX=-6.325 EndY=4.25 EndZ=0
    g6: LineSegment StartX=-6.325 StartY=4.25 StartZ=0 EndX=-9.325 EndY=4.25 EndZ=0
    g7: LineSegment StartX=-9.325 StartY=4.25 StartZ=0 EndX=-9.325 EndY=10.25 EndZ=0
    g8: GeomPoint X=0 Y=7.25 Z=0
  constraints (25):
    c: Horizontal(g0)
    c: Coincident(g0,g1)
    c: Vertical(g1)
    c: Coincident(g1,g2)
    c: Horizontal(g2)
    c: Coincident(g2,g3)
    c: Vertical(g3)
    c: Coincident(g3,g4)
    c: Horizontal(g4)
    c: Coincident(g4,g5)
    c: Coincident(g5,g6)
    c: Horizontal(g6)
    c: Coincident(g6,g7)
    c: Coincident(g7,g0)
    c: Vertical(g7)
    c: Vertical(g5)
    c: Equal(g6,g2)
    c: DistanceX(g2,g2) = 3
    c: DistanceY(g3,g3) = 3
    c: Equal(g3,g5)
    c: PointOnObject(g8,g-2)
    c: DistanceY(g-1,g8) = 7.25
    c: Symmetric(g4,g3,g8)
    c: DistanceY(g3,g0) = 3
    c: DistanceX(g4,g4) = 12.65
FEATURE [Sketcher::SketchObject] Sketch004
  FullyConstrained = true
  MapMode = 5
  Support = -> [XY_Plane001]
  expr: Constraints[17] = <<S>>.StopperThk * 2
  expr: Constraints[18] = <<S>>.StopperLen
  expr: Constraints[23] = <<S>>.StopperThk * 2
  sketch-geometry (9):
    g0: LineSegment StartX=-12.325 StartY=13.25 StartZ=0 EndX=12.325 EndY=13.25 EndZ=0
    g1: LineSegment StartX=12.325 StartY=13.25 StartZ=0 EndX=12.325 EndY=4.25 EndZ=0
    g2: LineSegment StartX=12.325 StartY=4.25 StartZ=0 EndX=6.325 EndY=4.25 EndZ=0
    g3: LineSegment StartX=6.325 StartY=4.25 StartZ=0 EndX=6.325 EndY=7.25 EndZ=0
    g4: LineSegment StartX=6.325 StartY=7.25 StartZ=0 EndX=-6.325 EndY=7.25 EndZ=0
    g5: LineSegment StartX=-6.325 StartY=7.25 StartZ=0 EndX=-6.325 EndY=4.25 EndZ=0
    g6: LineSegment StartX=-6.325 StartY=4.25 StartZ=0 EndX=-12.325 EndY=4.25 EndZ=0
    g7: LineSegment StartX=-12.325 StartY=4.25 StartZ=0 EndX=-12.325 EndY=13.25 EndZ=0
    g8: GeomPoint X=0 Y=7.25 Z=0
  constraints (25):
    c: Horizontal(g0)
    c: Coincident(g0,g1)
    c: Vertical(g1)
    c: Coincident(g1,g2)
    c: Horizontal(g2)
    c: Coincident(g2,g3)
    c: Vertical(g3)
    c: Coincident(g3,g4)
    c: Horizontal(g4)
    c: Coincident(g4,g5)
    c: Coincident(g5,g6)
    c: Horizontal(g6)
    c: Coincident(g6,g7)
    c: Coincident(g7,g0)
    c: Vertical(g7)
    c: Vertical(g5)
    c: Equal(g6,g2)
    c: DistanceX(g2,g2) = 6
    c: DistanceY(g3,g3) = 3
    c: Equal(g3,g5)
    c: PointOnObject(g8,g-2)
    c: DistanceY(g-1,g8) = 7.25
    c: Symmetric(g4,g3,g8)
    c: DistanceY(g3,g0) = 6
    c: DistanceX(g4,g4) = 12.65
FEATURE [PartDesign::AdditiveLoft] AdditiveLoft
  Closed = false
  Profile = -> Sketch003
  Ruled = false
  Sections = -> [Sketch004]
FEATURE [Sketcher::SketchObject] Sketch005  label="SketchOD"
  AttachmentOffset = pos=(0,0,3) rot=(0,0,1;0rad)
  FullyConstrained = true
  MapMode = 5
  Placement = pos=(0,-3,-7e-16) rot=(1,0,0;1.5708rad)
  Support = -> [XZ_Plane002]
  expr: .AttachmentOffset.Base.z = <<S>>.USBChamDim2
  expr: .Constraints.USBHei = <<S>>.USBHei + <<S>>.USBChamDim1 * 2
  expr: .Constraints.USBRad = <<S>>.USBRad + <<S>>.USBChamDim1
  expr: .Constraints.USBWid = <<S>>.USBWid + <<S>>.USBChamDim1 * 2
  sketch-geometry (11):
    g0: ArcOfCircle CenterX=-3.35 CenterY=2.9 CenterZ=0 NormalX=0 NormalY=0 NormalZ=1 AngleXU=0 Radius=3 StartAngle=1.5708 EndAngle=3.14159
    g1: LineSegment StartX=-3.35 StartY=5.9 StartZ=0 EndX=3.35 EndY=5.9 EndZ=0
    g2: ArcOfCircle CenterX=3.35 CenterY=2.9 CenterZ=0 NormalX=0 NormalY=0 NormalZ=1 AngleXU=0 Radius=3 StartAngle=1.124e-13 EndAngle=1.5708
    g3: LineSegment StartX=6.35 StartY=2.9 StartZ=0 EndX=6.35 EndY=2.1 EndZ=0
    g4: ArcOfCircle CenterX=3.35 CenterY=2.1 CenterZ=0 NormalX=0 NormalY=0 NormalZ=1 AngleXU=0 Radius=3 StartAngle=4.71239 EndAngle=6.28319
    g5: LineSegment StartX=3.35 StartY=-0.9 StartZ=0 EndX=-3.35 EndY=-0.9 EndZ=0
    g6: ArcOfCircle CenterX=-3.35 CenterY=2.1 CenterZ=0 NormalX=0 NormalY=0 NormalZ=1 AngleXU=0 Radius=3 StartAngle=3.14159 EndAngle=4.71239
    g7: LineSegment StartX=-6.35 StartY=2.1 StartZ=0 EndX=-6.35 EndY=2.9 EndZ=0
    g8: GeomPoint X=-6.35 Y=5.9 Z=0
    g9: GeomPoint X=6.35 Y=-0.9 Z=0
    g10: GeomPoint X=0 Y=2.5 Z=0
  constraints (25):
    c: Tangent(g0,g1) = 1.5708
    c: Tangent(g1,g2) = 1.5708
    c: Tangent(g2,g3) = 1.5708
    c: Tangent(g3,g4) = 1.5708
    c: Tangent(g4,g5) = 1.5708
    c: Tangent(g5,g6) = 1.5708
    c: Tangent(g6,g7) = 1.5708
    c: Tangent(g7,g0) = 1.5708
    c: Horizontal(g1)
    c: Horizontal(g5)
    c: Vertical(g3)
    c: Vertical(g7)
    c: Equal(g0,g2)
    c: Equal(g2,g4)
    c: Equal(g4,g6)
    c: PointOnObject(g8,g1)
    c: PointOnObject(g8,g7)
    c: PointOnObject(g9,g3)
    c: PointOnObject(g9,g5)
    c: Radius(g2) = 3  'USBRad'
    c: DistanceX(g8,g9) = 12.7  'USBWid'
    c: DistanceY(g9,g8) = 6.8  'USBHei'
    c: PointOnObject(g10,g-2)
    c: DistanceY(g-1,g10) = 2.5
    c: Symmetric(g8,g9,g10)
FEATURE [Sketcher::SketchObject] Sketch006  label="SketchID"
  AttachmentOffset = pos=(0,0,0.5) rot=(0,0,1;0rad)
  FullyConstrained = true
  MapMode = 5
  Placement = pos=(0,-0.5,-1e-16) rot=(1,0,0;1.5708rad)
  Support = -> [XZ_Plane002]
  expr: .Constraints.USBHei = <<S>>.USBHei
  expr: .Constraints.USBRad = <<S>>.USBRad
  expr: .Constraints.USBWid = <<S>>.USBWid
  sketch-geometry (11):
    g0: ArcOfCircle CenterX=-3.35 CenterY=2.9 CenterZ=0 NormalX=0 NormalY=0 NormalZ=1 AngleXU=0 Radius=2 StartAngle=1.5708 EndAngle=3.14159
    g1: LineSegment StartX=-3.35 StartY=4.9 StartZ=0 EndX=3.35 EndY=4.9 EndZ=0
    g2: ArcOfCircle CenterX=3.35 CenterY=2.9 CenterZ=0 NormalX=0 NormalY=0 NormalZ=1 AngleXU=0 Radius=2 StartAngle=0 EndAngle=1.5708
    g3: LineSegment StartX=5.35 StartY=2.9 StartZ=0 EndX=5.35 EndY=2.1 EndZ=0
    g4: ArcOfCircle CenterX=3.35 CenterY=2.1 CenterZ=0 NormalX=0 NormalY=0 NormalZ=1 AngleXU=0 Radius=2 StartAngle=4.71239 EndAngle=6.28319
    g5: LineSegment StartX=3.35 StartY=0.1 StartZ=0 EndX=-3.35 EndY=0.1 EndZ=0
    g6: ArcOfCircle CenterX=-3.35 CenterY=2.1 CenterZ=0 NormalX=0 NormalY=0 NormalZ=1 AngleXU=0 Radius=2 StartAngle=3.14159 EndAngle=4.71239
    g7: LineSegment StartX=-5.35 StartY=2.1 StartZ=0 EndX=-5.35 EndY=2.9 EndZ=0
    g8: GeomPoint X=-5.35 Y=4.9 Z=0
    g9: GeomPoint X=5.35 Y=0.1 Z=0
    g10: GeomPoint X=0 Y=2.5 Z=0
  constraints (25):
    c: Tangent(g0,g1) = 1.5708
    c: Tangent(g1,g2) = 1.5708
    c: Tangent(g2,g3) = 1.5708
    c: Tangent(g3,g4) = 1.5708
    c: Tangent(g4,g5) = 1.5708
    c: Tangent(g5,g6) = 1.5708
    c: Tangent(g6,g7) = 1.5708
    c: Tangent(g7,g0) = 1.5708
    c: Horizontal(g1)
    c: Horizontal(g5)
    c: Vertical(g3)
    c: Vertical(g7)
    c: Equal(g0,g2)
    c: Equal(g2,g4)
    c: Equal(g4,g6)
    c: PointOnObject(g8,g1)
    c: PointOnObject(g8,g7)
    c: PointOnObject(g9,g3)
    c: PointOnObject(g9,g5)
    c: Radius(g2) = 2  'USBRad'
    c: DistanceX(g8,g9) = 10.7  'USBWid'
    c: DistanceY(g9,g8) = 4.8  'USBHei'
    c: PointOnObject(g10,g-2)
    c: DistanceY(g-1,g10) = 2.5
    c: Symmetric(g8,g9,g10)
FEATURE [PartDesign::AdditiveLoft] AdditiveLoft001
  Closed = false
  Placement = pos=(0,0,0) rot=(1,0,0;1.5708rad)
  Profile = -> Sketch005
  Ruled = false
  Sections = -> [Sketch006]
FEATURE [PartDesign::Pad] Pad002  label="PadInside"
  BaseFeature = -> AdditiveLoft001
  Direction = (0,1,2e-16)
  Length = 10
  Length2 = 10
  Placement = pos=(0,0,0) rot=(1,0,0;1.5708rad)
  Profile = -> AdditiveLoft001 [Face3]
  Type = 0
  expr: Length = <<S>>.USBLen
FEATURE [PartDesign::Pad] Pad003  label="PadOutside"
  BaseFeature = -> Pad002
  Direction = (0,-1,-2e-16)
  Length = 10
  Length2 = 10
  Placement = pos=(0,0,0) rot=(1,0,0;1.5708rad)
  Profile = -> Pad002 [Face1]
  Type = 0
  expr: Length = <<S>>.USBLen
FEATURE [PartDesign::Body] Body003  label="StopperCut"
  Group = -> [Sketch005,Sketch006,AdditiveLoft001,Pad002,Pad003]
  Origin = -> Origin002
  Placement = pos=(0,-18,0) rot=(0,0,1;0rad)
  Tip = -> Pad003
FEATURE [Part::Refine] Body005  label="StopperCutNice"
  Source = -> Body003
FEATURE [Sketcher::SketchObject] Sketch007
  ExternalGeometry = -> [AdditiveLoft]
  FullyConstrained = true
  MapMode = 5
  Placement = pos=(0,7.25,0) rot=(1,0,0;1.5708rad)
  Support = -> [AdditiveLoft]
  expr: .Constraints.LifterHei = <<S>>.LifterHei
  sketch-geometry (4):
    g0: LineSegment StartX=-6.325 StartY=0 StartZ=0 EndX=6.325 EndY=0 EndZ=0
    g1: LineSegment StartX=6.325 StartY=0 StartZ=0 EndX=6.325 EndY=2 EndZ=0
    g2: LineSegment StartX=6.325 StartY=2 StartZ=0 EndX=-6.325 EndY=2 EndZ=0
    g3: LineSegment StartX=-6.325 StartY=2 StartZ=0 EndX=-6.325 EndY=0 EndZ=0
  constraints (10):
    c: Coincident(g0,g1)
    c: Coincident(g1,g2)
    c: Coincident(g2,g3)
    c: Coincident(g3,g0)
    c: Horizontal(g2)
    c: Vertical(g1)
    c: Vertical(g3)
    c: Coincident(g0,g-3)
    c: Coincident(g0,g-3)
    c: DistanceY(g1,g1) = 2  'LifterHei'
FEATURE [PartDesign::Pad] Pad004
  BaseFeature = -> AdditiveLoft
  Direction = (0,-1,2e-16)
  Length = 12
  Length2 = 10
  Profile = -> Sketch007
  ReferenceAxis = -> Sketch007 [N_Axis]
  Type = 0
  expr: Length = <<S>>.LifterLen
FEATURE [PartDesign::Body] Body002  label="StopperAdd"
  Group = -> [Sketch003,Sketch004,AdditiveLoft,Sketch007,Pad004]
  Origin = -> Origin001
  Tip = -> Pad004
FEATURE [Part::Refine] Body004  label="StopperAddNice"
  Source = -> Body002
---- part HeatsetInserts.FCStd = doc fcstd_f25918f00fb6 ----
FCSTD DOCUMENT  (FreeCAD 0.21R33668 +26 (Git))
Label: HeatsetInserts
License: All rights reserved
LicenseURL: http://en.wikipedia.org/wiki/All_rights_reserved
objects: Sketcher::SketchObject×6, PartDesign::Pad×4, PartDesign::Body×4, Part::Cut×2, Part::Refine×2, App::DocumentObjectGroup×2, PartDesign::Chamfer×1, PartDesign::AdditiveLoft×1
note: 26 computed .brp shape members not serialized (recipe doc carries the construction recipe); baked Part::Feature solids carry a one-line shape summary decoded from their .brp

FEATURE [Sketcher::SketchObject] Sketch003
  FullyConstrained = true
  MapMode = 5
  Support = -> [XY_Plane001]
  expr: Constraints[1] = 6 mm
  expr: Constraints[3] = 3.4 mm
  sketch-geometry (2):
    g0: Circle CenterX=0 CenterY=0 CenterZ=0 NormalX=0 NormalY=0 NormalZ=1 AngleXU=0 Radius=3
    g1: Circle CenterX=0 CenterY=0 CenterZ=0 NormalX=0 NormalY=0 NormalZ=1 AngleXU=0 Radius=1.7
  constraints (4):
    c: Coincident(g0,g-1)
    c: Diameter(g0) = 6
    c: Coincident(g1,g0)
    c: Diameter(g1) = 3.4
FEATURE [PartDesign::Pad] Pad001
  Direction = (0,0,1)
  Length = 5
  Length2 = 10
  Profile = -> Sketch003
  ReferenceAxis = -> Sketch003 [N_Axis]
  Type = 0
  expr: Length = 5 mm
FEATURE [PartDesign::Chamfer] Chamfer001
  Angle = 8
  Base = -> Pad001 [Edge5]
  BaseFeature = -> Pad001
  ChamferType = 2
  FlipDirection = false
  Size = 3
  Size2 = 1
  SupportTransform = false
  UseAllEdges = false
  expr: Angle = 8 °
  expr: Size = 3 mm
FEATURE [PartDesign::Body] Body001  label="HeatInsert"
  Group = -> [Sketch003,Pad001,Chamfer001]
  Origin = -> Origin001
  Placement = pos=(0,-1.1e-15,-3) rot=(0,0,1;0rad)
  Tip = -> Chamfer001
FEATURE [Sketcher::SketchObject] Sketch
  FullyConstrained = true
  MapMode = 5
  Support = -> [XY_Plane]
  sketch-geometry (1):
    g0: Circle CenterX=0 CenterY=0 CenterZ=0 NormalX=0 NormalY=0 NormalZ=1 AngleXU=0 Radius=1.7
  constraints (2):
    c: Coincident(g0,g-1)
    c: Radius(g0) = 1.7
FEATURE [PartDesign::Pad] Pad
  Direction = (0,0,1)
  Length = 2
  Length2 = 10
  Profile = -> Sketch
  ReferenceAxis = -> Sketch [N_Axis]
  Type = 0
FEATURE [Sketcher::SketchObject] Sketch004
  AttachmentOffset = pos=(0,0,-3) rot=(0,0,1;0rad)
  FullyConstrained = true
  MapMode = 5
  Placement = pos=(0,0,-3) rot=(0,0,1;0rad)
  Support = -> [XY_Plane]
  sketch-geometry (1):
    g0: Circle CenterX=0 CenterY=0 CenterZ=0 NormalX=0 NormalY=0 NormalZ=1 AngleXU=0 Radius=2.1
  constraints (2):
    c: Coincident(g0,g-1)
    c: Radius(g0) = 2.1
FEATURE [Sketcher::SketchObject] Sketch005
  FullyConstrained = true
  MapMode = 5
  Support = -> [XY_Plane]
  sketch-geometry (1):
    g0: Circle CenterX=0 CenterY=0 CenterZ=0 NormalX=0 NormalY=0 NormalZ=1 AngleXU=0 Radius=1.7
  constraints (2):
    c: Coincident(g0,g-1)
    c: Radius(g0) = 1.7
FEATURE [PartDesign::AdditiveLoft] AdditiveLoft
  BaseFeature = -> Pad
  Closed = false
  Profile = -> Sketch005
  Ruled = false
  Sections = -> [Sketch004]
FEATURE [PartDesign::Body] Body  label="CutoutHeatset"
  Group = -> [Sketch,Pad,Sketch004,Sketch005,AdditiveLoft]
  Origin = -> Origin
  Tip = -> AdditiveLoft
FEATURE [Sketcher::SketchObject] Sketch006
  FullyConstrained = true
  MapMode = 5
  Support = -> [XY_Plane002]
  sketch-geometry (4):
    g0: ArcOfCircle CenterX=0 CenterY=0 CenterZ=0 NormalX=0 NormalY=0 NormalZ=1 AngleXU=0 Radius=4.5 StartAngle=0.349066 EndAngle=2.79253
    g1: LineSegment StartX=-4.22862 StartY=1.53909 StartZ=0 EndX=-6.97262 EndY=-6 EndZ=0
    g2: LineSegment StartX=-6.97262 StartY=-6 StartZ=0 EndX=6.97262 EndY=-6 EndZ=0
    g3: LineSegment StartX=6.97262 StartY=-6 StartZ=0 EndX=4.22862 EndY=1.53909 EndZ=0
  constraints (10):
    c: Coincident(g0,g-1)
    c: Tangent(g0,g1) = -1.5708
    c: Coincident(g1,g2)
    c: Horizontal(g2)
    c: Coincident(g2,g3)
    c: Angle(g3,g2) = 1.22173
    c: Angle(g2,g1) = 1.22173
    c: Radius(g0) = 4.5
    c: DistanceY(g2,g0) = 6
    c: Tangent(g3,g0) = -1.5708
FEATURE [PartDesign::Pad] Pad002
  Direction = (0,0,1)
  Length = 7
  Length2 = 10
  Midplane = true
  Profile = -> Sketch006
  ReferenceAxis = -> Sketch006 [N_Axis]
  Type = 0
FEATURE [PartDesign::Body] Body002  label="AddHeatset"
  Group = -> [Sketch006,Pad002]
  Origin = -> Origin002
  Placement = pos=(0,0,0.5) rot=(0,0,1;0rad)
  Tip = -> Pad002
FEATURE [Part::Cut] Cut  label="HeatsetPart"
  Base = -> Body002
  Tool = -> Body
FEATURE [Part::Refine] Cut001  label="HeatsetPartNice"
  Source = -> Cut
FEATURE [Sketcher::SketchObject] Sketch007
  FullyConstrained = true
  MapMode = 5
  Support = -> [XY_Plane003]
  sketch-geometry (1):
    g0: Circle CenterX=0 CenterY=0 CenterZ=0 NormalX=0 NormalY=0 NormalZ=1 AngleXU=0 Radius=4.5
  constraints (2):
    c: Radius(g0) = 4.5
    c: Coincident(g0,g-1)
FEATURE [PartDesign::Pad] Pad003
  Direction = (0,0,1)
  Length = 7
  Length2 = 10
  Midplane = true
  Profile = -> Sketch007
  ReferenceAxis = -> Sketch007 [N_Axis]
  Type = 0
FEATURE [PartDesign::Body] Body003  label="Body"
  Group = -> [Sketch007,Pad003]
  Origin = -> Origin003
  Placement = pos=(0,0,0.5) rot=(0,0,1;0rad)
  Tip = -> Pad003
FEATURE [Part::Cut] Cut002  label="HeatsetPartRound"
  Base = -> Body003
  Tool = -> Body
FEATURE [Part::Refine] Cut003  label="HeatsetPartRoundNice"
  Source = -> Cut002
FEATURE [App::DocumentObjectGroup] Group  label="Refined Copies"
  Group = -> [Cut001,Cut003]
FEATURE [App::DocumentObjectGroup] Group001  label="Working"
  Group = -> [Body001,Cut,Cut002]
---- part KeyColumn2.FCStd = doc fcstd_ef497381b1b0 ----
FCSTD DOCUMENT  (FreeCAD 0.21R33668 +26 (Git))
Label: KeyColumn2
License: All rights reserved
LicenseURL: http://en.wikipedia.org/wiki/All_rights_reserved
objects: App::Link×6, Sketcher::SketchObject×4, PartDesign::Body×4, Part::Compound×4, Part::Refine×3, PartDesign::SubShapeBinder×3, Part::Offset2D×2, Part::Extrusion×2, PartDesign::Pad×2, Part::Cut×2, App::DocumentObjectGroup×2, Spreadsheet::Sheet×1
note: 28 computed .brp shape members not serialized (recipe doc carries the construction recipe); baked Part::Feature solids carry a one-line shape summary decoded from their .brp
EXTERNAL_REF file=../components/MX_Switches.FCStd obj=Body008
EXTERNAL_REF file=../components/MX-Latch-Subtractor2.FCStd obj=Body001

FEATURE [Spreadsheet::Sheet] Spreadsheet  label="S"
  cells = B1=172.75; B2==180 - B1; B3=21; A4='Well Angle; B4(WellAngle)=159; C4='deg; D4=159; A5='Knucle Spacing; B5(KnuckleSpace)==7.25 mm; A6='End Slope; B6(EndSlope)=22.5; C6='deg; D6='Bottom palm; A7='End Slope B; B7(EndSlopeB)=22.5; C7='deg; D7='Top tips
FEATURE [Sketcher::SketchObject] Sketch
  FullyConstrained = true
  MapMode = 5
  Placement = pos=(0,0,0) rot=(0.57735,0.57735,0.57735;2.0944rad)
  Support = -> [YZ_Plane]
  expr: Constraints[14] = <<S>>.KnuckleSpace
  expr: Constraints[18] = <<S>>.WellAngle
  expr: Constraints[19] = <<S>>.WellAngle
  expr: Constraints[20] = <<S>>.EndSlopeB
  expr: Constraints[21] = <<S>>.EndSlope
  sketch-geometry (9):
    g0: LineSegment StartX=-29.8362 StartY=7.29053 StartZ=0 EndX=-12.0982 EndY=0.481542 EndZ=0
    g1: LineSegment StartX=-9.5 StartY=0 StartZ=0 EndX=9.5 EndY=0 EndZ=0
    g2: LineSegment StartX=12.0982 StartY=0.481542 StartZ=0 EndX=29.8362 EndY=7.29053 EndZ=0
    g3: ArcOfCircle CenterX=-32.4344 CenterY=0.522075 CenterZ=0 NormalX=0 NormalY=0 NormalZ=1 AngleXU=0 Radius=7.25 StartAngle=1.20428 EndAngle=1.9635
    g4: LineSegment StartX=-35.2088 StartY=7.2202 StartZ=0 EndX=-72.164 EndY=-8.08714 EndZ=0
    g5: ArcOfCircle CenterX=32.4344 CenterY=0.522075 CenterZ=0 NormalX=0 NormalY=0 NormalZ=1 AngleXU=0 Radius=7.25 StartAngle=1.1781 EndAngle=1.93732
    g6: LineSegment StartX=35.2088 StartY=7.2202 StartZ=0 EndX=52.6399 EndY=0 EndZ=0
    g7: ArcOfCircle CenterX=-9.5 CenterY=7.25 CenterZ=0 NormalX=0 NormalY=0 NormalZ=1 AngleXU=0 Radius=7.25 StartAngle=4.34587 EndAngle=4.71239
    g8: ArcOfCircle CenterX=9.5 CenterY=7.25 CenterZ=0 NormalX=0 NormalY=0 NormalZ=1 AngleXU=0 Radius=7.25 StartAngle=4.71239 EndAngle=5.07891
  constraints (23):
    c: Horizontal(g1)
    c: Symmetric(g1,g1,g-1)
    c: Equal(g1,g2)
    c: Equal(g1,g0)
    c: Tangent(g4,g3) = -1.5708
    c: Tangent(g6,g5) = 1.5708
    c: PointOnObject(g6,g-1)
    c: Tangent(g0,g3) = 1.5708
    c: Tangent(g5,g2) = 1.5708
    c: Tangent(g8,g2) = -1.5708
    c: Tangent(g8,g1) = -1.5708
    c: Tangent(g7,g1) = -1.5708
    c: Tangent(g7,g0) = -1.5708
    c: Distance(g1) = 19
    c: Radius(g3) = 7.25
    c: Equal(g3,g7)
    c: Equal(g7,g8)
    c: Equal(g8,g5)
    c: Angle(g1,g0) = 2.77507
    c: Angle(g2,g1) = 2.77507
    c: Angle(g6,g-1) = 0.392699
    c: Angle(g-1,g4) = 0.392699
    c: Distance(g4) = 40
FEATURE [PartDesign::Body] Body  label="SketchProfile"
  Group = -> [Sketch]
  Origin = -> Origin
FEATURE [Part::Offset2D] Offset2D
  Fill = false
  Intersection = false
  Join = 2
  Mode = 1
  SelfIntersection = false
  Source = -> Sketch
  Value = 1.8
FEATURE [Part::Extrusion] Extrude001  label="KeyColumnBase"
  Base = -> Offset2D
  Dir = (1,0,0)
  DirMode = 0
  FaceMakerClass = Part::FaceMakerBullseye
  LengthFwd = 19
  LengthRev = 0
  Solid = true
  Symmetric = true
FEATURE [App::Link] Link  label="MXSwitch100Nice"
  AttacherType = Attacher::AttachEngine3D
  LinkPlacement = pos=(3.6e-15,20.3221,5.56648) rot=(1,0,0;0.366519rad)
  LinkedObject = -> <external ../components/MX_Switches.FCStd>#Body008
  MapMode = 2
  Placement = pos=(3.6e-15,20.3221,5.56648) rot=(1,0,0;0.366519rad)
FEATURE [App::Link] Link001  label="MXSwitch100Nice001"
  AttacherType = Attacher::AttachEngine3D
  LinkPlacement = pos=(0,-1.8e-15,1.8) rot=(0,0,1;0rad)
  LinkedObject = -> Link
  MapMode = 2
  Placement = pos=(0,-1.8e-15,1.8) rot=(0,0,1;0rad)
FEATURE [App::Link] Link002  label="MXSwitch100Nice002"
  AttacherType = Attacher::AttachEngine3D
  LinkPlacement = pos=(-8.9e-15,-20.3221,5.56648) rot=(-1,0,0;0.366519rad)
  LinkedObject = -> Link001
  MapMode = 2
  Placement = pos=(-8.9e-15,-20.3221,5.56648) rot=(-1,0,0;0.366519rad)
FEATURE [App::Link] Link003  label="MX-Latch-Subtractor2N"
  AttacherType = Attacher::AttachEngine3D
  LinkPlacement = pos=(3.6e-15,20.3221,5.56648) rot=(1,0,0;0.366519rad)
  LinkedObject = -> <external ../components/MX-Latch-Subtractor2.FCStd>#Body001
  MapMode = 2
  Placement = pos=(3.6e-15,20.3221,5.56648) rot=(1,0,0;0.366519rad)
FEATURE [App::Link] Link004  label="MX-Latch-Subtractor2N001"
  AttacherType = Attacher::AttachEngine3D
  LinkPlacement = pos=(0,-1.8e-15,1.8) rot=(0,0,1;0rad)
  LinkedObject = -> Link003
  MapMode = 2
  Placement = pos=(0,-1.8e-15,1.8) rot=(0,0,1;0rad)
FEATURE [App::Link] Link005  label="MX-Latch-Subtractor2N002"
  AttacherType = Attacher::AttachEngine3D
  LinkPlacement = pos=(-8.9e-15,-20.3221,5.56648) rot=(-1,0,0;0.366519rad)
  LinkedObject = -> Link004
  MapMode = 2
  Placement = pos=(-8.9e-15,-20.3221,5.56648) rot=(-1,0,0;0.366519rad)
FEATURE [Part::Compound] Compound  label="MXSwitchC"
  Links = -> [Link,Link001,Link002]
FEATURE [Part::Compound] Compound001  label="SubtractorC"
  Links = -> [Link005,Link003,Link004]
FEATURE [Sketcher::SketchObject] Sketch001
  FullyConstrained = false
  MapMode = 5
  Placement = pos=(0,0,0) rot=(0.57735,0.57735,0.57735;2.0944rad)
  Support = -> [YZ_Plane002]
  expr: Constraints[17] = <<S>>.KnuckleSpace
  expr: Constraints[5] = <<S>>.KnuckleSpace
  sketch-geometry (7):
    g0: LineSegment StartX=-31.0713 StartY=7.8 StartZ=0 EndX=8.10798 EndY=0.13489 EndZ=0
    g1: LineSegment StartX=12.0982 StartY=0.481542 StartZ=0 EndX=29.8362 EndY=7.29053 EndZ=0
    g2: ArcOfCircle CenterX=-32.4633 CenterY=0.68489 CenterZ=0 NormalX=0 NormalY=0 NormalZ=1 AngleXU=0 Radius=7.25 StartAngle=1.37759 EndAngle=1.78024
    g3: LineSegment StartX=-33.9706 StartY=7.77646 StartZ=0 EndX=-53.5336 EndY=3.61823 EndZ=0
    g4: ArcOfCircle CenterX=32.4344 CenterY=0.522075 CenterZ=0 NormalX=0 NormalY=0 NormalZ=1 AngleXU=0 Radius=7.25 StartAngle=0.610865 EndAngle=1.93732
    g5: LineSegment StartX=38.3732 StartY=4.6805 StartZ=0 EndX=49.8447 EndY=-11.7025 EndZ=0
    g6: ArcOfCircle CenterX=9.5 CenterY=7.25 CenterZ=0 NormalX=0 NormalY=0 NormalZ=1 AngleXU=0 Radius=7.25 StartAngle=4.51919 EndAngle=5.07891
  constraints (18):
    c: Tangent(g3,g2) = -1.5708
    c: Tangent(g5,g4) = 1.5708
    c: Tangent(g0,g2) = 1.5708
    c: Tangent(g4,g1) = 1.5708
    c: Tangent(g6,g1) = -1.5708
    c: Radius(g2) = 7.25
    c: Equal(g6,g4)
    c: Angle(g5,g-1) = 0.959931
    c: Angle(g-1,g3) = 0.20944
    c: Distance(g1) = 19
    c: DistanceX(g1) = 12.0982
    c: DistanceY(g1) = 0.481542
    c: DistanceX(g1) = 29.8362
    c: Tangent(g6,g0) = -1.5708
    c: DistanceY(g-1,g0) = 7.8
    c: Distance(g3) = 20
    c: Distance(g5) = 20
    c: Radius(g4) = 7.25
FEATURE [PartDesign::Body] Body002  label="SketchProfileAlt"
  Group = -> [Sketch001]
  Origin = -> Origin002
FEATURE [Part::Offset2D] Offset2D001
  Fill = false
  Intersection = false
  Join = 0
  Mode = 1
  SelfIntersection = false
  Source = -> Sketch001
  Value = 1.8
FEATURE [Part::Extrusion] Extrude  label="KeyColumnBlank"
  Base = -> Offset2D001
  Dir = (1,-2e-16,2e-16)
  DirMode = 2
  FaceMakerClass = Part::FaceMakerBullseye
  LengthFwd = 19
  LengthRev = 0
  Solid = true
  Symmetric = true
FEATURE [Part::Refine] Extrude003  label="KeyColumnBlankN"
  Source = -> Extrude
FEATURE [PartDesign::SubShapeBinder] Binder
  BindCopyOnChange = 0
  BindMode = 0
  ClaimChildren = false
  Context = -> Body003 [Binder.]
  Fuse = false
  MakeFace = true
  OffsetFill = false
  OffsetIntersection = false
  OffsetJoinType = 0
  OffsetOpenResult = false
  PartialLoad = false
  Relative = true
  Support = -> [Extrude001[Face21]]
  _Version = 2
FEATURE [Sketcher::SketchObject] Sketch002
  ExternalGeometry = -> [Binder]
  FullyConstrained = true
  MapMode = 5
  Placement = pos=(0,0,0) rot=(0.57735,0.57735,0.57735;2.0944rad)
  Support = -> [YZ_Plane003]
  sketch-geometry (4):
    g0: LineSegment StartX=53.3288 StartY=1.66298 StartZ=0 EndX=56.6547 EndY=0.285323 EndZ=0
    g1: LineSegment StartX=56.6547 StartY=0.285323 StartZ=0 EndX=55.2771 EndY=-3.04064 EndZ=0
    g2: LineSegment StartX=55.2771 StartY=-3.04064 StartZ=0 EndX=51.9511 EndY=-1.66298 EndZ=0
    g3: LineSegment StartX=51.9511 StartY=-1.66298 StartZ=0 EndX=53.3288 EndY=1.66298 EndZ=0
  constraints (10):
    c: Coincident(g0,g-3)
    c: Coincident(g0,g1)
    c: Coincident(g1,g2)
    c: Coincident(g2,g-4)
    c: Coincident(g2,g3)
    c: Coincident(g3,g0)
    c: Perpendicular(g0,g3)
    c: Perpendicular(g2,g3)
    c: Perpendicular(g1,g2)
    c: Equal(g3,g0)
FEATURE [PartDesign::Pad] Pad
  Direction = (1,-2e-16,3e-16)
  Length = 20
  Length2 = 10
  Midplane = true
  Placement = pos=(0,0,0) rot=(0.57735,0.57735,0.57735;2.0944rad)
  Profile = -> Sketch002
  ReferenceAxis = -> Sketch002 [N_Axis]
  Type = 0
FEATURE [PartDesign::Body] Body003  label="TrimA"
  Group = -> [Binder,Sketch002,Pad]
  Origin = -> Origin003
  Tip = -> Pad
FEATURE [PartDesign::SubShapeBinder] Binder001
  BindCopyOnChange = 0
  BindMode = 0
  ClaimChildren = false
  Context = -> Body004 [Binder001.]
  Fuse = false
  MakeFace = true
  OffsetFill = false
  OffsetIntersection = false
  OffsetJoinType = 0
  OffsetOpenResult = false
  PartialLoad = false
  Relative = true
  _Version = 2
FEATURE [Sketcher::SketchObject] Sketch003
  ExternalGeometry = -> [Binder001]
  FullyConstrained = true
  MapMode = 5
  Placement = pos=(0,0,0) rot=(0.57735,0.57735,0.57735;2.0944rad)
  Support = -> [YZ_Plane004]
  sketch-geometry (4):
    g0: LineSegment StartX=-72.8528 StartY=-6.42415 StartZ=0 EndX=-71.4752 EndY=-9.75012 EndZ=0
    g1: LineSegment StartX=-71.4752 StartY=-9.75012 StartZ=0 EndX=-74.8011 EndY=-11.1278 EndZ=0
    g2: LineSegment StartX=-74.8011 StartY=-11.1278 StartZ=0 EndX=-76.1788 EndY=-7.80181 EndZ=0
    g3: LineSegment StartX=-76.1788 StartY=-7.80181 StartZ=0 EndX=-72.8528 EndY=-6.42415 EndZ=0
  constraints (10):
    c: Coincident(g0,g-3)
    c: Coincident(g0,g-4)
    c: Coincident(g0,g1)
    c: Coincident(g1,g2)
    c: Coincident(g2,g3)
    c: Coincident(g3,g0)
    c: Perpendicular(g0,g3)
    c: Perpendicular(g0,g1)
    c: Perpendicular(g1,g2)
    c: Equal(g0,g1)
FEATURE [PartDesign::Pad] Pad001
  Direction = (1,-2e-16,3e-16)
  Length = 20
  Length2 = 10
  Midplane = true
  Placement = pos=(0,0,0) rot=(0.57735,0.57735,0.57735;2.0944rad)
  Profile = -> Sketch003
  ReferenceAxis = -> Sketch003 [N_Axis]
  Type = 0
FEATURE [PartDesign::SubShapeBinder] Binder002
  BindCopyOnChange = 0
  BindMode = 0
  ClaimChildren = false
  Context = -> Body004 [Binder002.]
  Fuse = false
  MakeFace = true
  OffsetFill = false
  OffsetIntersection = false
  OffsetJoinType = 0
  OffsetOpenResult = false
  PartialLoad = false
  Relative = true
  Support = -> [Extrude001[Face21]]
  _Version = 2
FEATURE [PartDesign::Body] Body004  label="TrimB"
  Group = -> [Binder001,Sketch003,Pad001,Binder002]
  Origin = -> Origin004
  Tip = -> Pad001
FEATURE [Part::Compound] Compound002  label="EndTrimmers"
  Links = -> [Body003,Body004]
FEATURE [Part::Cut] Cut002  label="KeyColumnTrim"
  Base = -> Extrude001
  Tool = -> Compound002
FEATURE [Part::Cut] Cut004  label="KeyColumnCut"
  Base = -> Cut002
  Tool = -> Compound001
FEATURE [Part::Refine] Cut001  label="KeyColumnCutN"
  Source = -> Cut004
FEATURE [Part::Compound] Compound003  label="KeyColumnCaps"
  Links = -> [Cut002,Compound]
FEATURE [App::DocumentObjectGroup] Group001  label="Working"
  Group = -> [Cut004,Body,Compound,Body002,Extrude,Compound003]
FEATURE [Part::Refine] Compound004  label="KeyColumnCapsN"
  Source = -> Compound003
FEATURE [App::DocumentObjectGroup] Group  label="Refined Copies"
  Group = -> [Extrude003,Cut001,Compound004]
---- part KeyRowThumb2.FCStd = doc fcstd_83a99135e9f7 ----
FCSTD DOCUMENT  (FreeCAD 0.21R33668 +26 (Git))
Label: KeyRowThumb2
License: All rights reserved
LicenseURL: http://en.wikipedia.org/wiki/All_rights_reserved
objects: Sketcher::SketchObject×5, PartDesign::Body×4, App::Link×4, PartDesign::Pad×2, Part::MultiFuse×2, PartDesign::AdditiveLoft×2, Part::Cut×1, PartDesign::SubShapeBinder×1, Part::Refine×1
note: 22 computed .brp shape members not serialized (recipe doc carries the construction recipe); baked Part::Feature solids carry a one-line shape summary decoded from their .brp
EXTERNAL_REF file=../components/MX-Latch-Subtractor2.FCStd obj=Body001

FEATURE [Sketcher::SketchObject] Sketch
  FullyConstrained = false
  MapMode = 5
  Placement = pos=(0,0,0) rot=(1,0,0;1.5708rad)
  Support = -> [XZ_Plane]
  sketch-geometry (15):
    g0: LineSegment StartX=-9.5 StartY=2 StartZ=0 EndX=9.5 EndY=2 EndZ=0
    g1: LineSegment StartX=9.5 StartY=2 StartZ=0 EndX=9.5 EndY=-2 EndZ=0
    g2: LineSegment StartX=9.5 StartY=-2 StartZ=0 EndX=-9.5 EndY=-2 EndZ=0
    g3: LineSegment StartX=-9.5 StartY=-2 StartZ=0 EndX=-9.5 EndY=2 EndZ=0
    g4: LineSegment StartX=-17.2452 StartY=-3.99696 StartZ=0 EndX=-13.3726 EndY=-4.99848 EndZ=0
    g5: LineSegment StartX=-9.5 StartY=-2 StartZ=0 EndX=-9.5 EndY=-6 EndZ=0
    g6: LineSegment StartX=-17.2452 StartY=-3.99696 StartZ=0 EndX=-22.0024 EndY=-22.3918 EndZ=0
    g7: LineSegment StartX=-22.0024 StartY=-22.3918 StartZ=0 EndX=-18.1298 EndY=-23.3933 EndZ=0
    g8: LineSegment StartX=-18.1298 StartY=-23.3933 StartZ=0 EndX=-13.3726 EndY=-4.99848 EndZ=0
    g9: LineSegment StartX=9.5 StartY=2 StartZ=0 EndX=28.5 EndY=2 EndZ=0
    g10: LineSegment StartX=28.5 StartY=2 StartZ=0 EndX=28.5 EndY=-2 EndZ=0
    g11: LineSegment StartX=28.5 StartY=-2 StartZ=0 EndX=9.5 EndY=-2 EndZ=0
    g12: LineSegment StartX=9.5 StartY=-21 StartZ=0 EndX=9.5 EndY=-2 EndZ=0
    g13: ArcOfCircle CenterX=-9.5 CenterY=-6 CenterZ=0 NormalX=0 NormalY=0 NormalZ=1 AngleXU=0 Radius=4 StartAngle=1.5708 EndAngle=2.88852
    g14: ArcOfCircle CenterX=-9.5 CenterY=-6 CenterZ=0 NormalX=0 NormalY=0 NormalZ=1 AngleXU=0 Radius=8 StartAngle=1.5708 EndAngle=2.88852
  constraints (36):
    c: Coincident(g1,g2)
    c: Coincident(g2,g3)
    c: Coincident(g3,g0)
    c: Horizontal(g0)
    c: Horizontal(g2)
    c: Vertical(g1)
    c: Symmetric(g0,g1,g-1)
    c: DistanceX(g0,g0) = 19
    c: DistanceY(g1,g1) = 4
    c: Distance(g4) = 4
    c: Coincident(g5,g2)
    c: Coincident(g4,g6) = -1.5708
    c: Coincident(g6,g7)
    c: Coincident(g7,g8)
    c: Distance(g5) = 4
    c: Coincident(g10,g9)
    c: Coincident(g11,g10)
    c: Perpendicular(g11,g10)
    c: Perpendicular(g9,g10)
    c: Distance(g10) = 4
    c: Distance(g9) = 19
    c: Coincident(g12,g2)
    c: Vertical(g12)
    c: Distance(g12) = 19
    c: Perpendicular(g7,g8)
    c: Perpendicular(g6,g7)
    c: Distance(g8) = 19
    c: Angle(g8,g2) = 1.82387
    c: Coincident(g0,g9)
    c: Coincident(g11,g2)
    c: Vertical(g1,g0)
    c: Coincident(g14,g13)
    c: Tangent(g13,g8) = 1.5708
    c: Tangent(g14,g6) = -1.5708
    c: Tangent(g14,g0) = 1.5708
    c: Tangent(g13,g2) = -1.5708
FEATURE [PartDesign::Pad] Pad
  Direction = (0,-1,-2e-16)
  Length = 19
  Length2 = 10
  Midplane = true
  Placement = pos=(0,0,0) rot=(1,0,0;1.5708rad)
  Profile = -> Sketch
  ReferenceAxis = -> Sketch [N_Axis]
  Type = 0
FEATURE [PartDesign::Body] Body
  Group = -> [Sketch,Pad]
  Origin = -> Origin
  Tip = -> Pad
FEATURE [App::Link] Link  label="MX-Latch-SubtractorNice"
  LinkPlacement = pos=(0,0,2) rot=(0,0,1;0rad)
  LinkedObject = -> <external ../components/MX-Latch-Subtractor2.FCStd>#Body001
  Placement = pos=(0,0,2) rot=(0,0,1;0rad)
FEATURE [Part::Cut] Cut  label="KeyRowThumbBase"
  Base = -> Body
  Refine = true
  Tool = -> Link
FEATURE [App::Link] Link001  label="Cut001"
  LinkPlacement = pos=(1.2444,-1.85781,0) rot=(0,0,1;0.126536rad)
  LinkedObject = -> Cut
  Placement = pos=(1.2444,-1.85781,0) rot=(0,0,1;0.126536rad)
FEATURE [App::Link] Link002  label="Cut002"
  LinkPlacement = pos=(0,19,0) rot=(0,0,1;0rad)
  LinkedObject = -> Link001
  Placement = pos=(0,19,0) rot=(0,0,1;0rad)
FEATURE [App::Link] Link003  label="Cut003"
  LinkPlacement = pos=(1.2444,39.8578,4.36e-14) rot=(0,0,-1;0.126536rad)
  LinkedObject = -> Link002
  Placement = pos=(1.2444,39.8578,4.36e-14) rot=(0,0,-1;0.126536rad)
FEATURE [Part::MultiFuse] Fusion
  Refine = true
  Shapes = -> [Link001,Link002,Link003]
FEATURE [Sketcher::SketchObject] Sketch003
  FullyConstrained = false
  Placement = pos=(0,28.5,6e-15) rot=(-1,0,0;1.5708rad)
  sketch-geometry (10):
    g0: ArcOfCircle CenterX=-9.5 CenterY=6 CenterZ=0 NormalX=0 NormalY=1e-16 NormalZ=1 AngleXU=-1.5708 Radius=8 StartAngle=3.39467 EndAngle=4.71239
    g1: LineSegment StartX=-9.5 StartY=-2 StartZ=0 EndX=9.5 EndY=-2 EndZ=0
    g2: LineSegment StartX=9.5 StartY=-2 StartZ=0 EndX=15.2461 EndY=-2 EndZ=0
    g3: LineSegment StartX=15.2461 StartY=-2 StartZ=0 EndX=15.2461 EndY=2 EndZ=0
    g4: LineSegment StartX=15.2461 StartY=2 StartZ=0 EndX=9.5 EndY=2 EndZ=0
    g5: LineSegment StartX=9.5 StartY=2 StartZ=0 EndX=-9.5 EndY=2 EndZ=0
    g6: ArcOfCircle CenterX=-9.5 CenterY=6 CenterZ=0 NormalX=0 NormalY=1e-16 NormalZ=1 AngleXU=-1.5708 Radius=4 StartAngle=3.39467 EndAngle=4.71239
    g7: LineSegment StartX=-18.1298 StartY=23.3933 StartZ=0 EndX=-13.3726 EndY=4.99848 EndZ=0
    g8: LineSegment StartX=-22.0024 StartY=22.3918 StartZ=0 EndX=-18.1298 EndY=23.3933 EndZ=0
    g9: LineSegment StartX=-17.2452 StartY=3.99696 StartZ=0 EndX=-22.0024 EndY=22.3918 EndZ=0
  constraints (15):
    c: Coincident(g0,g1)
    c: Horizontal(g1)
    c: Coincident(g1,g2)
    c: Horizontal(g2)
    c: Coincident(g2,g3)
    c: Vertical(g3)
    c: Coincident(g3,g4)
    c: Horizontal(g4)
    c: Coincident(g4,g5)
    c: Horizontal(g5)
    c: Coincident(g5,g6)
    c: Coincident(g6,g7)
    c: Coincident(g7,g8)
    c: Coincident(g8,g9)
    c: Coincident(g9,g0)
FEATURE [Sketcher::SketchObject] Sketch004
  FullyConstrained = false
  Placement = pos=(3.81073,29.9548,-3.16e-13) rot=(0.992005,-0.126199,0;1.5708rad)
  sketch-geometry (10):
    g0: ArcOfCircle CenterX=-13.9465 CenterY=-4.27414 CenterZ=0 NormalX=0 NormalY=-1e-16 NormalZ=1 AngleXU=-1.69733 Radius=8 StartAngle=1.5708 EndAngle=2.88852
    g1: LineSegment StartX=-21.3769 StartY=-1.30968 StartZ=0 EndX=-28.4175 EndY=-18.9571 EndZ=0
    g2: LineSegment StartX=-28.4175 StartY=-18.9571 StartZ=0 EndX=-24.7023 EndY=-20.4393 EndZ=0
    g3: LineSegment StartX=-24.7023 StartY=-20.4393 StartZ=0 EndX=-17.6617 EndY=-2.79191 EndZ=0
    g4: ArcOfCircle CenterX=-13.9465 CenterY=-4.27414 CenterZ=0 NormalX=0 NormalY=-1e-16 NormalZ=1 AngleXU=-1.69733 Radius=4 StartAngle=1.5708 EndAngle=2.88852
    g5: LineSegment StartX=5.40643 StartY=-2.7039 StartZ=0 EndX=-13.4417 EndY=-0.306123 EndZ=0
    g6: LineSegment StartX=11.183 StartY=-3.43878 StartZ=0 EndX=5.40643 EndY=-2.7039 EndZ=0
    g7: LineSegment StartX=11.6878 StartY=0.529244 StartZ=0 EndX=11.183 EndY=-3.43878 EndZ=0
    g8: LineSegment StartX=5.91123 StartY=1.26412 StartZ=0 EndX=11.6878 EndY=0.529244 EndZ=0
    g9: LineSegment StartX=-12.9369 StartY=3.6619 StartZ=0 EndX=5.91123 EndY=1.26412 EndZ=0
  constraints (10):
    c: Coincident(g0,g1)
    c: Coincident(g1,g2)
    c: Coincident(g2,g3)
    c: Coincident(g3,g4)
    c: Coincident(g4,g5)
    c: Coincident(g5,g6)
    c: Coincident(g6,g7)
    c: Coincident(g7,g8)
    c: Coincident(g8,g9)
    c: Coincident(g9,g0)
FEATURE [PartDesign::AdditiveLoft] AdditiveLoft001
  Closed = false
  Placement = pos=(0,28.5,6e-15) rot=(-1,0,0;1.5708rad)
  Profile = -> Sketch003
  Ruled = false
  Sections = -> [Sketch004]
FEATURE [PartDesign::Body] Body002
  Group = -> [Sketch003,Sketch004,AdditiveLoft001]
  Origin = -> Origin002
  Tip = -> AdditiveLoft001
FEATURE [Sketcher::SketchObject] Sketch005
  FullyConstrained = false
  Placement = pos=(-0.946492,7.44004,2e-15) rot=(-0.992005,-0.126199,0;1.5708rad)
  sketch-geometry (10):
    g0: ArcOfCircle CenterX=-9.18924 CenterY=4.87934 CenterZ=0 NormalX=0 NormalY=1e-16 NormalZ=1 AngleXU=-1.44426 Radius=8 StartAngle=3.39467 EndAngle=4.71239
    g1: LineSegment StartX=-8.17964 StartY=-3.0567 StartZ=0 EndX=10.6685 EndY=-0.65892 EndZ=0
    g2: LineSegment StartX=10.6685 StartY=-0.65892 StartZ=0 EndX=16.445 EndY=0.0759518 EndZ=0
    g3: LineSegment StartX=16.445 StartY=0.0759518 StartZ=0 EndX=15.9402 EndY=4.04397 EndZ=0
    g4: LineSegment StartX=15.9402 StartY=4.04397 StartZ=0 EndX=10.1637 EndY=3.3091 EndZ=0
    g5: LineSegment StartX=10.1637 StartY=3.3091 StartZ=0 EndX=-8.68444 EndY=0.911319 EndZ=0
    g6: ArcOfCircle CenterX=-9.18924 CenterY=4.87934 CenterZ=0 NormalX=0 NormalY=1e-16 NormalZ=1 AngleXU=-1.44426 Radius=4 StartAngle=3.39467 EndAngle=4.71239
    g7: LineSegment StartX=-19.9451 StartY=21.0445 StartZ=0 EndX=-12.9045 EndY=3.39711 EndZ=0
    g8: LineSegment StartX=-23.6603 StartY=19.5623 StartZ=0 EndX=-19.9451 EndY=21.0445 EndZ=0
    g9: LineSegment StartX=-16.6197 StartY=1.91488 StartZ=0 EndX=-23.6603 EndY=19.5623 EndZ=0
  constraints (10):
    c: Coincident(g0,g1)
    c: Coincident(g1,g2)
    c: Coincident(g2,g3)
    c: Coincident(g3,g4)
    c: Coincident(g4,g5)
    c: Coincident(g5,g6)
    c: Coincident(g6,g7)
    c: Coincident(g7,g8)
    c: Coincident(g8,g9)
    c: Coincident(g9,g0)
FEATURE [Sketcher::SketchObject] Sketch006
  FullyConstrained = false
  Placement = pos=(0,9.5,2e-15) rot=(1,0,0;1.5708rad)
  sketch-geometry (10):
    g0: ArcOfCircle CenterX=-9.5 CenterY=-6 CenterZ=0 NormalX=0 NormalY=0 NormalZ=1 AngleXU=0 Radius=8 StartAngle=1.5708 EndAngle=2.88852
    g1: LineSegment StartX=-17.2452 StartY=-3.99696 StartZ=0 EndX=-22.0024 EndY=-22.3918 EndZ=0
    g2: LineSegment StartX=-22.0024 StartY=-22.3918 StartZ=0 EndX=-18.1298 EndY=-23.3933 EndZ=0
    g3: LineSegment StartX=-18.1298 StartY=-23.3933 StartZ=0 EndX=-13.3726 EndY=-4.99848 EndZ=0
    g4: ArcOfCircle CenterX=-9.5 CenterY=-6 CenterZ=0 NormalX=0 NormalY=0 NormalZ=1 AngleXU=0 Radius=4 StartAngle=1.5708 EndAngle=2.88852
    g5: LineSegment StartX=9.5 StartY=-2 StartZ=0 EndX=-9.5 EndY=-2 EndZ=0
    g6: LineSegment StartX=15.2461 StartY=-2 StartZ=0 EndX=9.5 EndY=-2 EndZ=0
    g7: LineSegment StartX=15.2461 StartY=2 StartZ=0 EndX=15.2461 EndY=-2 EndZ=0
    g8: LineSegment StartX=9.5 StartY=2 StartZ=0 EndX=15.2461 EndY=2 EndZ=0
    g9: LineSegment StartX=-9.5 StartY=2 StartZ=0 EndX=9.5 EndY=2 EndZ=0
  constraints (15):
    c: Coincident(g0,g1)
    c: Coincident(g1,g2)
    c: Coincident(g2,g3)
    c: Coincident(g3,g4)
    c: Coincident(g4,g5)
    c: Horizontal(g5)
    c: Coincident(g5,g6)
    c: Horizontal(g6)
    c: Coincident(g6,g7)
    c: Vertical(g7)
    c: Coincident(g7,g8)
    c: Horizontal(g8)
    c: Coincident(g8,g9)
    c: Horizontal(g9)
    c: Coincident(g9,g0)
FEATURE [PartDesign::AdditiveLoft] AdditiveLoft
  Closed = false
  Placement = pos=(-0.946492,7.44004,2e-15) rot=(-0.992005,-0.126199,0;1.5708rad)
  Profile = -> Sketch005
  Ruled = false
  Sections = -> [Sketch006]
FEATURE [PartDesign::Body] Body001
  Group = -> [Sketch005,Sketch006,AdditiveLoft]
  Origin = -> Origin001
  Tip = -> AdditiveLoft
FEATURE [PartDesign::SubShapeBinder] Binder
  BindCopyOnChange = 0
  BindMode = 0
  ClaimChildren = false
  Context = -> Body003 [Binder.]
  Fuse = false
  MakeFace = true
  OffsetFill = false
  OffsetIntersection = false
  OffsetJoinType = 0
  OffsetOpenResult = false
  PartialLoad = false
  Relative = true
  Support = -> [Link001[Face3]]
  _Version = 2
FEATURE [PartDesign::Pad] Pad001
  Direction = (0.126199,-0.992005,-2e-16)
  Length = 10
  Length2 = 10
  Profile = -> Binder
  Type = 0
FEATURE [PartDesign::Body] Body003
  Group = -> [Binder,Pad001]
  Origin = -> Origin003
  Tip = -> Pad001
FEATURE [Part::MultiFuse] Fusion001
  Refine = true
  Shapes = -> [Fusion,Body002,Body001,Body003]
FEATURE [Part::Refine] Fusion002  label="ThumbCluster2Nice"
  Source = -> Fusion001
---- part PlateBottom.FCStd = doc fcstd_ab97dbe754a6 ----
FCSTD DOCUMENT  (FreeCAD 0.21R33668 +26 (Git))
Label: PlateBottom
License: All rights reserved
LicenseURL: http://en.wikipedia.org/wiki/All_rights_reserved
objects: Sketcher::SketchObject×3, PartDesign::Body×2, App::Link×1, PartDesign::SubShapeBinder×1, Part::Offset2D×1, Part::Extrusion×1, PartDesign::AdditiveLoft×1, PartDesign::Pad×1, Part::FeaturePython×1, Part::Cut×1, Part::Refine×1
note: 14 computed .brp shape members not serialized (recipe doc carries the construction recipe); baked Part::Feature solids carry a one-line shape summary decoded from their .brp
EXTERNAL_REF file=KeyColumnArray2.FCStd obj=Body001

FEATURE [App::Link] Link  label="ShellRough"
  LinkedObject = -> <external KeyColumnArray2.FCStd>#Body001
FEATURE [PartDesign::SubShapeBinder] Binder
  BindCopyOnChange = 0
  BindMode = 0
  ClaimChildren = false
  Context = -> Body [Binder.]
  Fuse = false
  MakeFace = true
  OffsetFill = false
  OffsetIntersection = false
  OffsetJoinType = 0
  OffsetOpenResult = false
  PartialLoad = false
  Relative = true
  Support = -> [Link[Thickness.Edge69,Thickness.Edge70,Thickness.Edge86,Thickness.Edge85,Thickness.Edge84,Thickness.Edge83,Thickness.Edge82,Thickness.Edge81]]
  _Version = 2
FEATURE [PartDesign::Body] Body  label="BasePlate"
  Group = -> [Binder]
  Origin = -> Origin
FEATURE [Part::Offset2D] Offset2D
  Fill = false
  Intersection = false
  Join = 0
  Mode = 1
  SelfIntersection = false
  Source = -> Binder
  Value = -0.5
FEATURE [Part::Extrusion] Extrude
  Base = -> Offset2D
  Dir = (0,0,1)
  DirMode = 2
  FaceMakerClass = Part::FaceMakerBullseye
  LengthFwd = 2
  LengthRev = 0
  Solid = false
  Symmetric = false
FEATURE [Sketcher::SketchObject] Sketch
  AttachmentOffset = pos=(0,0,-1) rot=(0,0,1;0rad)
  FullyConstrained = true
  MapMode = 5
  Placement = pos=(0,0,-1) rot=(0,0,1;0rad)
  Support = -> [XY_Plane001]
  sketch-geometry (1):
    g0: Circle CenterX=0 CenterY=0 CenterZ=0 NormalX=0 NormalY=0 NormalZ=1 AngleXU=0 Radius=1
  constraints (2):
    c: Coincident(g0,g-1)
    c: Radius(g0) = 1
FEATURE [Sketcher::SketchObject] Sketch001
  FullyConstrained = true
  MapMode = 5
  Support = -> [XY_Plane001]
  sketch-geometry (1):
    g0: Circle CenterX=0 CenterY=0 CenterZ=0 NormalX=0 NormalY=0 NormalZ=1 AngleXU=0 Radius=1.5
  constraints (2):
    c: Coincident(g0,g-1)
    c: Radius(g0) = 1.5
FEATURE [PartDesign::AdditiveLoft] AdditiveLoft
  Closed = false
  Profile = -> Sketch
  Ruled = false
  Sections = -> [Sketch001]
FEATURE [PartDesign::Pad] Pad
  BaseFeature = -> AdditiveLoft
  Direction = (0,0,-1)
  Length = 10
  Length2 = 10
  Profile = -> AdditiveLoft [Face1]
  Type = 0
FEATURE [PartDesign::Body] Body001  label="ScrewCutter"
  Group = -> [Sketch,Sketch001,AdditiveLoft,Pad]
  Origin = -> Origin001
  Placement = pos=(0,0,0) rot=(1,0,0;3.14159rad)
  Tip = -> Pad
FEATURE [Sketcher::SketchObject] Sketch019
  FullyConstrained = false
  MapMode = 5
  sketch-geometry (4):
    g0: GeomPoint X=-20.7484 Y=-24.2516 Z=0
    g1: GeomPoint X=55.1532 Y=-49.1265 Z=0
    g2: GeomPoint X=85.2491 Y=15.947 Z=0
    g3: GeomPoint X=-0.005864 Y=33.4906 Z=0
FEATURE [Part::FeaturePython] PointArray  # Draft array (typed FeaturePython)
  AlwaysSyncPlacement = false
  Base = -> Body001
  Count = 4
  ExpandArray = false
  PlacementList = 4 placements: [(-20.7484,-24.2516,0),(55.1532,-49.1265,0),(85.2491,15.947,0),(-0.005864,33.4906,0)]
  PointObject = -> Sketch019
  ScaleList = (4) [(1,1,1),(1,1,1),(1,1,1),(1,1,1)]
FEATURE [Part::Cut] Cut
  Base = -> Extrude
  Tool = -> PointArray
FEATURE [Part::Refine] Cut001  label="PlateWithHolesN"
  Source = -> Cut
